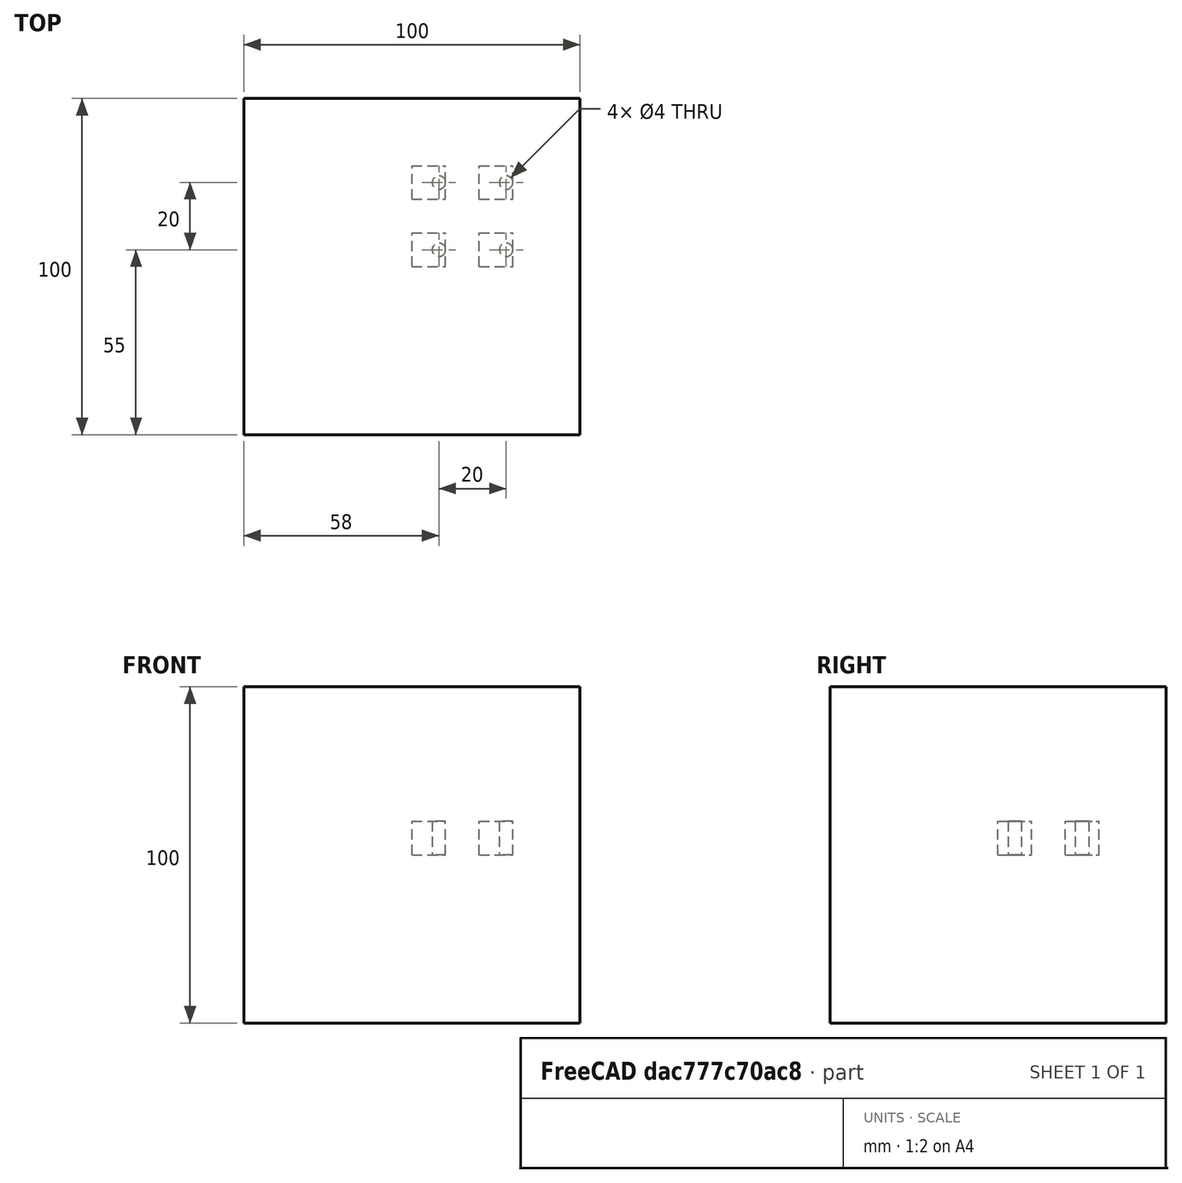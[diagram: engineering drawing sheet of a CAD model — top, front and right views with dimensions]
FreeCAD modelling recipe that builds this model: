
FCSTD DOCUMENT  (FreeCAD 0.21R33694 (Git))
Label: orthoArray_of_Cut
License: All rights reserved
objects: App::DocumentObjectGroupPython×1251, Part::FeaturePython×2, App::Part×2, Part::Box×1, Part::Cylinder×1, Part::Cut×1
note: 5 computed .brp shape members not serialized (recipe doc carries the construction recipe); baked Part::Feature solids carry a one-line shape summary decoded from their .brp

FEATURE [App::DocumentObjectGroupPython] HALFPI  # scripted group (container) (typed FeaturePython)
  name = HALFPI
  value = pi/2.
FEATURE [App::DocumentObjectGroupPython] PI  # scripted group (container) (typed FeaturePython)
  name = PI
  value = 1.*pi
FEATURE [App::DocumentObjectGroupPython] TWOPI  # scripted group (container) (typed FeaturePython)
  name = TWOPI
  value = 2.*pi
FEATURE [App::DocumentObjectGroupPython] Constants  # scripted group (container) (typed FeaturePython)
  Group = -> [HALFPI,PI,TWOPI]
FEATURE [App::DocumentObjectGroupPython] Variables  # scripted group (container) (typed FeaturePython)
FEATURE [App::DocumentObjectGroupPython] Quantities  # scripted group (container) (typed FeaturePython)
FEATURE [App::DocumentObjectGroupPython] Isotopes  # scripted group (container) (typed FeaturePython)
FEATURE [App::DocumentObjectGroupPython] Elements  # scripted group (container) (typed FeaturePython)
FEATURE [App::DocumentObjectGroupPython] Matrix  # scripted group (container) (typed FeaturePython)
FEATURE [App::DocumentObjectGroupPython] Surfaces  # scripted group (container) (typed FeaturePython)
FEATURE [App::DocumentObjectGroupPython] Opticals  # scripted group (container) (typed FeaturePython)
  Group = -> [Matrix,Surfaces]
FEATURE [App::DocumentObjectGroupPython] G4Isotopes  # scripted group (container) (typed FeaturePython)
FEATURE [App::DocumentObjectGroupPython] H_element  # scripted group (container) (typed FeaturePython)
  Z = 1
  atom_value = 1.008
  formula = H
  name = H_element
FEATURE [App::DocumentObjectGroupPython] He_element  # scripted group (container) (typed FeaturePython)
  Z = 2
  atom_value = 4.0026
  formula = He
  name = He_element
FEATURE [App::DocumentObjectGroupPython] Li_element  # scripted group (container) (typed FeaturePython)
  Z = 3
  atom_value = 6.94
  formula = Li
  name = Li_element
FEATURE [App::DocumentObjectGroupPython] Be_element  # scripted group (container) (typed FeaturePython)
  Z = 4
  atom_value = 9.01218
  formula = Be
  name = Be_element
FEATURE [App::DocumentObjectGroupPython] B_element  # scripted group (container) (typed FeaturePython)
  Z = 5
  atom_value = 10.81
  formula = B
  name = B_element
FEATURE [App::DocumentObjectGroupPython] C_element  # scripted group (container) (typed FeaturePython)
  Z = 6
  atom_value = 12.011
  formula = C
  name = C_element
FEATURE [App::DocumentObjectGroupPython] N_element  # scripted group (container) (typed FeaturePython)
  Z = 7
  atom_value = 14.007
  formula = N
  name = N_element
FEATURE [App::DocumentObjectGroupPython] O_element  # scripted group (container) (typed FeaturePython)
  Z = 8
  atom_value = 15.999
  formula = O
  name = O_element
FEATURE [App::DocumentObjectGroupPython] F_element  # scripted group (container) (typed FeaturePython)
  Z = 9
  atom_value = 18.9984
  formula = F
  name = F_element
FEATURE [App::DocumentObjectGroupPython] Ne_element  # scripted group (container) (typed FeaturePython)
  Z = 10
  atom_value = 20.1797
  formula = Ne
  name = Ne_element
FEATURE [App::DocumentObjectGroupPython] Na_element  # scripted group (container) (typed FeaturePython)
  Z = 11
  atom_value = 22.9898
  formula = Na
  name = Na_element
FEATURE [App::DocumentObjectGroupPython] Mg_element  # scripted group (container) (typed FeaturePython)
  Z = 12
  atom_value = 24.305
  formula = Mg
  name = Mg_element
FEATURE [App::DocumentObjectGroupPython] Al_element  # scripted group (container) (typed FeaturePython)
  Z = 13
  atom_value = 26.9815
  formula = Al
  name = Al_element
FEATURE [App::DocumentObjectGroupPython] Si_element  # scripted group (container) (typed FeaturePython)
  Z = 14
  atom_value = 28.085
  formula = Si
  name = Si_element
FEATURE [App::DocumentObjectGroupPython] P_element  # scripted group (container) (typed FeaturePython)
  Z = 15
  atom_value = 30.9738
  formula = P
  name = P_element
FEATURE [App::DocumentObjectGroupPython] S_element  # scripted group (container) (typed FeaturePython)
  Z = 16
  atom_value = 32.06
  formula = S
  name = S_element
FEATURE [App::DocumentObjectGroupPython] Cl_element  # scripted group (container) (typed FeaturePython)
  Z = 17
  atom_value = 35.45
  formula = Cl
  name = Cl_element
FEATURE [App::DocumentObjectGroupPython] Ar_element  # scripted group (container) (typed FeaturePython)
  Z = 18
  atom_value = 39.95
  formula = Ar
  name = Ar_element
FEATURE [App::DocumentObjectGroupPython] K_element  # scripted group (container) (typed FeaturePython)
  Z = 19
  atom_value = 39.0983
  formula = K
  name = K_element
FEATURE [App::DocumentObjectGroupPython] Ca_element  # scripted group (container) (typed FeaturePython)
  Z = 20
  atom_value = 40.078
  formula = Ca
  name = Ca_element
FEATURE [App::DocumentObjectGroupPython] Sc_element  # scripted group (container) (typed FeaturePython)
  Z = 21
  atom_value = 44.9559
  formula = Sc
  name = Sc_element
FEATURE [App::DocumentObjectGroupPython] Ti_element  # scripted group (container) (typed FeaturePython)
  Z = 22
  atom_value = 47.867
  formula = Ti
  name = Ti_element
FEATURE [App::DocumentObjectGroupPython] V_element  # scripted group (container) (typed FeaturePython)
  Z = 23
  atom_value = 50.9415
  formula = V
  name = V_element
FEATURE [App::DocumentObjectGroupPython] Cr_element  # scripted group (container) (typed FeaturePython)
  Z = 24
  atom_value = 51.9961
  formula = Cr
  name = Cr_element
FEATURE [App::DocumentObjectGroupPython] Mn_element  # scripted group (container) (typed FeaturePython)
  Z = 25
  atom_value = 54.938
  formula = Mn
  name = Mn_element
FEATURE [App::DocumentObjectGroupPython] Fe_element  # scripted group (container) (typed FeaturePython)
  Z = 26
  atom_value = 55.845
  formula = Fe
  name = Fe_element
FEATURE [App::DocumentObjectGroupPython] Co_element  # scripted group (container) (typed FeaturePython)
  Z = 27
  atom_value = 58.9332
  formula = Co
  name = Co_element
FEATURE [App::DocumentObjectGroupPython] Ni_element  # scripted group (container) (typed FeaturePython)
  Z = 28
  atom_value = 58.6934
  formula = Ni
  name = Ni_element
FEATURE [App::DocumentObjectGroupPython] Cu_element  # scripted group (container) (typed FeaturePython)
  Z = 29
  atom_value = 63.546
  formula = Cu
  name = Cu_element
FEATURE [App::DocumentObjectGroupPython] Zn_element  # scripted group (container) (typed FeaturePython)
  Z = 30
  atom_value = 65.38
  formula = Zn
  name = Zn_element
FEATURE [App::DocumentObjectGroupPython] Ga_element  # scripted group (container) (typed FeaturePython)
  Z = 31
  atom_value = 69.723
  formula = Ga
  name = Ga_element
FEATURE [App::DocumentObjectGroupPython] Ge_element  # scripted group (container) (typed FeaturePython)
  Z = 32
  atom_value = 72.63
  formula = Ge
  name = Ge_element
FEATURE [App::DocumentObjectGroupPython] As_element  # scripted group (container) (typed FeaturePython)
  Z = 33
  atom_value = 74.9216
  formula = As
  name = As_element
FEATURE [App::DocumentObjectGroupPython] Se_element  # scripted group (container) (typed FeaturePython)
  Z = 34
  atom_value = 78.971
  formula = Se
  name = Se_element
FEATURE [App::DocumentObjectGroupPython] Br_element  # scripted group (container) (typed FeaturePython)
  Z = 35
  atom_value = 79.904
  formula = Br
  name = Br_element
FEATURE [App::DocumentObjectGroupPython] Kr_element  # scripted group (container) (typed FeaturePython)
  Z = 36
  atom_value = 83.798
  formula = Kr
  name = Kr_element
FEATURE [App::DocumentObjectGroupPython] Rb_element  # scripted group (container) (typed FeaturePython)
  Z = 37
  atom_value = 85.4678
  formula = Rb
  name = Rb_element
FEATURE [App::DocumentObjectGroupPython] Sr_element  # scripted group (container) (typed FeaturePython)
  Z = 38
  atom_value = 87.62
  formula = Sr
  name = Sr_element
FEATURE [App::DocumentObjectGroupPython] Y_element  # scripted group (container) (typed FeaturePython)
  Z = 39
  atom_value = 88.9058
  formula = Y
  name = Y_element
FEATURE [App::DocumentObjectGroupPython] Zr_element  # scripted group (container) (typed FeaturePython)
  Z = 40
  atom_value = 91.224
  formula = Zr
  name = Zr_element
FEATURE [App::DocumentObjectGroupPython] Nb_element  # scripted group (container) (typed FeaturePython)
  Z = 41
  atom_value = 92.9064
  formula = Nb
  name = Nb_element
FEATURE [App::DocumentObjectGroupPython] Mo_element  # scripted group (container) (typed FeaturePython)
  Z = 42
  atom_value = 95.95
  formula = Mo
  name = Mo_element
FEATURE [App::DocumentObjectGroupPython] Tc_element  # scripted group (container) (typed FeaturePython)
  Z = 43
  atom_value = 97
  formula = Tc
  name = Tc_element
FEATURE [App::DocumentObjectGroupPython] Ru_element  # scripted group (container) (typed FeaturePython)
  Z = 44
  atom_value = 101.07
  formula = Ru
  name = Ru_element
FEATURE [App::DocumentObjectGroupPython] Rh_element  # scripted group (container) (typed FeaturePython)
  Z = 45
  atom_value = 102.905
  formula = Rh
  name = Rh_element
FEATURE [App::DocumentObjectGroupPython] Pd_element  # scripted group (container) (typed FeaturePython)
  Z = 46
  atom_value = 106.42
  formula = Pd
  name = Pd_element
FEATURE [App::DocumentObjectGroupPython] Ag_element  # scripted group (container) (typed FeaturePython)
  Z = 47
  atom_value = 107.868
  formula = Ag
  name = Ag_element
FEATURE [App::DocumentObjectGroupPython] Cd_element  # scripted group (container) (typed FeaturePython)
  Z = 48
  atom_value = 112.414
  formula = Cd
  name = Cd_element
FEATURE [App::DocumentObjectGroupPython] In_element  # scripted group (container) (typed FeaturePython)
  Z = 49
  atom_value = 114.818
  formula = In
  name = In_element
FEATURE [App::DocumentObjectGroupPython] Sn_element  # scripted group (container) (typed FeaturePython)
  Z = 50
  atom_value = 118.71
  formula = Sn
  name = Sn_element
FEATURE [App::DocumentObjectGroupPython] Sb_element  # scripted group (container) (typed FeaturePython)
  Z = 51
  atom_value = 121.76
  formula = Sb
  name = Sb_element
FEATURE [App::DocumentObjectGroupPython] Te_element  # scripted group (container) (typed FeaturePython)
  Z = 52
  atom_value = 127.6
  formula = Te
  name = Te_element
FEATURE [App::DocumentObjectGroupPython] I_element  # scripted group (container) (typed FeaturePython)
  Z = 53
  atom_value = 126.904
  formula = I
  name = I_element
FEATURE [App::DocumentObjectGroupPython] Xe_element  # scripted group (container) (typed FeaturePython)
  Z = 54
  atom_value = 131.293
  formula = Xe
  name = Xe_element
FEATURE [App::DocumentObjectGroupPython] Cs_element  # scripted group (container) (typed FeaturePython)
  Z = 55
  atom_value = 132.905
  formula = Cs
  name = Cs_element
FEATURE [App::DocumentObjectGroupPython] Ba_element  # scripted group (container) (typed FeaturePython)
  Z = 56
  atom_value = 137.327
  formula = Ba
  name = Ba_element
FEATURE [App::DocumentObjectGroupPython] La_element  # scripted group (container) (typed FeaturePython)
  Z = 57
  atom_value = 138.905
  formula = La
  name = La_element
FEATURE [App::DocumentObjectGroupPython] Ce_element  # scripted group (container) (typed FeaturePython)
  Z = 58
  atom_value = 140.116
  formula = Ce
  name = Ce_element
FEATURE [App::DocumentObjectGroupPython] Pr_element  # scripted group (container) (typed FeaturePython)
  Z = 59
  atom_value = 140.908
  formula = Pr
  name = Pr_element
FEATURE [App::DocumentObjectGroupPython] Nd_element  # scripted group (container) (typed FeaturePython)
  Z = 60
  atom_value = 144.242
  formula = Nd
  name = Nd_element
FEATURE [App::DocumentObjectGroupPython] Pm_element  # scripted group (container) (typed FeaturePython)
  Z = 61
  atom_value = 145
  formula = Pm
  name = Pm_element
FEATURE [App::DocumentObjectGroupPython] Sm_element  # scripted group (container) (typed FeaturePython)
  Z = 62
  atom_value = 150.36
  formula = Sm
  name = Sm_element
FEATURE [App::DocumentObjectGroupPython] Eu_element  # scripted group (container) (typed FeaturePython)
  Z = 63
  atom_value = 151.964
  formula = Eu
  name = Eu_element
FEATURE [App::DocumentObjectGroupPython] Gd_element  # scripted group (container) (typed FeaturePython)
  Z = 64
  atom_value = 157.25
  formula = Gd
  name = Gd_element
FEATURE [App::DocumentObjectGroupPython] Tb_element  # scripted group (container) (typed FeaturePython)
  Z = 65
  atom_value = 158.925
  formula = Tb
  name = Tb_element
FEATURE [App::DocumentObjectGroupPython] Dy_element  # scripted group (container) (typed FeaturePython)
  Z = 66
  atom_value = 162.5
  formula = Dy
  name = Dy_element
FEATURE [App::DocumentObjectGroupPython] Ho_element  # scripted group (container) (typed FeaturePython)
  Z = 67
  atom_value = 164.93
  formula = Ho
  name = Ho_element
FEATURE [App::DocumentObjectGroupPython] Er_element  # scripted group (container) (typed FeaturePython)
  Z = 68
  atom_value = 167.259
  formula = Er
  name = Er_element
FEATURE [App::DocumentObjectGroupPython] Tm_element  # scripted group (container) (typed FeaturePython)
  Z = 69
  atom_value = 168.934
  formula = Tm
  name = Tm_element
FEATURE [App::DocumentObjectGroupPython] Yb_element  # scripted group (container) (typed FeaturePython)
  Z = 70
  atom_value = 173.045
  formula = Yb
  name = Yb_element
FEATURE [App::DocumentObjectGroupPython] Lu_element  # scripted group (container) (typed FeaturePython)
  Z = 71
  atom_value = 174.967
  formula = Lu
  name = Lu_element
FEATURE [App::DocumentObjectGroupPython] Hf_element  # scripted group (container) (typed FeaturePython)
  Z = 72
  atom_value = 178.49
  formula = Hf
  name = Hf_element
FEATURE [App::DocumentObjectGroupPython] Ta_element  # scripted group (container) (typed FeaturePython)
  Z = 73
  atom_value = 180.948
  formula = Ta
  name = Ta_element
FEATURE [App::DocumentObjectGroupPython] W_element  # scripted group (container) (typed FeaturePython)
  Z = 74
  atom_value = 183.84
  formula = W
  name = W_element
FEATURE [App::DocumentObjectGroupPython] Re_element  # scripted group (container) (typed FeaturePython)
  Z = 75
  atom_value = 186.207
  formula = Re
  name = Re_element
FEATURE [App::DocumentObjectGroupPython] Os_element  # scripted group (container) (typed FeaturePython)
  Z = 76
  atom_value = 190.23
  formula = Os
  name = Os_element
FEATURE [App::DocumentObjectGroupPython] Ir_element  # scripted group (container) (typed FeaturePython)
  Z = 77
  atom_value = 192.217
  formula = Ir
  name = Ir_element
FEATURE [App::DocumentObjectGroupPython] Pt_element  # scripted group (container) (typed FeaturePython)
  Z = 78
  atom_value = 195.084
  formula = Pt
  name = Pt_element
FEATURE [App::DocumentObjectGroupPython] Au_element  # scripted group (container) (typed FeaturePython)
  Z = 79
  atom_value = 196.967
  formula = Au
  name = Au_element
FEATURE [App::DocumentObjectGroupPython] Hg_element  # scripted group (container) (typed FeaturePython)
  Z = 80
  atom_value = 200.592
  formula = Hg
  name = Hg_element
FEATURE [App::DocumentObjectGroupPython] Tl_element  # scripted group (container) (typed FeaturePython)
  Z = 81
  atom_value = 204.38
  formula = Tl
  name = Tl_element
FEATURE [App::DocumentObjectGroupPython] Pb_element  # scripted group (container) (typed FeaturePython)
  Z = 82
  atom_value = 207.2
  formula = Pb
  name = Pb_element
FEATURE [App::DocumentObjectGroupPython] Bi_element  # scripted group (container) (typed FeaturePython)
  Z = 83
  atom_value = 208.98
  formula = Bi
  name = Bi_element
FEATURE [App::DocumentObjectGroupPython] Po_element  # scripted group (container) (typed FeaturePython)
  Z = 84
  atom_value = 209
  formula = Po
  name = Po_element
FEATURE [App::DocumentObjectGroupPython] At_element  # scripted group (container) (typed FeaturePython)
  Z = 85
  atom_value = 210
  formula = At
  name = At_element
FEATURE [App::DocumentObjectGroupPython] Rn_element  # scripted group (container) (typed FeaturePython)
  Z = 86
  atom_value = 222
  formula = Rn
  name = Rn_element
FEATURE [App::DocumentObjectGroupPython] Fr_element  # scripted group (container) (typed FeaturePython)
  Z = 87
  atom_value = 223
  formula = Fr
  name = Fr_element
FEATURE [App::DocumentObjectGroupPython] Ra_element  # scripted group (container) (typed FeaturePython)
  Z = 88
  atom_value = 226
  formula = Ra
  name = Ra_element
FEATURE [App::DocumentObjectGroupPython] Ac_element  # scripted group (container) (typed FeaturePython)
  Z = 89
  atom_value = 227
  formula = Ac
  name = Ac_element
FEATURE [App::DocumentObjectGroupPython] Th_element  # scripted group (container) (typed FeaturePython)
  Z = 90
  atom_value = 232.038
  formula = Th
  name = Th_element
FEATURE [App::DocumentObjectGroupPython] Pa_element  # scripted group (container) (typed FeaturePython)
  Z = 91
  atom_value = 231.036
  formula = Pa
  name = Pa_element
FEATURE [App::DocumentObjectGroupPython] U_element  # scripted group (container) (typed FeaturePython)
  Z = 92
  atom_value = 238.029
  formula = U
  name = U_element
FEATURE [App::DocumentObjectGroupPython] Np_element  # scripted group (container) (typed FeaturePython)
  Z = 93
  atom_value = 237
  formula = Np
  name = Np_element
FEATURE [App::DocumentObjectGroupPython] Pu_element  # scripted group (container) (typed FeaturePython)
  Z = 94
  atom_value = 244
  formula = Pu
  name = Pu_element
FEATURE [App::DocumentObjectGroupPython] Am_element  # scripted group (container) (typed FeaturePython)
  Z = 95
  atom_value = 243
  formula = Am
  name = Am_element
FEATURE [App::DocumentObjectGroupPython] Cm_element  # scripted group (container) (typed FeaturePython)
  Z = 96
  atom_value = 247
  formula = Cm
  name = Cm_element
FEATURE [App::DocumentObjectGroupPython] Bk_element  # scripted group (container) (typed FeaturePython)
  Z = 97
  atom_value = 247
  formula = Bk
  name = Bk_element
FEATURE [App::DocumentObjectGroupPython] Cf_element  # scripted group (container) (typed FeaturePython)
  Z = 98
  atom_value = 251
  formula = Cf
  name = Cf_element
FEATURE [App::DocumentObjectGroupPython] G4Elements  # scripted group (container) (typed FeaturePython)
  Group = -> [H_element,He_element,Li_element,Be_element,B_element,C_element,N_element,O_element,F_element,Ne_element,Na_element,Mg_element,Al_element,Si_element,P_element,S_element,Cl_element,Ar_element,K_element,Ca_element,Sc_element,Ti_element,V_element,Cr_element,Mn_element,Fe_element,Co_element,Ni_element,Cu_element,Zn_element,Ga_element,Ge_element,As_element,Se_element,Br_element,Kr_element,Rb_element,+61 more]
FEATURE [App::DocumentObjectGroupPython] H_element001  label="H_element : 0.101"  # scripted group (container) (typed FeaturePython)
  n = 0.101327
FEATURE [App::DocumentObjectGroupPython] C_element001  label="C_element : 0.775"  # scripted group (container) (typed FeaturePython)
  n = 0.7755
FEATURE [App::DocumentObjectGroupPython] N_element001  label="N_element : 0.035"  # scripted group (container) (typed FeaturePython)
  n = 0.035057
FEATURE [App::DocumentObjectGroupPython] O_element001  label="O_element : 0.052"  # scripted group (container) (typed FeaturePython)
  n = 0.0523159
FEATURE [App::DocumentObjectGroupPython] F_element001  label="F_element : 0.017"  # scripted group (container) (typed FeaturePython)
  n = 0.017422
FEATURE [App::DocumentObjectGroupPython] Ca_element001  label="Ca_element : 0.018"  # scripted group (container) (typed FeaturePython)
  n = 0.018378
FEATURE [App::DocumentObjectGroupPython] G4_A_150_TISSUE  label="G4_A-150_TISSUE"  # scripted group (container) (typed FeaturePython)
  Dunit = g/cm3
  Dvalue = 1.127
  Group = -> [H_element001,C_element001,N_element001,O_element001,F_element001,Ca_element001]
  conduct = 2
  density = 1
  expand = 3
  formula = G4_A-150_TISSUE
  name = G4_A-150_TISSUE
  specific = 4
FEATURE [App::DocumentObjectGroupPython] C_element002  label="C_element : 3"  # scripted group (container) (typed FeaturePython)
  n = 3
  ref = C_element
FEATURE [App::DocumentObjectGroupPython] H_element002  label="H_element : 6"  # scripted group (container) (typed FeaturePython)
  n = 6
  ref = H_element
FEATURE [App::DocumentObjectGroupPython] O_element002  label="O_element : 1"  # scripted group (container) (typed FeaturePython)
  n = 1
  ref = O_element
FEATURE [App::DocumentObjectGroupPython] G4_ACETONE  # scripted group (container) (typed FeaturePython)
  Dunit = g/cm3
  Dvalue = 0.7899
  Group = -> [C_element002,H_element002,O_element002]
  conduct = 2
  density = 1
  expand = 3
  formula = G4_ACETONE
  name = G4_ACETONE
  specific = 4
FEATURE [App::DocumentObjectGroupPython] C_element003  label="C_element : 2"  # scripted group (container) (typed FeaturePython)
  n = 2
  ref = C_element
FEATURE [App::DocumentObjectGroupPython] H_element003  label="H_element : 2"  # scripted group (container) (typed FeaturePython)
  n = 2
  ref = H_element
FEATURE [App::DocumentObjectGroupPython] G4_ACETYLENE  # scripted group (container) (typed FeaturePython)
  Dunit = g/cm3
  Dvalue = 0.0010967
  Group = -> [C_element003,H_element003]
  conduct = 2
  density = 1
  expand = 3
  formula = G4_ACETYLENE
  name = G4_ACETYLENE
  specific = 4
FEATURE [App::DocumentObjectGroupPython] C_element004  label="C_element : 5"  # scripted group (container) (typed FeaturePython)
  n = 5
  ref = C_element
FEATURE [App::DocumentObjectGroupPython] H_element004  label="H_element : 5"  # scripted group (container) (typed FeaturePython)
  n = 5
  ref = H_element
FEATURE [App::DocumentObjectGroupPython] N_element002  label="N_element : 5"  # scripted group (container) (typed FeaturePython)
  n = 5
  ref = N_element
FEATURE [App::DocumentObjectGroupPython] G4_ADENINE  # scripted group (container) (typed FeaturePython)
  Dunit = g/cm3
  Dvalue = 1.6
  Group = -> [C_element004,H_element004,N_element002]
  conduct = 2
  density = 1
  expand = 3
  formula = G4_ADENINE
  name = G4_ADENINE
  specific = 4
FEATURE [App::DocumentObjectGroupPython] H_element005  label="H_element : 0.114"  # scripted group (container) (typed FeaturePython)
  n = 0.114
FEATURE [App::DocumentObjectGroupPython] C_element005  label="C_element : 0.598"  # scripted group (container) (typed FeaturePython)
  n = 0.598
FEATURE [App::DocumentObjectGroupPython] N_element003  label="N_element : 0.007"  # scripted group (container) (typed FeaturePython)
  n = 0.007
FEATURE [App::DocumentObjectGroupPython] O_element003  label="O_element : 0.278"  # scripted group (container) (typed FeaturePython)
  n = 0.278
FEATURE [App::DocumentObjectGroupPython] Na_element001  label="Na_element : 0.001"  # scripted group (container) (typed FeaturePython)
  n = 0.001
FEATURE [App::DocumentObjectGroupPython] S_element001  label="S_element : 0.001"  # scripted group (container) (typed FeaturePython)
  n = 0.001
FEATURE [App::DocumentObjectGroupPython] Cl_element001  label="Cl_element : 0.001"  # scripted group (container) (typed FeaturePython)
  n = 0.001
FEATURE [App::DocumentObjectGroupPython] G4_ADIPOSE_TISSUE_ICRP  # scripted group (container) (typed FeaturePython)
  Dunit = g/cm3
  Dvalue = 0.95
  Group = -> [H_element005,C_element005,N_element003,O_element003,Na_element001,S_element001,Cl_element001]
  conduct = 2
  density = 1
  expand = 3
  formula = G4_ADIPOSE_TISSUE_ICRP
  name = G4_ADIPOSE_TISSUE_ICRP
  specific = 4
FEATURE [App::DocumentObjectGroupPython] C_element006  label="C_element : 0.000"  # scripted group (container) (typed FeaturePython)
  n = 0.000124
FEATURE [App::DocumentObjectGroupPython] N_element004  label="N_element : 0.755"  # scripted group (container) (typed FeaturePython)
  n = 0.755268
FEATURE [App::DocumentObjectGroupPython] O_element004  label="O_element : 0.232"  # scripted group (container) (typed FeaturePython)
  n = 0.231781
FEATURE [App::DocumentObjectGroupPython] Ar_element001  label="Ar_element : 0.013"  # scripted group (container) (typed FeaturePython)
  n = 0.012827
FEATURE [App::DocumentObjectGroupPython] G4_AIR  # scripted group (container) (typed FeaturePython)
  Dunit = g/cm3
  Dvalue = 0.00120479
  Group = -> [C_element006,N_element004,O_element004,Ar_element001]
  conduct = 2
  density = 1
  expand = 3
  formula = G4_AIR
  name = G4_AIR
  specific = 4
FEATURE [App::DocumentObjectGroupPython] C_element007  label="C_element : 006"  # scripted group (container) (typed FeaturePython)
  n = 3
  ref = C_element
FEATURE [App::DocumentObjectGroupPython] H_element006  label="H_element : 7"  # scripted group (container) (typed FeaturePython)
  n = 7
  ref = H_element
FEATURE [App::DocumentObjectGroupPython] N_element005  label="N_element : 1"  # scripted group (container) (typed FeaturePython)
  n = 1
  ref = N_element
FEATURE [App::DocumentObjectGroupPython] O_element005  label="O_element : 2"  # scripted group (container) (typed FeaturePython)
  n = 2
  ref = O_element
FEATURE [App::DocumentObjectGroupPython] G4_ALANINE  # scripted group (container) (typed FeaturePython)
  Dunit = g/cm3
  Dvalue = 1.42
  Group = -> [C_element007,H_element006,N_element005,O_element005]
  conduct = 2
  density = 1
  expand = 3
  formula = G4_ALANINE
  name = G4_ALANINE
  specific = 4
FEATURE [App::DocumentObjectGroupPython] Al_element001  label="Al_element : 2"  # scripted group (container) (typed FeaturePython)
  n = 2
  ref = Al_element
FEATURE [App::DocumentObjectGroupPython] O_element006  label="O_element : 3"  # scripted group (container) (typed FeaturePython)
  n = 3
  ref = O_element
FEATURE [App::DocumentObjectGroupPython] G4_ALUMINUM_OXIDE  # scripted group (container) (typed FeaturePython)
  Dunit = g/cm3
  Dvalue = 3.97
  Group = -> [Al_element001,O_element006]
  conduct = 2
  density = 1
  expand = 3
  formula = G4_ALUMINUM_OXIDE
  name = G4_ALUMINUM_OXIDE
  specific = 4
FEATURE [App::DocumentObjectGroupPython] H_element007  label="H_element : 0.106"  # scripted group (container) (typed FeaturePython)
  n = 0.10593
FEATURE [App::DocumentObjectGroupPython] C_element008  label="C_element : 0.789"  # scripted group (container) (typed FeaturePython)
  n = 0.788974
FEATURE [App::DocumentObjectGroupPython] O_element007  label="O_element : 0.105"  # scripted group (container) (typed FeaturePython)
  n = 0.105096
FEATURE [App::DocumentObjectGroupPython] G4_AMBER  # scripted group (container) (typed FeaturePython)
  Dunit = g/cm3
  Dvalue = 1.1
  Group = -> [H_element007,C_element008,O_element007]
  conduct = 2
  density = 1
  expand = 3
  formula = G4_AMBER
  name = G4_AMBER
  specific = 4
FEATURE [App::DocumentObjectGroupPython] N_element006  label="N_element : 006"  # scripted group (container) (typed FeaturePython)
  n = 1
  ref = N_element
FEATURE [App::DocumentObjectGroupPython] H_element008  label="H_element : 3"  # scripted group (container) (typed FeaturePython)
  n = 3
  ref = H_element
FEATURE [App::DocumentObjectGroupPython] G4_AMMONIA  # scripted group (container) (typed FeaturePython)
  Dunit = g/cm3
  Dvalue = 0.000826019
  Group = -> [N_element006,H_element008]
  conduct = 2
  density = 1
  expand = 3
  formula = G4_AMMONIA
  name = G4_AMMONIA
  specific = 4
FEATURE [App::DocumentObjectGroupPython] C_element009  label="C_element : 6"  # scripted group (container) (typed FeaturePython)
  n = 6
  ref = C_element
FEATURE [App::DocumentObjectGroupPython] H_element009  label="H_element : 008"  # scripted group (container) (typed FeaturePython)
  n = 7
  ref = H_element
FEATURE [App::DocumentObjectGroupPython] N_element007  label="N_element : 007"  # scripted group (container) (typed FeaturePython)
  n = 1
  ref = N_element
FEATURE [App::DocumentObjectGroupPython] G4_ANILINE  # scripted group (container) (typed FeaturePython)
  Dunit = g/cm3
  Dvalue = 1.0235
  Group = -> [C_element009,H_element009,N_element007]
  conduct = 2
  density = 1
  expand = 3
  formula = G4_ANILINE
  name = G4_ANILINE
  specific = 4
FEATURE [App::DocumentObjectGroupPython] C_element010  label="C_element : 14"  # scripted group (container) (typed FeaturePython)
  n = 14
  ref = C_element
FEATURE [App::DocumentObjectGroupPython] H_element010  label="H_element : 10"  # scripted group (container) (typed FeaturePython)
  n = 10
  ref = H_element
FEATURE [App::DocumentObjectGroupPython] G4_ANTHRACENE  # scripted group (container) (typed FeaturePython)
  Dunit = g/cm3
  Dvalue = 1.283
  Group = -> [C_element010,H_element010]
  conduct = 2
  density = 1
  expand = 3
  formula = G4_ANTHRACENE
  name = G4_ANTHRACENE
  specific = 4
FEATURE [App::DocumentObjectGroupPython] H_element011  label="H_element : 0.065"  # scripted group (container) (typed FeaturePython)
  n = 0.0654709
FEATURE [App::DocumentObjectGroupPython] C_element011  label="C_element : 0.537"  # scripted group (container) (typed FeaturePython)
  n = 0.536944
FEATURE [App::DocumentObjectGroupPython] N_element008  label="N_element : 0.021"  # scripted group (container) (typed FeaturePython)
  n = 0.0215
FEATURE [App::DocumentObjectGroupPython] O_element008  label="O_element : 0.032"  # scripted group (container) (typed FeaturePython)
  n = 0.032085
FEATURE [App::DocumentObjectGroupPython] F_element002  label="F_element : 0.167"  # scripted group (container) (typed FeaturePython)
  n = 0.167411
FEATURE [App::DocumentObjectGroupPython] Ca_element002  label="Ca_element : 0.177"  # scripted group (container) (typed FeaturePython)
  n = 0.176589
FEATURE [App::DocumentObjectGroupPython] G4_B_100_BONE  label="G4_B-100_BONE"  # scripted group (container) (typed FeaturePython)
  Dunit = g/cm3
  Dvalue = 1.45
  Group = -> [H_element011,C_element011,N_element008,O_element008,F_element002,Ca_element002]
  conduct = 2
  density = 1
  expand = 3
  formula = G4_B-100_BONE
  name = G4_B-100_BONE
  specific = 4
FEATURE [App::DocumentObjectGroupPython] H_element012  label="H_element : 0.057"  # scripted group (container) (typed FeaturePython)
  n = 0.057441
FEATURE [App::DocumentObjectGroupPython] C_element012  label="C_element : 0.790"  # scripted group (container) (typed FeaturePython)
  n = 0.774591
FEATURE [App::DocumentObjectGroupPython] O_element009  label="O_element : 0.168"  # scripted group (container) (typed FeaturePython)
  n = 0.167968
FEATURE [App::DocumentObjectGroupPython] G4_BAKELITE  # scripted group (container) (typed FeaturePython)
  Dunit = g/cm3
  Dvalue = 1.25
  Group = -> [H_element012,C_element012,O_element009]
  conduct = 2
  density = 1
  expand = 3
  formula = G4_BAKELITE
  name = G4_BAKELITE
  specific = 4
FEATURE [App::DocumentObjectGroupPython] Ba_element001  label="Ba_element : 1"  # scripted group (container) (typed FeaturePython)
  n = 1
  ref = Ba_element
FEATURE [App::DocumentObjectGroupPython] F_element003  label="F_element : 2"  # scripted group (container) (typed FeaturePython)
  n = 2
  ref = F_element
FEATURE [App::DocumentObjectGroupPython] G4_BARIUM_FLUORIDE  # scripted group (container) (typed FeaturePython)
  Dunit = g/cm3
  Dvalue = 4.89
  Group = -> [Ba_element001,F_element003]
  conduct = 2
  density = 1
  expand = 3
  formula = G4_BARIUM_FLUORIDE
  name = G4_BARIUM_FLUORIDE
  specific = 4
FEATURE [App::DocumentObjectGroupPython] Ba_element002  label="Ba_element : 002"  # scripted group (container) (typed FeaturePython)
  n = 1
  ref = Ba_element
FEATURE [App::DocumentObjectGroupPython] S_element002  label="S_element : 1"  # scripted group (container) (typed FeaturePython)
  n = 1
  ref = S_element
FEATURE [App::DocumentObjectGroupPython] O_element010  label="O_element : 4"  # scripted group (container) (typed FeaturePython)
  n = 4
  ref = O_element
FEATURE [App::DocumentObjectGroupPython] G4_BARIUM_SULFATE  # scripted group (container) (typed FeaturePython)
  Dunit = g/cm3
  Dvalue = 4.5
  Group = -> [Ba_element002,S_element002,O_element010]
  conduct = 2
  density = 1
  expand = 3
  formula = G4_BARIUM_SULFATE
  name = G4_BARIUM_SULFATE
  specific = 4
FEATURE [App::DocumentObjectGroupPython] C_element013  label="C_element : 007"  # scripted group (container) (typed FeaturePython)
  n = 6
  ref = C_element
FEATURE [App::DocumentObjectGroupPython] H_element013  label="H_element : 009"  # scripted group (container) (typed FeaturePython)
  n = 6
  ref = H_element
FEATURE [App::DocumentObjectGroupPython] G4_BENZENE  # scripted group (container) (typed FeaturePython)
  Dunit = g/cm3
  Dvalue = 0.87865
  Group = -> [C_element013,H_element013]
  conduct = 2
  density = 1
  expand = 3
  formula = G4_BENZENE
  name = G4_BENZENE
  specific = 4
FEATURE [App::DocumentObjectGroupPython] Be_element001  label="Be_element : 1"  # scripted group (container) (typed FeaturePython)
  n = 1
  ref = Be_element
FEATURE [App::DocumentObjectGroupPython] O_element011  label="O_element : 005"  # scripted group (container) (typed FeaturePython)
  n = 1
  ref = O_element
FEATURE [App::DocumentObjectGroupPython] G4_BERYLLIUM_OXIDE  # scripted group (container) (typed FeaturePython)
  Dunit = g/cm3
  Dvalue = 3.01
  Group = -> [Be_element001,O_element011]
  conduct = 2
  density = 1
  expand = 3
  formula = G4_BERYLLIUM_OXIDE
  name = G4_BERYLLIUM_OXIDE
  specific = 4
FEATURE [App::DocumentObjectGroupPython] Bi_element001  label="Bi_element : 4"  # scripted group (container) (typed FeaturePython)
  n = 4
  ref = Bi_element
FEATURE [App::DocumentObjectGroupPython] Ge_element001  label="Ge_element : 3"  # scripted group (container) (typed FeaturePython)
  n = 3
  ref = Ge_element
FEATURE [App::DocumentObjectGroupPython] O_element012  label="O_element : 12"  # scripted group (container) (typed FeaturePython)
  n = 12
  ref = O_element
FEATURE [App::DocumentObjectGroupPython] G4_BGO  # scripted group (container) (typed FeaturePython)
  Dunit = g/cm3
  Dvalue = 7.13
  Group = -> [Bi_element001,Ge_element001,O_element012]
  conduct = 2
  density = 1
  expand = 3
  formula = G4_BGO
  name = G4_BGO
  specific = 4
FEATURE [App::DocumentObjectGroupPython] H_element014  label="H_element : 0.102"  # scripted group (container) (typed FeaturePython)
  n = 0.102
FEATURE [App::DocumentObjectGroupPython] C_element014  label="C_element : 0.110"  # scripted group (container) (typed FeaturePython)
  n = 0.11
FEATURE [App::DocumentObjectGroupPython] N_element009  label="N_element : 0.033"  # scripted group (container) (typed FeaturePython)
  n = 0.033
FEATURE [App::DocumentObjectGroupPython] O_element013  label="O_element : 0.745"  # scripted group (container) (typed FeaturePython)
  n = 0.745
FEATURE [App::DocumentObjectGroupPython] Na_element002  label="Na_element : 0.002"  # scripted group (container) (typed FeaturePython)
  n = 0.001
FEATURE [App::DocumentObjectGroupPython] P_element001  label="P_element : 0.001"  # scripted group (container) (typed FeaturePython)
  n = 0.001
FEATURE [App::DocumentObjectGroupPython] S_element003  label="S_element : 0.002"  # scripted group (container) (typed FeaturePython)
  n = 0.002
FEATURE [App::DocumentObjectGroupPython] Cl_element002  label="Cl_element : 0.003"  # scripted group (container) (typed FeaturePython)
  n = 0.003
FEATURE [App::DocumentObjectGroupPython] K_element001  label="K_element : 0.002"  # scripted group (container) (typed FeaturePython)
  n = 0.002
FEATURE [App::DocumentObjectGroupPython] Fe_element001  label="Fe_element : 0.001"  # scripted group (container) (typed FeaturePython)
  n = 0.001
FEATURE [App::DocumentObjectGroupPython] G4_BLOOD_ICRP  # scripted group (container) (typed FeaturePython)
  Dunit = g/cm3
  Dvalue = 1.06
  Group = -> [H_element014,C_element014,N_element009,O_element013,Na_element002,P_element001,S_element003,Cl_element002,K_element001,Fe_element001]
  conduct = 2
  density = 1
  expand = 3
  formula = G4_BLOOD_ICRP
  name = G4_BLOOD_ICRP
  specific = 4
FEATURE [App::DocumentObjectGroupPython] H_element015  label="H_element : 0.064"  # scripted group (container) (typed FeaturePython)
  n = 0.064
FEATURE [App::DocumentObjectGroupPython] C_element015  label="C_element : 0.278"  # scripted group (container) (typed FeaturePython)
  n = 0.278
FEATURE [App::DocumentObjectGroupPython] N_element010  label="N_element : 0.027"  # scripted group (container) (typed FeaturePython)
  n = 0.027
FEATURE [App::DocumentObjectGroupPython] O_element014  label="O_element : 0.410"  # scripted group (container) (typed FeaturePython)
  n = 0.41
FEATURE [App::DocumentObjectGroupPython] Mg_element001  label="Mg_element : 0.002"  # scripted group (container) (typed FeaturePython)
  n = 0.002
FEATURE [App::DocumentObjectGroupPython] P_element002  label="P_element : 0.070"  # scripted group (container) (typed FeaturePython)
  n = 0.07
FEATURE [App::DocumentObjectGroupPython] S_element004  label="S_element : 0.003"  # scripted group (container) (typed FeaturePython)
  n = 0.002
FEATURE [App::DocumentObjectGroupPython] Ca_element003  label="Ca_element : 0.147"  # scripted group (container) (typed FeaturePython)
  n = 0.147
FEATURE [App::DocumentObjectGroupPython] G4_BONE_COMPACT_ICRU  # scripted group (container) (typed FeaturePython)
  Dunit = g/cm3
  Dvalue = 1.85
  Group = -> [H_element015,C_element015,N_element010,O_element014,Mg_element001,P_element002,S_element004,Ca_element003]
  conduct = 2
  density = 1
  expand = 3
  formula = G4_BONE_COMPACT_ICRU
  name = G4_BONE_COMPACT_ICRU
  specific = 4
FEATURE [App::DocumentObjectGroupPython] H_element016  label="H_element : 0.034"  # scripted group (container) (typed FeaturePython)
  n = 0.034
FEATURE [App::DocumentObjectGroupPython] C_element016  label="C_element : 0.155"  # scripted group (container) (typed FeaturePython)
  n = 0.155
FEATURE [App::DocumentObjectGroupPython] N_element011  label="N_element : 0.042"  # scripted group (container) (typed FeaturePython)
  n = 0.042
FEATURE [App::DocumentObjectGroupPython] O_element015  label="O_element : 0.435"  # scripted group (container) (typed FeaturePython)
  n = 0.435
FEATURE [App::DocumentObjectGroupPython] Na_element003  label="Na_element : 0.003"  # scripted group (container) (typed FeaturePython)
  n = 0.001
FEATURE [App::DocumentObjectGroupPython] Mg_element002  label="Mg_element : 0.003"  # scripted group (container) (typed FeaturePython)
  n = 0.002
FEATURE [App::DocumentObjectGroupPython] P_element003  label="P_element : 0.103"  # scripted group (container) (typed FeaturePython)
  n = 0.103
FEATURE [App::DocumentObjectGroupPython] S_element005  label="S_element : 0.004"  # scripted group (container) (typed FeaturePython)
  n = 0.003
FEATURE [App::DocumentObjectGroupPython] Ca_element004  label="Ca_element : 0.225"  # scripted group (container) (typed FeaturePython)
  n = 0.225
FEATURE [App::DocumentObjectGroupPython] G4_BONE_CORTICAL_ICRP  # scripted group (container) (typed FeaturePython)
  Dunit = g/cm3
  Dvalue = 1.92
  Group = -> [H_element016,C_element016,N_element011,O_element015,Na_element003,Mg_element002,P_element003,S_element005,Ca_element004]
  conduct = 2
  density = 1
  expand = 3
  formula = G4_BONE_CORTICAL_ICRP
  name = G4_BONE_CORTICAL_ICRP
  specific = 4
FEATURE [App::DocumentObjectGroupPython] B_element001  label="B_element : 4"  # scripted group (container) (typed FeaturePython)
  n = 4
  ref = B_element
FEATURE [App::DocumentObjectGroupPython] C_element017  label="C_element : 1"  # scripted group (container) (typed FeaturePython)
  n = 1
  ref = C_element
FEATURE [App::DocumentObjectGroupPython] G4_BORON_CARBIDE  # scripted group (container) (typed FeaturePython)
  Dunit = g/cm3
  Dvalue = 2.52
  Group = -> [B_element001,C_element017]
  conduct = 2
  density = 1
  expand = 3
  formula = G4_BORON_CARBIDE
  name = G4_BORON_CARBIDE
  specific = 4
FEATURE [App::DocumentObjectGroupPython] B_element002  label="B_element : 2"  # scripted group (container) (typed FeaturePython)
  n = 2
  ref = B_element
FEATURE [App::DocumentObjectGroupPython] O_element016  label="O_element : 006"  # scripted group (container) (typed FeaturePython)
  n = 3
  ref = O_element
FEATURE [App::DocumentObjectGroupPython] G4_BORON_OXIDE  # scripted group (container) (typed FeaturePython)
  Dunit = g/cm3
  Dvalue = 1.812
  Group = -> [B_element002,O_element016]
  conduct = 2
  density = 1
  expand = 3
  formula = G4_BORON_OXIDE
  name = G4_BORON_OXIDE
  specific = 4
FEATURE [App::DocumentObjectGroupPython] H_element017  label="H_element : 0.107"  # scripted group (container) (typed FeaturePython)
  n = 0.107
FEATURE [App::DocumentObjectGroupPython] C_element018  label="C_element : 0.145"  # scripted group (container) (typed FeaturePython)
  n = 0.145
FEATURE [App::DocumentObjectGroupPython] N_element012  label="N_element : 0.022"  # scripted group (container) (typed FeaturePython)
  n = 0.022
FEATURE [App::DocumentObjectGroupPython] O_element017  label="O_element : 0.712"  # scripted group (container) (typed FeaturePython)
  n = 0.712
FEATURE [App::DocumentObjectGroupPython] Na_element004  label="Na_element : 0.004"  # scripted group (container) (typed FeaturePython)
  n = 0.002
FEATURE [App::DocumentObjectGroupPython] P_element004  label="P_element : 0.004"  # scripted group (container) (typed FeaturePython)
  n = 0.004
FEATURE [App::DocumentObjectGroupPython] S_element006  label="S_element : 0.005"  # scripted group (container) (typed FeaturePython)
  n = 0.002
FEATURE [App::DocumentObjectGroupPython] Cl_element003  label="Cl_element : 0.004"  # scripted group (container) (typed FeaturePython)
  n = 0.003
FEATURE [App::DocumentObjectGroupPython] K_element002  label="K_element : 0.003"  # scripted group (container) (typed FeaturePython)
  n = 0.003
FEATURE [App::DocumentObjectGroupPython] G4_BRAIN_ICRP  # scripted group (container) (typed FeaturePython)
  Dunit = g/cm3
  Dvalue = 1.04
  Group = -> [H_element017,C_element018,N_element012,O_element017,Na_element004,P_element004,S_element006,Cl_element003,K_element002]
  conduct = 2
  density = 1
  expand = 3
  formula = G4_BRAIN_ICRP
  name = G4_BRAIN_ICRP
  specific = 4
FEATURE [App::DocumentObjectGroupPython] C_element019  label="C_element : 4"  # scripted group (container) (typed FeaturePython)
  n = 4
  ref = C_element
FEATURE [App::DocumentObjectGroupPython] H_element018  label="H_element : 010"  # scripted group (container) (typed FeaturePython)
  n = 10
  ref = H_element
FEATURE [App::DocumentObjectGroupPython] G4_BUTANE  # scripted group (container) (typed FeaturePython)
  Dunit = g/cm3
  Dvalue = 0.00249343
  Group = -> [C_element019,H_element018]
  conduct = 2
  density = 1
  expand = 3
  formula = G4_BUTANE
  name = G4_BUTANE
  specific = 4
FEATURE [App::DocumentObjectGroupPython] C_element020  label="C_element : 008"  # scripted group (container) (typed FeaturePython)
  n = 4
  ref = C_element
FEATURE [App::DocumentObjectGroupPython] H_element019  label="H_element : 011"  # scripted group (container) (typed FeaturePython)
  n = 10
  ref = H_element
FEATURE [App::DocumentObjectGroupPython] O_element018  label="O_element : 007"  # scripted group (container) (typed FeaturePython)
  n = 1
  ref = O_element
FEATURE [App::DocumentObjectGroupPython] G4_N_BUTYL_ALCOHOL  label="G4_N-BUTYL_ALCOHOL"  # scripted group (container) (typed FeaturePython)
  Dunit = g/cm3
  Dvalue = 0.8098
  Group = -> [C_element020,H_element019,O_element018]
  conduct = 2
  density = 1
  expand = 3
  formula = G4_N-BUTYL_ALCOHOL
  name = G4_N-BUTYL_ALCOHOL
  specific = 4
FEATURE [App::DocumentObjectGroupPython] H_element020  label="H_element : 0.025"  # scripted group (container) (typed FeaturePython)
  n = 0.02468
FEATURE [App::DocumentObjectGroupPython] C_element021  label="C_element : 0.502"  # scripted group (container) (typed FeaturePython)
  n = 0.501611
FEATURE [App::DocumentObjectGroupPython] O_element019  label="O_element : 0.005"  # scripted group (container) (typed FeaturePython)
  n = 0.004527
FEATURE [App::DocumentObjectGroupPython] F_element004  label="F_element : 0.465"  # scripted group (container) (typed FeaturePython)
  n = 0.465209
FEATURE [App::DocumentObjectGroupPython] Si_element001  label="Si_element : 0.004"  # scripted group (container) (typed FeaturePython)
  n = 0.003973
FEATURE [App::DocumentObjectGroupPython] G4_C_552  label="G4_C-552"  # scripted group (container) (typed FeaturePython)
  Dunit = g/cm3
  Dvalue = 1.76
  Group = -> [H_element020,C_element021,O_element019,F_element004,Si_element001]
  conduct = 2
  density = 1
  expand = 3
  formula = G4_C-552
  name = G4_C-552
  specific = 4
FEATURE [App::DocumentObjectGroupPython] Cd_element001  label="Cd_element : 1"  # scripted group (container) (typed FeaturePython)
  n = 1
  ref = Cd_element
FEATURE [App::DocumentObjectGroupPython] Te_element001  label="Te_element : 1"  # scripted group (container) (typed FeaturePython)
  n = 1
  ref = Te_element
FEATURE [App::DocumentObjectGroupPython] G4_CADMIUM_TELLURIDE  # scripted group (container) (typed FeaturePython)
  Dunit = g/cm3
  Dvalue = 6.2
  Group = -> [Cd_element001,Te_element001]
  conduct = 2
  density = 1
  expand = 3
  formula = G4_CADMIUM_TELLURIDE
  name = G4_CADMIUM_TELLURIDE
  specific = 4
FEATURE [App::DocumentObjectGroupPython] Cd_element002  label="Cd_element : 002"  # scripted group (container) (typed FeaturePython)
  n = 1
  ref = Cd_element
FEATURE [App::DocumentObjectGroupPython] W_element001  label="W_element : 1"  # scripted group (container) (typed FeaturePython)
  n = 1
  ref = W_element
FEATURE [App::DocumentObjectGroupPython] O_element020  label="O_element : 008"  # scripted group (container) (typed FeaturePython)
  n = 4
  ref = O_element
FEATURE [App::DocumentObjectGroupPython] G4_CADMIUM_TUNGSTATE  # scripted group (container) (typed FeaturePython)
  Dunit = g/cm3
  Dvalue = 7.9
  Group = -> [Cd_element002,W_element001,O_element020]
  conduct = 2
  density = 1
  expand = 3
  formula = G4_CADMIUM_TUNGSTATE
  name = G4_CADMIUM_TUNGSTATE
  specific = 4
FEATURE [App::DocumentObjectGroupPython] Ca_element005  label="Ca_element : 1"  # scripted group (container) (typed FeaturePython)
  n = 1
  ref = Ca_element
FEATURE [App::DocumentObjectGroupPython] C_element022  label="C_element : 009"  # scripted group (container) (typed FeaturePython)
  n = 1
  ref = C_element
FEATURE [App::DocumentObjectGroupPython] O_element021  label="O_element : 009"  # scripted group (container) (typed FeaturePython)
  n = 3
  ref = O_element
FEATURE [App::DocumentObjectGroupPython] G4_CALCIUM_CARBONATE  # scripted group (container) (typed FeaturePython)
  Dunit = g/cm3
  Dvalue = 2.8
  Group = -> [Ca_element005,C_element022,O_element021]
  conduct = 2
  density = 1
  expand = 3
  formula = G4_CALCIUM_CARBONATE
  name = G4_CALCIUM_CARBONATE
  specific = 4
FEATURE [App::DocumentObjectGroupPython] Ca_element006  label="Ca_element : 002"  # scripted group (container) (typed FeaturePython)
  n = 1
  ref = Ca_element
FEATURE [App::DocumentObjectGroupPython] F_element005  label="F_element : 003"  # scripted group (container) (typed FeaturePython)
  n = 2
  ref = F_element
FEATURE [App::DocumentObjectGroupPython] G4_CALCIUM_FLUORIDE  # scripted group (container) (typed FeaturePython)
  Dunit = g/cm3
  Dvalue = 3.18
  Group = -> [Ca_element006,F_element005]
  conduct = 2
  density = 1
  expand = 3
  formula = G4_CALCIUM_FLUORIDE
  name = G4_CALCIUM_FLUORIDE
  specific = 4
FEATURE [App::DocumentObjectGroupPython] Ca_element007  label="Ca_element : 003"  # scripted group (container) (typed FeaturePython)
  n = 1
  ref = Ca_element
FEATURE [App::DocumentObjectGroupPython] O_element022  label="O_element : 010"  # scripted group (container) (typed FeaturePython)
  n = 1
  ref = O_element
FEATURE [App::DocumentObjectGroupPython] G4_CALCIUM_OXIDE  # scripted group (container) (typed FeaturePython)
  Dunit = g/cm3
  Dvalue = 3.3
  Group = -> [Ca_element007,O_element022]
  conduct = 2
  density = 1
  expand = 3
  formula = G4_CALCIUM_OXIDE
  name = G4_CALCIUM_OXIDE
  specific = 4
FEATURE [App::DocumentObjectGroupPython] Ca_element008  label="Ca_element : 004"  # scripted group (container) (typed FeaturePython)
  n = 1
  ref = Ca_element
FEATURE [App::DocumentObjectGroupPython] S_element007  label="S_element : 002"  # scripted group (container) (typed FeaturePython)
  n = 1
  ref = S_element
FEATURE [App::DocumentObjectGroupPython] O_element023  label="O_element : 011"  # scripted group (container) (typed FeaturePython)
  n = 4
  ref = O_element
FEATURE [App::DocumentObjectGroupPython] G4_CALCIUM_SULFATE  # scripted group (container) (typed FeaturePython)
  Dunit = g/cm3
  Dvalue = 2.96
  Group = -> [Ca_element008,S_element007,O_element023]
  conduct = 2
  density = 1
  expand = 3
  formula = G4_CALCIUM_SULFATE
  name = G4_CALCIUM_SULFATE
  specific = 4
FEATURE [App::DocumentObjectGroupPython] Ca_element009  label="Ca_element : 005"  # scripted group (container) (typed FeaturePython)
  n = 1
  ref = Ca_element
FEATURE [App::DocumentObjectGroupPython] W_element002  label="W_element : 002"  # scripted group (container) (typed FeaturePython)
  n = 1
  ref = W_element
FEATURE [App::DocumentObjectGroupPython] O_element024  label="O_element : 012"  # scripted group (container) (typed FeaturePython)
  n = 4
  ref = O_element
FEATURE [App::DocumentObjectGroupPython] G4_CALCIUM_TUNGSTATE  # scripted group (container) (typed FeaturePython)
  Dunit = g/cm3
  Dvalue = 6.062
  Group = -> [Ca_element009,W_element002,O_element024]
  conduct = 2
  density = 1
  expand = 3
  formula = G4_CALCIUM_TUNGSTATE
  name = G4_CALCIUM_TUNGSTATE
  specific = 4
FEATURE [App::DocumentObjectGroupPython] C_element023  label="C_element : 010"  # scripted group (container) (typed FeaturePython)
  n = 1
  ref = C_element
FEATURE [App::DocumentObjectGroupPython] O_element025  label="O_element : 013"  # scripted group (container) (typed FeaturePython)
  n = 2
  ref = O_element
FEATURE [App::DocumentObjectGroupPython] G4_CARBON_DIOXIDE  # scripted group (container) (typed FeaturePython)
  Dunit = g/cm3
  Dvalue = 0.00184212
  Group = -> [C_element023,O_element025]
  conduct = 2
  density = 1
  expand = 3
  formula = G4_CARBON_DIOXIDE
  name = G4_CARBON_DIOXIDE
  specific = 4
FEATURE [App::DocumentObjectGroupPython] C_element024  label="C_element : 011"  # scripted group (container) (typed FeaturePython)
  n = 1
  ref = C_element
FEATURE [App::DocumentObjectGroupPython] Cl_element004  label="Cl_element : 4"  # scripted group (container) (typed FeaturePython)
  n = 4
  ref = Cl_element
FEATURE [App::DocumentObjectGroupPython] G4_CARBON_TETRACHLORIDE  # scripted group (container) (typed FeaturePython)
  Dunit = g/cm3
  Dvalue = 1.594
  Group = -> [C_element024,Cl_element004]
  conduct = 2
  density = 1
  expand = 3
  formula = G4_CARBON_TETRACHLORIDE
  name = G4_CARBON_TETRACHLORIDE
  specific = 4
FEATURE [App::DocumentObjectGroupPython] C_element025  label="C_element : 012"  # scripted group (container) (typed FeaturePython)
  n = 6
  ref = C_element
FEATURE [App::DocumentObjectGroupPython] H_element021  label="H_element : 012"  # scripted group (container) (typed FeaturePython)
  n = 10
  ref = H_element
FEATURE [App::DocumentObjectGroupPython] O_element026  label="O_element : 5"  # scripted group (container) (typed FeaturePython)
  n = 5
  ref = O_element
FEATURE [App::DocumentObjectGroupPython] G4_CELLULOSE_CELLOPHANE  # scripted group (container) (typed FeaturePython)
  Dunit = g/cm3
  Dvalue = 1.42
  Group = -> [C_element025,H_element021,O_element026]
  conduct = 2
  density = 1
  expand = 3
  formula = G4_CELLULOSE_CELLOPHANE
  name = G4_CELLULOSE_CELLOPHANE
  specific = 4
FEATURE [App::DocumentObjectGroupPython] H_element022  label="H_element : 0.067"  # scripted group (container) (typed FeaturePython)
  n = 0.067125
FEATURE [App::DocumentObjectGroupPython] C_element026  label="C_element : 0.545"  # scripted group (container) (typed FeaturePython)
  n = 0.545403
FEATURE [App::DocumentObjectGroupPython] O_element027  label="O_element : 0.387"  # scripted group (container) (typed FeaturePython)
  n = 0.387472
FEATURE [App::DocumentObjectGroupPython] G4_CELLULOSE_BUTYRATE  # scripted group (container) (typed FeaturePython)
  Dunit = g/cm3
  Dvalue = 1.2
  Group = -> [H_element022,C_element026,O_element027]
  conduct = 2
  density = 1
  expand = 3
  formula = G4_CELLULOSE_BUTYRATE
  name = G4_CELLULOSE_BUTYRATE
  specific = 4
FEATURE [App::DocumentObjectGroupPython] H_element023  label="H_element : 0.029"  # scripted group (container) (typed FeaturePython)
  n = 0.029216
FEATURE [App::DocumentObjectGroupPython] C_element027  label="C_element : 0.271"  # scripted group (container) (typed FeaturePython)
  n = 0.271296
FEATURE [App::DocumentObjectGroupPython] N_element013  label="N_element : 0.121"  # scripted group (container) (typed FeaturePython)
  n = 0.121276
FEATURE [App::DocumentObjectGroupPython] O_element028  label="O_element : 0.578"  # scripted group (container) (typed FeaturePython)
  n = 0.578212
FEATURE [App::DocumentObjectGroupPython] G4_CELLULOSE_NITRATE  # scripted group (container) (typed FeaturePython)
  Dunit = g/cm3
  Dvalue = 1.49
  Group = -> [H_element023,C_element027,N_element013,O_element028]
  conduct = 2
  density = 1
  expand = 3
  formula = G4_CELLULOSE_NITRATE
  name = G4_CELLULOSE_NITRATE
  specific = 4
FEATURE [App::DocumentObjectGroupPython] H_element024  label="H_element : 0.108"  # scripted group (container) (typed FeaturePython)
  n = 0.107596
FEATURE [App::DocumentObjectGroupPython] N_element014  label="N_element : 0.001"  # scripted group (container) (typed FeaturePython)
  n = 0.0008
FEATURE [App::DocumentObjectGroupPython] O_element029  label="O_element : 0.875"  # scripted group (container) (typed FeaturePython)
  n = 0.874976
FEATURE [App::DocumentObjectGroupPython] S_element008  label="S_element : 0.015"  # scripted group (container) (typed FeaturePython)
  n = 0.014627
FEATURE [App::DocumentObjectGroupPython] Ce_element001  label="Ce_element : 0.002"  # scripted group (container) (typed FeaturePython)
  n = 0.002001
FEATURE [App::DocumentObjectGroupPython] G4_CERIC_SULFATE  # scripted group (container) (typed FeaturePython)
  Dunit = g/cm3
  Dvalue = 1.03
  Group = -> [H_element024,N_element014,O_element029,S_element008,Ce_element001]
  conduct = 2
  density = 1
  expand = 3
  formula = G4_CERIC_SULFATE
  name = G4_CERIC_SULFATE
  specific = 4
FEATURE [App::DocumentObjectGroupPython] Cs_element001  label="Cs_element : 1"  # scripted group (container) (typed FeaturePython)
  n = 1
  ref = Cs_element
FEATURE [App::DocumentObjectGroupPython] F_element006  label="F_element : 1"  # scripted group (container) (typed FeaturePython)
  n = 1
  ref = F_element
FEATURE [App::DocumentObjectGroupPython] G4_CESIUM_FLUORIDE  # scripted group (container) (typed FeaturePython)
  Dunit = g/cm3
  Dvalue = 4.115
  Group = -> [Cs_element001,F_element006]
  conduct = 2
  density = 1
  expand = 3
  formula = G4_CESIUM_FLUORIDE
  name = G4_CESIUM_FLUORIDE
  specific = 4
FEATURE [App::DocumentObjectGroupPython] Cs_element002  label="Cs_element : 002"  # scripted group (container) (typed FeaturePython)
  n = 1
  ref = Cs_element
FEATURE [App::DocumentObjectGroupPython] I_element001  label="I_element : 1"  # scripted group (container) (typed FeaturePython)
  n = 1
  ref = I_element
FEATURE [App::DocumentObjectGroupPython] G4_CESIUM_IODIDE  # scripted group (container) (typed FeaturePython)
  Dunit = g/cm3
  Dvalue = 4.51
  Group = -> [Cs_element002,I_element001]
  conduct = 2
  density = 1
  expand = 3
  formula = G4_CESIUM_IODIDE
  name = G4_CESIUM_IODIDE
  specific = 4
FEATURE [App::DocumentObjectGroupPython] C_element028  label="C_element : 013"  # scripted group (container) (typed FeaturePython)
  n = 6
  ref = C_element
FEATURE [App::DocumentObjectGroupPython] H_element025  label="H_element : 013"  # scripted group (container) (typed FeaturePython)
  n = 5
  ref = H_element
FEATURE [App::DocumentObjectGroupPython] Cl_element005  label="Cl_element : 1"  # scripted group (container) (typed FeaturePython)
  n = 1
  ref = Cl_element
FEATURE [App::DocumentObjectGroupPython] G4_CHLOROBENZENE  # scripted group (container) (typed FeaturePython)
  Dunit = g/cm3
  Dvalue = 1.1058
  Group = -> [C_element028,H_element025,Cl_element005]
  conduct = 2
  density = 1
  expand = 3
  formula = G4_CHLOROBENZENE
  name = G4_CHLOROBENZENE
  specific = 4
FEATURE [App::DocumentObjectGroupPython] C_element029  label="C_element : 014"  # scripted group (container) (typed FeaturePython)
  n = 1
  ref = C_element
FEATURE [App::DocumentObjectGroupPython] H_element026  label="H_element : 1"  # scripted group (container) (typed FeaturePython)
  n = 1
  ref = H_element
FEATURE [App::DocumentObjectGroupPython] Cl_element006  label="Cl_element : 3"  # scripted group (container) (typed FeaturePython)
  n = 3
  ref = Cl_element
FEATURE [App::DocumentObjectGroupPython] G4_CHLOROFORM  # scripted group (container) (typed FeaturePython)
  Dunit = g/cm3
  Dvalue = 1.4832
  Group = -> [C_element029,H_element026,Cl_element006]
  conduct = 2
  density = 1
  expand = 3
  formula = G4_CHLOROFORM
  name = G4_CHLOROFORM
  specific = 4
FEATURE [App::DocumentObjectGroupPython] H_element027  label="H_element : 0.010"  # scripted group (container) (typed FeaturePython)
  n = 0.01
FEATURE [App::DocumentObjectGroupPython] C_element030  label="C_element : 0.001"  # scripted group (container) (typed FeaturePython)
  n = 0.001
FEATURE [App::DocumentObjectGroupPython] O_element030  label="O_element : 0.529"  # scripted group (container) (typed FeaturePython)
  n = 0.529107
FEATURE [App::DocumentObjectGroupPython] Na_element005  label="Na_element : 0.016"  # scripted group (container) (typed FeaturePython)
  n = 0.016
FEATURE [App::DocumentObjectGroupPython] Mg_element003  label="Mg_element : 0.004"  # scripted group (container) (typed FeaturePython)
  n = 0.002
FEATURE [App::DocumentObjectGroupPython] Al_element002  label="Al_element : 0.034"  # scripted group (container) (typed FeaturePython)
  n = 0.033872
FEATURE [App::DocumentObjectGroupPython] Si_element002  label="Si_element : 0.337"  # scripted group (container) (typed FeaturePython)
  n = 0.337021
FEATURE [App::DocumentObjectGroupPython] K_element003  label="K_element : 0.013"  # scripted group (container) (typed FeaturePython)
  n = 0.013
FEATURE [App::DocumentObjectGroupPython] Ca_element010  label="Ca_element : 0.044"  # scripted group (container) (typed FeaturePython)
  n = 0.044
FEATURE [App::DocumentObjectGroupPython] Fe_element002  label="Fe_element : 0.014"  # scripted group (container) (typed FeaturePython)
  n = 0.014
FEATURE [App::DocumentObjectGroupPython] G4_CONCRETE  # scripted group (container) (typed FeaturePython)
  Dunit = g/cm3
  Dvalue = 2.3
  Group = -> [H_element027,C_element030,O_element030,Na_element005,Mg_element003,Al_element002,Si_element002,K_element003,Ca_element010,Fe_element002]
  conduct = 2
  density = 1
  expand = 3
  formula = G4_CONCRETE
  name = G4_CONCRETE
  specific = 4
FEATURE [App::DocumentObjectGroupPython] C_element031  label="C_element : 015"  # scripted group (container) (typed FeaturePython)
  n = 6
  ref = C_element
FEATURE [App::DocumentObjectGroupPython] H_element028  label="H_element : 12"  # scripted group (container) (typed FeaturePython)
  n = 12
  ref = H_element
FEATURE [App::DocumentObjectGroupPython] G4_CYCLOHEXANE  # scripted group (container) (typed FeaturePython)
  Dunit = g/cm3
  Dvalue = 0.779
  Group = -> [C_element031,H_element028]
  conduct = 2
  density = 1
  expand = 3
  formula = G4_CYCLOHEXANE
  name = G4_CYCLOHEXANE
  specific = 4
FEATURE [App::DocumentObjectGroupPython] C_element032  label="C_element : 016"  # scripted group (container) (typed FeaturePython)
  n = 6
  ref = C_element
FEATURE [App::DocumentObjectGroupPython] H_element029  label="H_element : 4"  # scripted group (container) (typed FeaturePython)
  n = 4
  ref = H_element
FEATURE [App::DocumentObjectGroupPython] Cl_element007  label="Cl_element : 2"  # scripted group (container) (typed FeaturePython)
  n = 2
  ref = Cl_element
FEATURE [App::DocumentObjectGroupPython] G4_1_2_DICHLOROBENZENE  label="G4_1.2-DICHLOROBENZENE"  # scripted group (container) (typed FeaturePython)
  Dunit = g/cm3
  Dvalue = 1.3048
  Group = -> [C_element032,H_element029,Cl_element007]
  conduct = 2
  density = 1
  expand = 3
  formula = G4_1.2-DICHLOROBENZENE
  name = G4_1.2-DICHLOROBENZENE
  specific = 4
FEATURE [App::DocumentObjectGroupPython] C_element033  label="C_element : 017"  # scripted group (container) (typed FeaturePython)
  n = 4
  ref = C_element
FEATURE [App::DocumentObjectGroupPython] H_element030  label="H_element : 8"  # scripted group (container) (typed FeaturePython)
  n = 8
  ref = H_element
FEATURE [App::DocumentObjectGroupPython] O_element031  label="O_element : 014"  # scripted group (container) (typed FeaturePython)
  n = 1
  ref = O_element
FEATURE [App::DocumentObjectGroupPython] Cl_element008  label="Cl_element : 005"  # scripted group (container) (typed FeaturePython)
  n = 2
  ref = Cl_element
FEATURE [App::DocumentObjectGroupPython] G4_DICHLORODIETHYL_ETHER  # scripted group (container) (typed FeaturePython)
  Dunit = g/cm3
  Dvalue = 1.2199
  Group = -> [C_element033,H_element030,O_element031,Cl_element008]
  conduct = 2
  density = 1
  expand = 3
  formula = G4_DICHLORODIETHYL_ETHER
  name = G4_DICHLORODIETHYL_ETHER
  specific = 4
FEATURE [App::DocumentObjectGroupPython] C_element034  label="C_element : 018"  # scripted group (container) (typed FeaturePython)
  n = 2
  ref = C_element
FEATURE [App::DocumentObjectGroupPython] H_element031  label="H_element : 014"  # scripted group (container) (typed FeaturePython)
  n = 4
  ref = H_element
FEATURE [App::DocumentObjectGroupPython] Cl_element009  label="Cl_element : 006"  # scripted group (container) (typed FeaturePython)
  n = 2
  ref = Cl_element
FEATURE [App::DocumentObjectGroupPython] G4_1_2_DICHLOROETHANE  label="G4_1.2-DICHLOROETHANE"  # scripted group (container) (typed FeaturePython)
  Dunit = g/cm3
  Dvalue = 1.2351
  Group = -> [C_element034,H_element031,Cl_element009]
  conduct = 2
  density = 1
  expand = 3
  formula = G4_1.2-DICHLOROETHANE
  name = G4_1.2-DICHLOROETHANE
  specific = 4
FEATURE [App::DocumentObjectGroupPython] C_element035  label="C_element : 019"  # scripted group (container) (typed FeaturePython)
  n = 4
  ref = C_element
FEATURE [App::DocumentObjectGroupPython] H_element032  label="H_element : 015"  # scripted group (container) (typed FeaturePython)
  n = 10
  ref = H_element
FEATURE [App::DocumentObjectGroupPython] O_element032  label="O_element : 015"  # scripted group (container) (typed FeaturePython)
  n = 1
  ref = O_element
FEATURE [App::DocumentObjectGroupPython] G4_DIETHYL_ETHER  # scripted group (container) (typed FeaturePython)
  Dunit = g/cm3
  Dvalue = 0.71378
  Group = -> [C_element035,H_element032,O_element032]
  conduct = 2
  density = 1
  expand = 3
  formula = G4_DIETHYL_ETHER
  name = G4_DIETHYL_ETHER
  specific = 4
FEATURE [App::DocumentObjectGroupPython] C_element036  label="C_element : 020"  # scripted group (container) (typed FeaturePython)
  n = 3
  ref = C_element
FEATURE [App::DocumentObjectGroupPython] H_element033  label="H_element : 016"  # scripted group (container) (typed FeaturePython)
  n = 7
  ref = H_element
FEATURE [App::DocumentObjectGroupPython] N_element015  label="N_element : 008"  # scripted group (container) (typed FeaturePython)
  n = 1
  ref = N_element
FEATURE [App::DocumentObjectGroupPython] O_element033  label="O_element : 016"  # scripted group (container) (typed FeaturePython)
  n = 1
  ref = O_element
FEATURE [App::DocumentObjectGroupPython] G4_N_N_DIMETHYL_FORMAMIDE  label="G4_N.N-DIMETHYL_FORMAMIDE"  # scripted group (container) (typed FeaturePython)
  Dunit = g/cm3
  Dvalue = 0.9487
  Group = -> [C_element036,H_element033,N_element015,O_element033]
  conduct = 2
  density = 1
  expand = 3
  formula = G4_N.N-DIMETHYL_FORMAMIDE
  name = G4_N.N-DIMETHYL_FORMAMIDE
  specific = 4
FEATURE [App::DocumentObjectGroupPython] C_element037  label="C_element : 021"  # scripted group (container) (typed FeaturePython)
  n = 2
  ref = C_element
FEATURE [App::DocumentObjectGroupPython] H_element034  label="H_element : 017"  # scripted group (container) (typed FeaturePython)
  n = 6
  ref = H_element
FEATURE [App::DocumentObjectGroupPython] O_element034  label="O_element : 017"  # scripted group (container) (typed FeaturePython)
  n = 1
  ref = O_element
FEATURE [App::DocumentObjectGroupPython] S_element009  label="S_element : 003"  # scripted group (container) (typed FeaturePython)
  n = 1
  ref = S_element
FEATURE [App::DocumentObjectGroupPython] G4_DIMETHYL_SULFOXIDE  # scripted group (container) (typed FeaturePython)
  Dunit = g/cm3
  Dvalue = 1.1014
  Group = -> [C_element037,H_element034,O_element034,S_element009]
  conduct = 2
  density = 1
  expand = 3
  formula = G4_DIMETHYL_SULFOXIDE
  name = G4_DIMETHYL_SULFOXIDE
  specific = 4
FEATURE [App::DocumentObjectGroupPython] C_element038  label="C_element : 022"  # scripted group (container) (typed FeaturePython)
  n = 2
  ref = C_element
FEATURE [App::DocumentObjectGroupPython] H_element035  label="H_element : 018"  # scripted group (container) (typed FeaturePython)
  n = 6
  ref = H_element
FEATURE [App::DocumentObjectGroupPython] G4_ETHANE  # scripted group (container) (typed FeaturePython)
  Dunit = g/cm3
  Dvalue = 0.00125324
  Group = -> [C_element038,H_element035]
  conduct = 2
  density = 1
  expand = 3
  formula = G4_ETHANE
  name = G4_ETHANE
  specific = 4
FEATURE [App::DocumentObjectGroupPython] C_element039  label="C_element : 023"  # scripted group (container) (typed FeaturePython)
  n = 2
  ref = C_element
FEATURE [App::DocumentObjectGroupPython] H_element036  label="H_element : 019"  # scripted group (container) (typed FeaturePython)
  n = 6
  ref = H_element
FEATURE [App::DocumentObjectGroupPython] O_element035  label="O_element : 018"  # scripted group (container) (typed FeaturePython)
  n = 1
  ref = O_element
FEATURE [App::DocumentObjectGroupPython] G4_ETHYL_ALCOHOL  # scripted group (container) (typed FeaturePython)
  Dunit = g/cm3
  Dvalue = 0.7893
  Group = -> [C_element039,H_element036,O_element035]
  conduct = 2
  density = 1
  expand = 3
  formula = G4_ETHYL_ALCOHOL
  name = G4_ETHYL_ALCOHOL
  specific = 4
FEATURE [App::DocumentObjectGroupPython] H_element037  label="H_element : 0.090"  # scripted group (container) (typed FeaturePython)
  n = 0.090027
FEATURE [App::DocumentObjectGroupPython] C_element040  label="C_element : 0.585"  # scripted group (container) (typed FeaturePython)
  n = 0.585182
FEATURE [App::DocumentObjectGroupPython] O_element036  label="O_element : 0.325"  # scripted group (container) (typed FeaturePython)
  n = 0.324791
FEATURE [App::DocumentObjectGroupPython] G4_ETHYL_CELLULOSE  # scripted group (container) (typed FeaturePython)
  Dunit = g/cm3
  Dvalue = 1.13
  Group = -> [H_element037,C_element040,O_element036]
  conduct = 2
  density = 1
  expand = 3
  formula = G4_ETHYL_CELLULOSE
  name = G4_ETHYL_CELLULOSE
  specific = 4
FEATURE [App::DocumentObjectGroupPython] C_element041  label="C_element : 024"  # scripted group (container) (typed FeaturePython)
  n = 2
  ref = C_element
FEATURE [App::DocumentObjectGroupPython] H_element038  label="H_element : 020"  # scripted group (container) (typed FeaturePython)
  n = 4
  ref = H_element
FEATURE [App::DocumentObjectGroupPython] G4_ETHYLENE  # scripted group (container) (typed FeaturePython)
  Dunit = g/cm3
  Dvalue = 0.00117497
  Group = -> [C_element041,H_element038]
  conduct = 2
  density = 1
  expand = 3
  formula = G4_ETHYLENE
  name = G4_ETHYLENE
  specific = 4
FEATURE [App::DocumentObjectGroupPython] H_element039  label="H_element : 0.096"  # scripted group (container) (typed FeaturePython)
  n = 0.096
FEATURE [App::DocumentObjectGroupPython] C_element042  label="C_element : 0.195"  # scripted group (container) (typed FeaturePython)
  n = 0.195
FEATURE [App::DocumentObjectGroupPython] N_element016  label="N_element : 0.057"  # scripted group (container) (typed FeaturePython)
  n = 0.057
FEATURE [App::DocumentObjectGroupPython] O_element037  label="O_element : 0.646"  # scripted group (container) (typed FeaturePython)
  n = 0.646
FEATURE [App::DocumentObjectGroupPython] Na_element006  label="Na_element : 0.017"  # scripted group (container) (typed FeaturePython)
  n = 0.001
FEATURE [App::DocumentObjectGroupPython] P_element005  label="P_element : 0.104"  # scripted group (container) (typed FeaturePython)
  n = 0.001
FEATURE [App::DocumentObjectGroupPython] S_element010  label="S_element : 0.016"  # scripted group (container) (typed FeaturePython)
  n = 0.003
FEATURE [App::DocumentObjectGroupPython] Cl_element010  label="Cl_element : 0.005"  # scripted group (container) (typed FeaturePython)
  n = 0.001
FEATURE [App::DocumentObjectGroupPython] G4_EYE_LENS_ICRP  # scripted group (container) (typed FeaturePython)
  Dunit = g/cm3
  Dvalue = 1.07
  Group = -> [H_element039,C_element042,N_element016,O_element037,Na_element006,P_element005,S_element010,Cl_element010]
  conduct = 2
  density = 1
  expand = 3
  formula = G4_EYE_LENS_ICRP
  name = G4_EYE_LENS_ICRP
  specific = 4
FEATURE [App::DocumentObjectGroupPython] Fe_element003  label="Fe_element : 2"  # scripted group (container) (typed FeaturePython)
  n = 2
  ref = Fe_element
FEATURE [App::DocumentObjectGroupPython] O_element038  label="O_element : 019"  # scripted group (container) (typed FeaturePython)
  n = 3
  ref = O_element
FEATURE [App::DocumentObjectGroupPython] G4_FERRIC_OXIDE  # scripted group (container) (typed FeaturePython)
  Dunit = g/cm3
  Dvalue = 5.2
  Group = -> [Fe_element003,O_element038]
  conduct = 2
  density = 1
  expand = 3
  formula = G4_FERRIC_OXIDE
  name = G4_FERRIC_OXIDE
  specific = 4
FEATURE [App::DocumentObjectGroupPython] Fe_element004  label="Fe_element : 1"  # scripted group (container) (typed FeaturePython)
  n = 1
  ref = Fe_element
FEATURE [App::DocumentObjectGroupPython] B_element003  label="B_element : 1"  # scripted group (container) (typed FeaturePython)
  n = 1
  ref = B_element
FEATURE [App::DocumentObjectGroupPython] G4_FERROBORIDE  # scripted group (container) (typed FeaturePython)
  Dunit = g/cm3
  Dvalue = 7.15
  Group = -> [Fe_element004,B_element003]
  conduct = 2
  density = 1
  expand = 3
  formula = G4_FERROBORIDE
  name = G4_FERROBORIDE
  specific = 4
FEATURE [App::DocumentObjectGroupPython] Fe_element005  label="Fe_element : 003"  # scripted group (container) (typed FeaturePython)
  n = 1
  ref = Fe_element
FEATURE [App::DocumentObjectGroupPython] O_element039  label="O_element : 020"  # scripted group (container) (typed FeaturePython)
  n = 1
  ref = O_element
FEATURE [App::DocumentObjectGroupPython] G4_FERROUS_OXIDE  # scripted group (container) (typed FeaturePython)
  Dunit = g/cm3
  Dvalue = 5.7
  Group = -> [Fe_element005,O_element039]
  conduct = 2
  density = 1
  expand = 3
  formula = G4_FERROUS_OXIDE
  name = G4_FERROUS_OXIDE
  specific = 4
FEATURE [App::DocumentObjectGroupPython] H_element040  label="H_element : 0.115"  # scripted group (container) (typed FeaturePython)
  n = 0.108259
FEATURE [App::DocumentObjectGroupPython] N_element017  label="N_element : 0.000"  # scripted group (container) (typed FeaturePython)
  n = 2.7e-05
FEATURE [App::DocumentObjectGroupPython] O_element040  label="O_element : 0.879"  # scripted group (container) (typed FeaturePython)
  n = 0.878636
FEATURE [App::DocumentObjectGroupPython] Na_element007  label="Na_element : 0.000"  # scripted group (container) (typed FeaturePython)
  n = 2.2e-05
FEATURE [App::DocumentObjectGroupPython] S_element011  label="S_element : 0.013"  # scripted group (container) (typed FeaturePython)
  n = 0.012968
FEATURE [App::DocumentObjectGroupPython] Cl_element011  label="Cl_element : 0.000"  # scripted group (container) (typed FeaturePython)
  n = 3.4e-05
FEATURE [App::DocumentObjectGroupPython] Fe_element006  label="Fe_element : 0.000"  # scripted group (container) (typed FeaturePython)
  n = 5.4e-05
FEATURE [App::DocumentObjectGroupPython] G4_FERROUS_SULFATE  # scripted group (container) (typed FeaturePython)
  Dunit = g/cm3
  Dvalue = 1.024
  Group = -> [H_element040,N_element017,O_element040,Na_element007,S_element011,Cl_element011,Fe_element006]
  conduct = 2
  density = 1
  expand = 3
  formula = G4_FERROUS_SULFATE
  name = G4_FERROUS_SULFATE
  specific = 4
FEATURE [App::DocumentObjectGroupPython] C_element043  label="C_element : 0.099"  # scripted group (container) (typed FeaturePython)
  n = 0.099335
FEATURE [App::DocumentObjectGroupPython] F_element007  label="F_element : 0.314"  # scripted group (container) (typed FeaturePython)
  n = 0.314247
FEATURE [App::DocumentObjectGroupPython] Cl_element012  label="Cl_element : 0.586"  # scripted group (container) (typed FeaturePython)
  n = 0.586418
FEATURE [App::DocumentObjectGroupPython] G4_FREON_12  label="G4_FREON-12"  # scripted group (container) (typed FeaturePython)
  Dunit = g/cm3
  Dvalue = 1.12
  Group = -> [C_element043,F_element007,Cl_element012]
  conduct = 2
  density = 1
  expand = 3
  formula = G4_FREON-12
  name = G4_FREON-12
  specific = 4
FEATURE [App::DocumentObjectGroupPython] C_element044  label="C_element : 0.057"  # scripted group (container) (typed FeaturePython)
  n = 0.057245
FEATURE [App::DocumentObjectGroupPython] F_element008  label="F_element : 0.181"  # scripted group (container) (typed FeaturePython)
  n = 0.181096
FEATURE [App::DocumentObjectGroupPython] Br_element001  label="Br_element : 0.762"  # scripted group (container) (typed FeaturePython)
  n = 0.761659
FEATURE [App::DocumentObjectGroupPython] G4_FREON_12B2  label="G4_FREON-12B2"  # scripted group (container) (typed FeaturePython)
  Dunit = g/cm3
  Dvalue = 1.8
  Group = -> [C_element044,F_element008,Br_element001]
  conduct = 2
  density = 1
  expand = 3
  formula = G4_FREON-12B2
  name = G4_FREON-12B2
  specific = 4
FEATURE [App::DocumentObjectGroupPython] C_element045  label="C_element : 0.115"  # scripted group (container) (typed FeaturePython)
  n = 0.114983
FEATURE [App::DocumentObjectGroupPython] F_element009  label="F_element : 0.546"  # scripted group (container) (typed FeaturePython)
  n = 0.545621
FEATURE [App::DocumentObjectGroupPython] Cl_element013  label="Cl_element : 0.339"  # scripted group (container) (typed FeaturePython)
  n = 0.339396
FEATURE [App::DocumentObjectGroupPython] G4_FREON_13  label="G4_FREON-13"  # scripted group (container) (typed FeaturePython)
  Dunit = g/cm3
  Dvalue = 0.95
  Group = -> [C_element045,F_element009,Cl_element013]
  conduct = 2
  density = 1
  expand = 3
  formula = G4_FREON-13
  name = G4_FREON-13
  specific = 4
FEATURE [App::DocumentObjectGroupPython] C_element046  label="C_element : 025"  # scripted group (container) (typed FeaturePython)
  n = 1
  ref = C_element
FEATURE [App::DocumentObjectGroupPython] F_element010  label="F_element : 3"  # scripted group (container) (typed FeaturePython)
  n = 3
  ref = F_element
FEATURE [App::DocumentObjectGroupPython] Br_element002  label="Br_element : 1"  # scripted group (container) (typed FeaturePython)
  n = 1
  ref = Br_element
FEATURE [App::DocumentObjectGroupPython] G4_FREON_13B1  label="G4_FREON-13B1"  # scripted group (container) (typed FeaturePython)
  Dunit = g/cm3
  Dvalue = 1.5
  Group = -> [C_element046,F_element010,Br_element002]
  conduct = 2
  density = 1
  expand = 3
  formula = G4_FREON-13B1
  name = G4_FREON-13B1
  specific = 4
FEATURE [App::DocumentObjectGroupPython] C_element047  label="C_element : 0.061"  # scripted group (container) (typed FeaturePython)
  n = 0.061309
FEATURE [App::DocumentObjectGroupPython] F_element011  label="F_element : 0.291"  # scripted group (container) (typed FeaturePython)
  n = 0.290924
FEATURE [App::DocumentObjectGroupPython] I_element002  label="I_element : 0.648"  # scripted group (container) (typed FeaturePython)
  n = 0.647767
FEATURE [App::DocumentObjectGroupPython] G4_FREON_13I1  label="G4_FREON-13I1"  # scripted group (container) (typed FeaturePython)
  Dunit = g/cm3
  Dvalue = 1.8
  Group = -> [C_element047,F_element011,I_element002]
  conduct = 2
  density = 1
  expand = 3
  formula = G4_FREON-13I1
  name = G4_FREON-13I1
  specific = 4
FEATURE [App::DocumentObjectGroupPython] Gd_element001  label="Gd_element : 2"  # scripted group (container) (typed FeaturePython)
  n = 2
  ref = Gd_element
FEATURE [App::DocumentObjectGroupPython] O_element041  label="O_element : 021"  # scripted group (container) (typed FeaturePython)
  n = 2
  ref = O_element
FEATURE [App::DocumentObjectGroupPython] S_element012  label="S_element : 004"  # scripted group (container) (typed FeaturePython)
  n = 1
  ref = S_element
FEATURE [App::DocumentObjectGroupPython] G4_GADOLINIUM_OXYSULFIDE  # scripted group (container) (typed FeaturePython)
  Dunit = g/cm3
  Dvalue = 7.44
  Group = -> [Gd_element001,O_element041,S_element012]
  conduct = 2
  density = 1
  expand = 3
  formula = G4_GADOLINIUM_OXYSULFIDE
  name = G4_GADOLINIUM_OXYSULFIDE
  specific = 4
FEATURE [App::DocumentObjectGroupPython] Ga_element001  label="Ga_element : 1"  # scripted group (container) (typed FeaturePython)
  n = 1
  ref = Ga_element
FEATURE [App::DocumentObjectGroupPython] As_element001  label="As_element : 1"  # scripted group (container) (typed FeaturePython)
  n = 1
  ref = As_element
FEATURE [App::DocumentObjectGroupPython] G4_GALLIUM_ARSENIDE  # scripted group (container) (typed FeaturePython)
  Dunit = g/cm3
  Dvalue = 5.31
  Group = -> [Ga_element001,As_element001]
  conduct = 2
  density = 1
  expand = 3
  formula = G4_GALLIUM_ARSENIDE
  name = G4_GALLIUM_ARSENIDE
  specific = 4
FEATURE [App::DocumentObjectGroupPython] H_element041  label="H_element : 0.081"  # scripted group (container) (typed FeaturePython)
  n = 0.08118
FEATURE [App::DocumentObjectGroupPython] C_element048  label="C_element : 0.416"  # scripted group (container) (typed FeaturePython)
  n = 0.41606
FEATURE [App::DocumentObjectGroupPython] N_element018  label="N_element : 0.111"  # scripted group (container) (typed FeaturePython)
  n = 0.11124
FEATURE [App::DocumentObjectGroupPython] O_element042  label="O_element : 0.381"  # scripted group (container) (typed FeaturePython)
  n = 0.38064
FEATURE [App::DocumentObjectGroupPython] S_element013  label="S_element : 0.011"  # scripted group (container) (typed FeaturePython)
  n = 0.01088
FEATURE [App::DocumentObjectGroupPython] G4_GEL_PHOTO_EMULSION  # scripted group (container) (typed FeaturePython)
  Dunit = g/cm3
  Dvalue = 1.2914
  Group = -> [H_element041,C_element048,N_element018,O_element042,S_element013]
  conduct = 2
  density = 1
  expand = 3
  formula = G4_GEL_PHOTO_EMULSION
  name = G4_GEL_PHOTO_EMULSION
  specific = 4
FEATURE [App::DocumentObjectGroupPython] B_element004  label="B_element : 0.040"  # scripted group (container) (typed FeaturePython)
  n = 0.0400639
FEATURE [App::DocumentObjectGroupPython] O_element043  label="O_element : 0.540"  # scripted group (container) (typed FeaturePython)
  n = 0.539561
FEATURE [App::DocumentObjectGroupPython] Na_element008  label="Na_element : 0.028"  # scripted group (container) (typed FeaturePython)
  n = 0.0281909
FEATURE [App::DocumentObjectGroupPython] Al_element003  label="Al_element : 0.012"  # scripted group (container) (typed FeaturePython)
  n = 0.011644
FEATURE [App::DocumentObjectGroupPython] Si_element003  label="Si_element : 0.377"  # scripted group (container) (typed FeaturePython)
  n = 0.377219
FEATURE [App::DocumentObjectGroupPython] K_element004  label="K_element : 0.014"  # scripted group (container) (typed FeaturePython)
  n = 0.00332099
FEATURE [App::DocumentObjectGroupPython] G4_Pyrex_Glass  # scripted group (container) (typed FeaturePython)
  Dunit = g/cm3
  Dvalue = 2.23
  Group = -> [B_element004,O_element043,Na_element008,Al_element003,Si_element003,K_element004]
  conduct = 2
  density = 1
  expand = 3
  formula = G4_Pyrex_Glass
  name = G4_Pyrex_Glass
  specific = 4
FEATURE [App::DocumentObjectGroupPython] O_element044  label="O_element : 0.156"  # scripted group (container) (typed FeaturePython)
  n = 0.156453
FEATURE [App::DocumentObjectGroupPython] Si_element004  label="Si_element : 0.081"  # scripted group (container) (typed FeaturePython)
  n = 0.080866
FEATURE [App::DocumentObjectGroupPython] Ti_element001  label="Ti_element : 0.008"  # scripted group (container) (typed FeaturePython)
  n = 0.008092
FEATURE [App::DocumentObjectGroupPython] As_element002  label="As_element : 0.003"  # scripted group (container) (typed FeaturePython)
  n = 0.002651
FEATURE [App::DocumentObjectGroupPython] Pb_element001  label="Pb_element : 0.752"  # scripted group (container) (typed FeaturePython)
  n = 0.751938
FEATURE [App::DocumentObjectGroupPython] G4_GLASS_LEAD  # scripted group (container) (typed FeaturePython)
  Dunit = g/cm3
  Dvalue = 6.22
  Group = -> [O_element044,Si_element004,Ti_element001,As_element002,Pb_element001]
  conduct = 2
  density = 1
  expand = 3
  formula = G4_GLASS_LEAD
  name = G4_GLASS_LEAD
  specific = 4
FEATURE [App::DocumentObjectGroupPython] O_element045  label="O_element : 0.460"  # scripted group (container) (typed FeaturePython)
  n = 0.4598
FEATURE [App::DocumentObjectGroupPython] Na_element009  label="Na_element : 0.096"  # scripted group (container) (typed FeaturePython)
  n = 0.0964411
FEATURE [App::DocumentObjectGroupPython] Si_element005  label="Si_element : 0.378"  # scripted group (container) (typed FeaturePython)
  n = 0.336553
FEATURE [App::DocumentObjectGroupPython] Ca_element011  label="Ca_element : 0.107"  # scripted group (container) (typed FeaturePython)
  n = 0.107205
FEATURE [App::DocumentObjectGroupPython] G4_GLASS_PLATE  # scripted group (container) (typed FeaturePython)
  Dunit = g/cm3
  Dvalue = 2.4
  Group = -> [O_element045,Na_element009,Si_element005,Ca_element011]
  conduct = 2
  density = 1
  expand = 3
  formula = G4_GLASS_PLATE
  name = G4_GLASS_PLATE
  specific = 4
FEATURE [App::DocumentObjectGroupPython] C_element049  label="C_element : 026"  # scripted group (container) (typed FeaturePython)
  n = 5
  ref = C_element
FEATURE [App::DocumentObjectGroupPython] H_element042  label="H_element : 021"  # scripted group (container) (typed FeaturePython)
  n = 10
  ref = H_element
FEATURE [App::DocumentObjectGroupPython] N_element019  label="N_element : 2"  # scripted group (container) (typed FeaturePython)
  n = 2
  ref = N_element
FEATURE [App::DocumentObjectGroupPython] O_element046  label="O_element : 022"  # scripted group (container) (typed FeaturePython)
  n = 3
  ref = O_element
FEATURE [App::DocumentObjectGroupPython] G4_GLUTAMINE  # scripted group (container) (typed FeaturePython)
  Dunit = g/cm3
  Dvalue = 1.46
  Group = -> [C_element049,H_element042,N_element019,O_element046]
  conduct = 2
  density = 1
  expand = 3
  formula = G4_GLUTAMINE
  name = G4_GLUTAMINE
  specific = 4
FEATURE [App::DocumentObjectGroupPython] C_element050  label="C_element : 027"  # scripted group (container) (typed FeaturePython)
  n = 3
  ref = C_element
FEATURE [App::DocumentObjectGroupPython] H_element043  label="H_element : 022"  # scripted group (container) (typed FeaturePython)
  n = 8
  ref = H_element
FEATURE [App::DocumentObjectGroupPython] O_element047  label="O_element : 023"  # scripted group (container) (typed FeaturePython)
  n = 3
  ref = O_element
FEATURE [App::DocumentObjectGroupPython] G4_GLYCEROL  # scripted group (container) (typed FeaturePython)
  Dunit = g/cm3
  Dvalue = 1.2613
  Group = -> [C_element050,H_element043,O_element047]
  conduct = 2
  density = 1
  expand = 3
  formula = G4_GLYCEROL
  name = G4_GLYCEROL
  specific = 4
FEATURE [App::DocumentObjectGroupPython] C_element051  label="C_element : 028"  # scripted group (container) (typed FeaturePython)
  n = 5
  ref = C_element
FEATURE [App::DocumentObjectGroupPython] H_element044  label="H_element : 023"  # scripted group (container) (typed FeaturePython)
  n = 5
  ref = H_element
FEATURE [App::DocumentObjectGroupPython] N_element020  label="N_element : 009"  # scripted group (container) (typed FeaturePython)
  n = 5
  ref = N_element
FEATURE [App::DocumentObjectGroupPython] O_element048  label="O_element : 024"  # scripted group (container) (typed FeaturePython)
  n = 1
  ref = O_element
FEATURE [App::DocumentObjectGroupPython] G4_GUANINE  # scripted group (container) (typed FeaturePython)
  Dunit = g/cm3
  Dvalue = 2.2
  Group = -> [C_element051,H_element044,N_element020,O_element048]
  conduct = 2
  density = 1
  expand = 3
  formula = G4_GUANINE
  name = G4_GUANINE
  specific = 4
FEATURE [App::DocumentObjectGroupPython] Ca_element012  label="Ca_element : 006"  # scripted group (container) (typed FeaturePython)
  n = 1
  ref = Ca_element
FEATURE [App::DocumentObjectGroupPython] S_element014  label="S_element : 005"  # scripted group (container) (typed FeaturePython)
  n = 1
  ref = S_element
FEATURE [App::DocumentObjectGroupPython] O_element049  label="O_element : 6"  # scripted group (container) (typed FeaturePython)
  n = 6
  ref = O_element
FEATURE [App::DocumentObjectGroupPython] H_element045  label="H_element : 024"  # scripted group (container) (typed FeaturePython)
  n = 4
  ref = H_element
FEATURE [App::DocumentObjectGroupPython] G4_GYPSUM  # scripted group (container) (typed FeaturePython)
  Dunit = g/cm3
  Dvalue = 2.32
  Group = -> [Ca_element012,S_element014,O_element049,H_element045]
  conduct = 2
  density = 1
  expand = 3
  formula = G4_GYPSUM
  name = G4_GYPSUM
  specific = 4
FEATURE [App::DocumentObjectGroupPython] C_element052  label="C_element : 7"  # scripted group (container) (typed FeaturePython)
  n = 7
  ref = C_element
FEATURE [App::DocumentObjectGroupPython] H_element046  label="H_element : 16"  # scripted group (container) (typed FeaturePython)
  n = 16
  ref = H_element
FEATURE [App::DocumentObjectGroupPython] G4_N_HEPTANE  label="G4_N-HEPTANE"  # scripted group (container) (typed FeaturePython)
  Dunit = g/cm3
  Dvalue = 0.68376
  Group = -> [C_element052,H_element046]
  conduct = 2
  density = 1
  expand = 3
  formula = G4_N-HEPTANE
  name = G4_N-HEPTANE
  specific = 4
FEATURE [App::DocumentObjectGroupPython] C_element053  label="C_element : 029"  # scripted group (container) (typed FeaturePython)
  n = 6
  ref = C_element
FEATURE [App::DocumentObjectGroupPython] H_element047  label="H_element : 14"  # scripted group (container) (typed FeaturePython)
  n = 14
  ref = H_element
FEATURE [App::DocumentObjectGroupPython] G4_N_HEXANE  label="G4_N-HEXANE"  # scripted group (container) (typed FeaturePython)
  Dunit = g/cm3
  Dvalue = 0.6603
  Group = -> [C_element053,H_element047]
  conduct = 2
  density = 1
  expand = 3
  formula = G4_N-HEXANE
  name = G4_N-HEXANE
  specific = 4
FEATURE [App::DocumentObjectGroupPython] C_element054  label="C_element : 22"  # scripted group (container) (typed FeaturePython)
  n = 22
  ref = C_element
FEATURE [App::DocumentObjectGroupPython] H_element048  label="H_element : 025"  # scripted group (container) (typed FeaturePython)
  n = 10
  ref = H_element
FEATURE [App::DocumentObjectGroupPython] N_element021  label="N_element : 010"  # scripted group (container) (typed FeaturePython)
  n = 2
  ref = N_element
FEATURE [App::DocumentObjectGroupPython] O_element050  label="O_element : 025"  # scripted group (container) (typed FeaturePython)
  n = 5
  ref = O_element
FEATURE [App::DocumentObjectGroupPython] G4_KAPTON  # scripted group (container) (typed FeaturePython)
  Dunit = g/cm3
  Dvalue = 1.42
  Group = -> [C_element054,H_element048,N_element021,O_element050]
  conduct = 2
  density = 1
  expand = 3
  formula = G4_KAPTON
  name = G4_KAPTON
  specific = 4
FEATURE [App::DocumentObjectGroupPython] La_element001  label="La_element : 1"  # scripted group (container) (typed FeaturePython)
  n = 1
  ref = La_element
FEATURE [App::DocumentObjectGroupPython] Br_element003  label="Br_element : 002"  # scripted group (container) (typed FeaturePython)
  n = 1
  ref = Br_element
FEATURE [App::DocumentObjectGroupPython] O_element051  label="O_element : 026"  # scripted group (container) (typed FeaturePython)
  n = 1
  ref = O_element
FEATURE [App::DocumentObjectGroupPython] G4_LANTHANUM_OXYBROMIDE  # scripted group (container) (typed FeaturePython)
  Dunit = g/cm3
  Dvalue = 6.28
  Group = -> [La_element001,Br_element003,O_element051]
  conduct = 2
  density = 1
  expand = 3
  formula = G4_LANTHANUM_OXYBROMIDE
  name = G4_LANTHANUM_OXYBROMIDE
  specific = 4
FEATURE [App::DocumentObjectGroupPython] La_element002  label="La_element : 2"  # scripted group (container) (typed FeaturePython)
  n = 2
  ref = La_element
FEATURE [App::DocumentObjectGroupPython] O_element052  label="O_element : 027"  # scripted group (container) (typed FeaturePython)
  n = 2
  ref = O_element
FEATURE [App::DocumentObjectGroupPython] S_element015  label="S_element : 006"  # scripted group (container) (typed FeaturePython)
  n = 1
  ref = S_element
FEATURE [App::DocumentObjectGroupPython] G4_LANTHANUM_OXYSULFIDE  # scripted group (container) (typed FeaturePython)
  Dunit = g/cm3
  Dvalue = 5.86
  Group = -> [La_element002,O_element052,S_element015]
  conduct = 2
  density = 1
  expand = 3
  formula = G4_LANTHANUM_OXYSULFIDE
  name = G4_LANTHANUM_OXYSULFIDE
  specific = 4
FEATURE [App::DocumentObjectGroupPython] O_element053  label="O_element : 0.072"  # scripted group (container) (typed FeaturePython)
  n = 0.071682
FEATURE [App::DocumentObjectGroupPython] Pb_element002  label="Pb_element : 0.928"  # scripted group (container) (typed FeaturePython)
  n = 0.928318
FEATURE [App::DocumentObjectGroupPython] G4_LEAD_OXIDE  # scripted group (container) (typed FeaturePython)
  Dunit = g/cm3
  Dvalue = 9.53
  Group = -> [O_element053,Pb_element002]
  conduct = 2
  density = 1
  expand = 3
  formula = G4_LEAD_OXIDE
  name = G4_LEAD_OXIDE
  specific = 4
FEATURE [App::DocumentObjectGroupPython] Li_element001  label="Li_element : 1"  # scripted group (container) (typed FeaturePython)
  n = 1
  ref = Li_element
FEATURE [App::DocumentObjectGroupPython] N_element022  label="N_element : 011"  # scripted group (container) (typed FeaturePython)
  n = 1
  ref = N_element
FEATURE [App::DocumentObjectGroupPython] H_element049  label="H_element : 026"  # scripted group (container) (typed FeaturePython)
  n = 2
  ref = H_element
FEATURE [App::DocumentObjectGroupPython] G4_LITHIUM_AMIDE  # scripted group (container) (typed FeaturePython)
  Dunit = g/cm3
  Dvalue = 1.178
  Group = -> [Li_element001,N_element022,H_element049]
  conduct = 2
  density = 1
  expand = 3
  formula = G4_LITHIUM_AMIDE
  name = G4_LITHIUM_AMIDE
  specific = 4
FEATURE [App::DocumentObjectGroupPython] Li_element002  label="Li_element : 2"  # scripted group (container) (typed FeaturePython)
  n = 2
  ref = Li_element
FEATURE [App::DocumentObjectGroupPython] C_element055  label="C_element : 030"  # scripted group (container) (typed FeaturePython)
  n = 1
  ref = C_element
FEATURE [App::DocumentObjectGroupPython] O_element054  label="O_element : 028"  # scripted group (container) (typed FeaturePython)
  n = 3
  ref = O_element
FEATURE [App::DocumentObjectGroupPython] G4_LITHIUM_CARBONATE  # scripted group (container) (typed FeaturePython)
  Dunit = g/cm3
  Dvalue = 2.11
  Group = -> [Li_element002,C_element055,O_element054]
  conduct = 2
  density = 1
  expand = 3
  formula = G4_LITHIUM_CARBONATE
  name = G4_LITHIUM_CARBONATE
  specific = 4
FEATURE [App::DocumentObjectGroupPython] Li_element003  label="Li_element : 003"  # scripted group (container) (typed FeaturePython)
  n = 1
  ref = Li_element
FEATURE [App::DocumentObjectGroupPython] F_element012  label="F_element : 004"  # scripted group (container) (typed FeaturePython)
  n = 1
  ref = F_element
FEATURE [App::DocumentObjectGroupPython] G4_LITHIUM_FLUORIDE  # scripted group (container) (typed FeaturePython)
  Dunit = g/cm3
  Dvalue = 2.635
  Group = -> [Li_element003,F_element012]
  conduct = 2
  density = 1
  expand = 3
  formula = G4_LITHIUM_FLUORIDE
  name = G4_LITHIUM_FLUORIDE
  specific = 4
FEATURE [App::DocumentObjectGroupPython] Li_element004  label="Li_element : 004"  # scripted group (container) (typed FeaturePython)
  n = 1
  ref = Li_element
FEATURE [App::DocumentObjectGroupPython] H_element050  label="H_element : 027"  # scripted group (container) (typed FeaturePython)
  n = 1
  ref = H_element
FEATURE [App::DocumentObjectGroupPython] G4_LITHIUM_HYDRIDE  # scripted group (container) (typed FeaturePython)
  Dunit = g/cm3
  Dvalue = 0.82
  Group = -> [Li_element004,H_element050]
  conduct = 2
  density = 1
  expand = 3
  formula = G4_LITHIUM_HYDRIDE
  name = G4_LITHIUM_HYDRIDE
  specific = 4
FEATURE [App::DocumentObjectGroupPython] Li_element005  label="Li_element : 005"  # scripted group (container) (typed FeaturePython)
  n = 1
  ref = Li_element
FEATURE [App::DocumentObjectGroupPython] I_element003  label="I_element : 002"  # scripted group (container) (typed FeaturePython)
  n = 1
  ref = I_element
FEATURE [App::DocumentObjectGroupPython] G4_LITHIUM_IODIDE  # scripted group (container) (typed FeaturePython)
  Dunit = g/cm3
  Dvalue = 3.494
  Group = -> [Li_element005,I_element003]
  conduct = 2
  density = 1
  expand = 3
  formula = G4_LITHIUM_IODIDE
  name = G4_LITHIUM_IODIDE
  specific = 4
FEATURE [App::DocumentObjectGroupPython] Li_element006  label="Li_element : 006"  # scripted group (container) (typed FeaturePython)
  n = 2
  ref = Li_element
FEATURE [App::DocumentObjectGroupPython] O_element055  label="O_element : 029"  # scripted group (container) (typed FeaturePython)
  n = 1
  ref = O_element
FEATURE [App::DocumentObjectGroupPython] G4_LITHIUM_OXIDE  # scripted group (container) (typed FeaturePython)
  Dunit = g/cm3
  Dvalue = 2.013
  Group = -> [Li_element006,O_element055]
  conduct = 2
  density = 1
  expand = 3
  formula = G4_LITHIUM_OXIDE
  name = G4_LITHIUM_OXIDE
  specific = 4
FEATURE [App::DocumentObjectGroupPython] Li_element007  label="Li_element : 007"  # scripted group (container) (typed FeaturePython)
  n = 2
  ref = Li_element
FEATURE [App::DocumentObjectGroupPython] B_element005  label="B_element : 005"  # scripted group (container) (typed FeaturePython)
  n = 4
  ref = B_element
FEATURE [App::DocumentObjectGroupPython] O_element056  label="O_element : 7"  # scripted group (container) (typed FeaturePython)
  n = 7
  ref = O_element
FEATURE [App::DocumentObjectGroupPython] G4_LITHIUM_TETRABORATE  # scripted group (container) (typed FeaturePython)
  Dunit = g/cm3
  Dvalue = 2.44
  Group = -> [Li_element007,B_element005,O_element056]
  conduct = 2
  density = 1
  expand = 3
  formula = G4_LITHIUM_TETRABORATE
  name = G4_LITHIUM_TETRABORATE
  specific = 4
FEATURE [App::DocumentObjectGroupPython] H_element051  label="H_element : 0.105"  # scripted group (container) (typed FeaturePython)
  n = 0.105
FEATURE [App::DocumentObjectGroupPython] C_element056  label="C_element : 0.083"  # scripted group (container) (typed FeaturePython)
  n = 0.083
FEATURE [App::DocumentObjectGroupPython] N_element023  label="N_element : 0.023"  # scripted group (container) (typed FeaturePython)
  n = 0.023
FEATURE [App::DocumentObjectGroupPython] O_element057  label="O_element : 0.779"  # scripted group (container) (typed FeaturePython)
  n = 0.779
FEATURE [App::DocumentObjectGroupPython] Na_element010  label="Na_element : 0.097"  # scripted group (container) (typed FeaturePython)
  n = 0.002
FEATURE [App::DocumentObjectGroupPython] P_element006  label="P_element : 0.105"  # scripted group (container) (typed FeaturePython)
  n = 0.001
FEATURE [App::DocumentObjectGroupPython] S_element016  label="S_element : 0.017"  # scripted group (container) (typed FeaturePython)
  n = 0.002
FEATURE [App::DocumentObjectGroupPython] Cl_element014  label="Cl_element : 0.587"  # scripted group (container) (typed FeaturePython)
  n = 0.003
FEATURE [App::DocumentObjectGroupPython] K_element005  label="K_element : 0.015"  # scripted group (container) (typed FeaturePython)
  n = 0.002
FEATURE [App::DocumentObjectGroupPython] G4_LUNG_ICRP  # scripted group (container) (typed FeaturePython)
  Dunit = g/cm3
  Dvalue = 1.04
  Group = -> [H_element051,C_element056,N_element023,O_element057,Na_element010,P_element006,S_element016,Cl_element014,K_element005]
  conduct = 2
  density = 1
  expand = 3
  formula = G4_LUNG_ICRP
  name = G4_LUNG_ICRP
  specific = 4
FEATURE [App::DocumentObjectGroupPython] H_element052  label="H_element : 0.116"  # scripted group (container) (typed FeaturePython)
  n = 0.114318
FEATURE [App::DocumentObjectGroupPython] C_element057  label="C_element : 0.656"  # scripted group (container) (typed FeaturePython)
  n = 0.655824
FEATURE [App::DocumentObjectGroupPython] O_element058  label="O_element : 0.092"  # scripted group (container) (typed FeaturePython)
  n = 0.0921831
FEATURE [App::DocumentObjectGroupPython] Mg_element004  label="Mg_element : 0.135"  # scripted group (container) (typed FeaturePython)
  n = 0.134792
FEATURE [App::DocumentObjectGroupPython] Ca_element013  label="Ca_element : 0.003"  # scripted group (container) (typed FeaturePython)
  n = 0.002883
FEATURE [App::DocumentObjectGroupPython] G4_M3_WAX  # scripted group (container) (typed FeaturePython)
  Dunit = g/cm3
  Dvalue = 1.05
  Group = -> [H_element052,C_element057,O_element058,Mg_element004,Ca_element013]
  conduct = 2
  density = 1
  expand = 3
  formula = G4_M3_WAX
  name = G4_M3_WAX
  specific = 4
FEATURE [App::DocumentObjectGroupPython] Mg_element005  label="Mg_element : 1"  # scripted group (container) (typed FeaturePython)
  n = 1
  ref = Mg_element
FEATURE [App::DocumentObjectGroupPython] C_element058  label="C_element : 031"  # scripted group (container) (typed FeaturePython)
  n = 1
  ref = C_element
FEATURE [App::DocumentObjectGroupPython] O_element059  label="O_element : 030"  # scripted group (container) (typed FeaturePython)
  n = 3
  ref = O_element
FEATURE [App::DocumentObjectGroupPython] G4_MAGNESIUM_CARBONATE  # scripted group (container) (typed FeaturePython)
  Dunit = g/cm3
  Dvalue = 2.958
  Group = -> [Mg_element005,C_element058,O_element059]
  conduct = 2
  density = 1
  expand = 3
  formula = G4_MAGNESIUM_CARBONATE
  name = G4_MAGNESIUM_CARBONATE
  specific = 4
FEATURE [App::DocumentObjectGroupPython] Mg_element006  label="Mg_element : 002"  # scripted group (container) (typed FeaturePython)
  n = 1
  ref = Mg_element
FEATURE [App::DocumentObjectGroupPython] F_element013  label="F_element : 005"  # scripted group (container) (typed FeaturePython)
  n = 2
  ref = F_element
FEATURE [App::DocumentObjectGroupPython] G4_MAGNESIUM_FLUORIDE  # scripted group (container) (typed FeaturePython)
  Dunit = g/cm3
  Dvalue = 3
  Group = -> [Mg_element006,F_element013]
  conduct = 2
  density = 1
  expand = 3
  formula = G4_MAGNESIUM_FLUORIDE
  name = G4_MAGNESIUM_FLUORIDE
  specific = 4
FEATURE [App::DocumentObjectGroupPython] Mg_element007  label="Mg_element : 003"  # scripted group (container) (typed FeaturePython)
  n = 1
  ref = Mg_element
FEATURE [App::DocumentObjectGroupPython] O_element060  label="O_element : 031"  # scripted group (container) (typed FeaturePython)
  n = 1
  ref = O_element
FEATURE [App::DocumentObjectGroupPython] G4_MAGNESIUM_OXIDE  # scripted group (container) (typed FeaturePython)
  Dunit = g/cm3
  Dvalue = 3.58
  Group = -> [Mg_element007,O_element060]
  conduct = 2
  density = 1
  expand = 3
  formula = G4_MAGNESIUM_OXIDE
  name = G4_MAGNESIUM_OXIDE
  specific = 4
FEATURE [App::DocumentObjectGroupPython] Mg_element008  label="Mg_element : 004"  # scripted group (container) (typed FeaturePython)
  n = 1
  ref = Mg_element
FEATURE [App::DocumentObjectGroupPython] B_element006  label="B_element : 006"  # scripted group (container) (typed FeaturePython)
  n = 4
  ref = B_element
FEATURE [App::DocumentObjectGroupPython] O_element061  label="O_element : 032"  # scripted group (container) (typed FeaturePython)
  n = 7
  ref = O_element
FEATURE [App::DocumentObjectGroupPython] G4_MAGNESIUM_TETRABORATE  # scripted group (container) (typed FeaturePython)
  Dunit = g/cm3
  Dvalue = 2.53
  Group = -> [Mg_element008,B_element006,O_element061]
  conduct = 2
  density = 1
  expand = 3
  formula = G4_MAGNESIUM_TETRABORATE
  name = G4_MAGNESIUM_TETRABORATE
  specific = 4
FEATURE [App::DocumentObjectGroupPython] Hg_element001  label="Hg_element : 1"  # scripted group (container) (typed FeaturePython)
  n = 1
  ref = Hg_element
FEATURE [App::DocumentObjectGroupPython] I_element004  label="I_element : 2"  # scripted group (container) (typed FeaturePython)
  n = 2
  ref = I_element
FEATURE [App::DocumentObjectGroupPython] G4_MERCURIC_IODIDE  # scripted group (container) (typed FeaturePython)
  Dunit = g/cm3
  Dvalue = 6.36
  Group = -> [Hg_element001,I_element004]
  conduct = 2
  density = 1
  expand = 3
  formula = G4_MERCURIC_IODIDE
  name = G4_MERCURIC_IODIDE
  specific = 4
FEATURE [App::DocumentObjectGroupPython] C_element059  label="C_element : 032"  # scripted group (container) (typed FeaturePython)
  n = 1
  ref = C_element
FEATURE [App::DocumentObjectGroupPython] H_element053  label="H_element : 028"  # scripted group (container) (typed FeaturePython)
  n = 4
  ref = H_element
FEATURE [App::DocumentObjectGroupPython] G4_METHANE  # scripted group (container) (typed FeaturePython)
  Dunit = g/cm3
  Dvalue = 0.000667151
  Group = -> [C_element059,H_element053]
  conduct = 2
  density = 1
  expand = 3
  formula = G4_METHANE
  name = G4_METHANE
  specific = 4
FEATURE [App::DocumentObjectGroupPython] C_element060  label="C_element : 033"  # scripted group (container) (typed FeaturePython)
  n = 1
  ref = C_element
FEATURE [App::DocumentObjectGroupPython] H_element054  label="H_element : 029"  # scripted group (container) (typed FeaturePython)
  n = 4
  ref = H_element
FEATURE [App::DocumentObjectGroupPython] O_element062  label="O_element : 033"  # scripted group (container) (typed FeaturePython)
  n = 1
  ref = O_element
FEATURE [App::DocumentObjectGroupPython] G4_METHANOL  # scripted group (container) (typed FeaturePython)
  Dunit = g/cm3
  Dvalue = 0.7914
  Group = -> [C_element060,H_element054,O_element062]
  conduct = 2
  density = 1
  expand = 3
  formula = G4_METHANOL
  name = G4_METHANOL
  specific = 4
FEATURE [App::DocumentObjectGroupPython] H_element055  label="H_element : 0.134"  # scripted group (container) (typed FeaturePython)
  n = 0.13404
FEATURE [App::DocumentObjectGroupPython] C_element061  label="C_element : 0.778"  # scripted group (container) (typed FeaturePython)
  n = 0.77796
FEATURE [App::DocumentObjectGroupPython] O_element063  label="O_element : 0.035"  # scripted group (container) (typed FeaturePython)
  n = 0.03502
FEATURE [App::DocumentObjectGroupPython] Mg_element009  label="Mg_element : 0.039"  # scripted group (container) (typed FeaturePython)
  n = 0.038594
FEATURE [App::DocumentObjectGroupPython] Ti_element002  label="Ti_element : 0.014"  # scripted group (container) (typed FeaturePython)
  n = 0.014386
FEATURE [App::DocumentObjectGroupPython] G4_MIX_D_WAX  # scripted group (container) (typed FeaturePython)
  Dunit = g/cm3
  Dvalue = 0.99
  Group = -> [H_element055,C_element061,O_element063,Mg_element009,Ti_element002]
  conduct = 2
  density = 1
  expand = 3
  formula = G4_MIX_D_WAX
  name = G4_MIX_D_WAX
  specific = 4
FEATURE [App::DocumentObjectGroupPython] H_element056  label="H_element : 0.135"  # scripted group (container) (typed FeaturePython)
  n = 0.081192
FEATURE [App::DocumentObjectGroupPython] C_element062  label="C_element : 0.583"  # scripted group (container) (typed FeaturePython)
  n = 0.583442
FEATURE [App::DocumentObjectGroupPython] N_element024  label="N_element : 0.018"  # scripted group (container) (typed FeaturePython)
  n = 0.017798
FEATURE [App::DocumentObjectGroupPython] O_element064  label="O_element : 0.186"  # scripted group (container) (typed FeaturePython)
  n = 0.186381
FEATURE [App::DocumentObjectGroupPython] Mg_element010  label="Mg_element : 0.130"  # scripted group (container) (typed FeaturePython)
  n = 0.130287
FEATURE [App::DocumentObjectGroupPython] Cl_element015  label="Cl_element : 0.588"  # scripted group (container) (typed FeaturePython)
  n = 0.0009
FEATURE [App::DocumentObjectGroupPython] G4_MS20_TISSUE  # scripted group (container) (typed FeaturePython)
  Dunit = g/cm3
  Dvalue = 1
  Group = -> [H_element056,C_element062,N_element024,O_element064,Mg_element010,Cl_element015]
  conduct = 2
  density = 1
  expand = 3
  formula = G4_MS20_TISSUE
  name = G4_MS20_TISSUE
  specific = 4
FEATURE [App::DocumentObjectGroupPython] H_element057  label="H_element : 0.136"  # scripted group (container) (typed FeaturePython)
  n = 0.102
FEATURE [App::DocumentObjectGroupPython] C_element063  label="C_element : 0.143"  # scripted group (container) (typed FeaturePython)
  n = 0.143
FEATURE [App::DocumentObjectGroupPython] N_element025  label="N_element : 0.034"  # scripted group (container) (typed FeaturePython)
  n = 0.034
FEATURE [App::DocumentObjectGroupPython] O_element065  label="O_element : 0.710"  # scripted group (container) (typed FeaturePython)
  n = 0.71
FEATURE [App::DocumentObjectGroupPython] Na_element011  label="Na_element : 0.098"  # scripted group (container) (typed FeaturePython)
  n = 0.001
FEATURE [App::DocumentObjectGroupPython] P_element007  label="P_element : 0.002"  # scripted group (container) (typed FeaturePython)
  n = 0.002
FEATURE [App::DocumentObjectGroupPython] S_element017  label="S_element : 0.018"  # scripted group (container) (typed FeaturePython)
  n = 0.003
FEATURE [App::DocumentObjectGroupPython] Cl_element016  label="Cl_element : 0.589"  # scripted group (container) (typed FeaturePython)
  n = 0.001
FEATURE [App::DocumentObjectGroupPython] K_element006  label="K_element : 0.004"  # scripted group (container) (typed FeaturePython)
  n = 0.004
FEATURE [App::DocumentObjectGroupPython] G4_MUSCLE_SKELETAL_ICRP  # scripted group (container) (typed FeaturePython)
  Dunit = g/cm3
  Dvalue = 1.05
  Group = -> [H_element057,C_element063,N_element025,O_element065,Na_element011,P_element007,S_element017,Cl_element016,K_element006]
  conduct = 2
  density = 1
  expand = 3
  formula = G4_MUSCLE_SKELETAL_ICRP
  name = G4_MUSCLE_SKELETAL_ICRP
  specific = 4
FEATURE [App::DocumentObjectGroupPython] H_element058  label="H_element : 0.137"  # scripted group (container) (typed FeaturePython)
  n = 0.102102
FEATURE [App::DocumentObjectGroupPython] C_element064  label="C_element : 0.123"  # scripted group (container) (typed FeaturePython)
  n = 0.123123
FEATURE [App::DocumentObjectGroupPython] N_element026  label="N_element : 0.756"  # scripted group (container) (typed FeaturePython)
  n = 0.035035
FEATURE [App::DocumentObjectGroupPython] O_element066  label="O_element : 0.730"  # scripted group (container) (typed FeaturePython)
  n = 0.72973
FEATURE [App::DocumentObjectGroupPython] Na_element012  label="Na_element : 0.099"  # scripted group (container) (typed FeaturePython)
  n = 0.001001
FEATURE [App::DocumentObjectGroupPython] P_element008  label="P_element : 0.106"  # scripted group (container) (typed FeaturePython)
  n = 0.002002
FEATURE [App::DocumentObjectGroupPython] S_element018  label="S_element : 0.019"  # scripted group (container) (typed FeaturePython)
  n = 0.004004
FEATURE [App::DocumentObjectGroupPython] K_element007  label="K_element : 0.016"  # scripted group (container) (typed FeaturePython)
  n = 0.003003
FEATURE [App::DocumentObjectGroupPython] G4_MUSCLE_STRIATED_ICRU  # scripted group (container) (typed FeaturePython)
  Dunit = g/cm3
  Dvalue = 1.04
  Group = -> [H_element058,C_element064,N_element026,O_element066,Na_element012,P_element008,S_element018,K_element007]
  conduct = 2
  density = 1
  expand = 3
  formula = G4_MUSCLE_STRIATED_ICRU
  name = G4_MUSCLE_STRIATED_ICRU
  specific = 4
FEATURE [App::DocumentObjectGroupPython] H_element059  label="H_element : 0.098"  # scripted group (container) (typed FeaturePython)
  n = 0.0982341
FEATURE [App::DocumentObjectGroupPython] C_element065  label="C_element : 0.156"  # scripted group (container) (typed FeaturePython)
  n = 0.156214
FEATURE [App::DocumentObjectGroupPython] N_element027  label="N_element : 0.757"  # scripted group (container) (typed FeaturePython)
  n = 0.035451
FEATURE [App::DocumentObjectGroupPython] O_element067  label="O_element : 0.880"  # scripted group (container) (typed FeaturePython)
  n = 0.710101
FEATURE [App::DocumentObjectGroupPython] G4_MUSCLE_WITH_SUCROSE  # scripted group (container) (typed FeaturePython)
  Dunit = g/cm3
  Dvalue = 1.11
  Group = -> [H_element059,C_element065,N_element027,O_element067]
  conduct = 2
  density = 1
  expand = 3
  formula = G4_MUSCLE_WITH_SUCROSE
  name = G4_MUSCLE_WITH_SUCROSE
  specific = 4
FEATURE [App::DocumentObjectGroupPython] H_element060  label="H_element : 0.138"  # scripted group (container) (typed FeaturePython)
  n = 0.101969
FEATURE [App::DocumentObjectGroupPython] C_element066  label="C_element : 0.120"  # scripted group (container) (typed FeaturePython)
  n = 0.120058
FEATURE [App::DocumentObjectGroupPython] N_element028  label="N_element : 0.758"  # scripted group (container) (typed FeaturePython)
  n = 0.035451
FEATURE [App::DocumentObjectGroupPython] O_element068  label="O_element : 0.743"  # scripted group (container) (typed FeaturePython)
  n = 0.742522
FEATURE [App::DocumentObjectGroupPython] G4_MUSCLE_WITHOUT_SUCROSE  # scripted group (container) (typed FeaturePython)
  Dunit = g/cm3
  Dvalue = 1.07
  Group = -> [H_element060,C_element066,N_element028,O_element068]
  conduct = 2
  density = 1
  expand = 3
  formula = G4_MUSCLE_WITHOUT_SUCROSE
  name = G4_MUSCLE_WITHOUT_SUCROSE
  specific = 4
FEATURE [App::DocumentObjectGroupPython] C_element067  label="C_element : 10"  # scripted group (container) (typed FeaturePython)
  n = 10
  ref = C_element
FEATURE [App::DocumentObjectGroupPython] H_element061  label="H_element : 030"  # scripted group (container) (typed FeaturePython)
  n = 8
  ref = H_element
FEATURE [App::DocumentObjectGroupPython] G4_NAPHTHALENE  # scripted group (container) (typed FeaturePython)
  Dunit = g/cm3
  Dvalue = 1.145
  Group = -> [C_element067,H_element061]
  conduct = 2
  density = 1
  expand = 3
  formula = G4_NAPHTHALENE
  name = G4_NAPHTHALENE
  specific = 4
FEATURE [App::DocumentObjectGroupPython] C_element068  label="C_element : 034"  # scripted group (container) (typed FeaturePython)
  n = 6
  ref = C_element
FEATURE [App::DocumentObjectGroupPython] H_element062  label="H_element : 031"  # scripted group (container) (typed FeaturePython)
  n = 5
  ref = H_element
FEATURE [App::DocumentObjectGroupPython] N_element029  label="N_element : 012"  # scripted group (container) (typed FeaturePython)
  n = 1
  ref = N_element
FEATURE [App::DocumentObjectGroupPython] O_element069  label="O_element : 034"  # scripted group (container) (typed FeaturePython)
  n = 2
  ref = O_element
FEATURE [App::DocumentObjectGroupPython] G4_NITROBENZENE  # scripted group (container) (typed FeaturePython)
  Dunit = g/cm3
  Dvalue = 1.19867
  Group = -> [C_element068,H_element062,N_element029,O_element069]
  conduct = 2
  density = 1
  expand = 3
  formula = G4_NITROBENZENE
  name = G4_NITROBENZENE
  specific = 4
FEATURE [App::DocumentObjectGroupPython] N_element030  label="N_element : 013"  # scripted group (container) (typed FeaturePython)
  n = 2
  ref = N_element
FEATURE [App::DocumentObjectGroupPython] O_element070  label="O_element : 035"  # scripted group (container) (typed FeaturePython)
  n = 1
  ref = O_element
FEATURE [App::DocumentObjectGroupPython] G4_NITROUS_OXIDE  # scripted group (container) (typed FeaturePython)
  Dunit = g/cm3
  Dvalue = 0.00183094
  Group = -> [N_element030,O_element070]
  conduct = 2
  density = 1
  expand = 3
  formula = G4_NITROUS_OXIDE
  name = G4_NITROUS_OXIDE
  specific = 4
FEATURE [App::DocumentObjectGroupPython] H_element063  label="H_element : 0.104"  # scripted group (container) (typed FeaturePython)
  n = 0.103509
FEATURE [App::DocumentObjectGroupPython] C_element069  label="C_element : 0.648"  # scripted group (container) (typed FeaturePython)
  n = 0.648416
FEATURE [App::DocumentObjectGroupPython] N_element031  label="N_element : 0.100"  # scripted group (container) (typed FeaturePython)
  n = 0.0995361
FEATURE [App::DocumentObjectGroupPython] O_element071  label="O_element : 0.149"  # scripted group (container) (typed FeaturePython)
  n = 0.148539
FEATURE [App::DocumentObjectGroupPython] G4_NYLON_8062  label="G4_NYLON-8062"  # scripted group (container) (typed FeaturePython)
  Dunit = g/cm3
  Dvalue = 1.08
  Group = -> [H_element063,C_element069,N_element031,O_element071]
  conduct = 2
  density = 1
  expand = 3
  formula = G4_NYLON-8062
  name = G4_NYLON-8062
  specific = 4
FEATURE [App::DocumentObjectGroupPython] C_element070  label="C_element : 035"  # scripted group (container) (typed FeaturePython)
  n = 6
  ref = C_element
FEATURE [App::DocumentObjectGroupPython] H_element064  label="H_element : 11"  # scripted group (container) (typed FeaturePython)
  n = 11
  ref = H_element
FEATURE [App::DocumentObjectGroupPython] N_element032  label="N_element : 014"  # scripted group (container) (typed FeaturePython)
  n = 1
  ref = N_element
FEATURE [App::DocumentObjectGroupPython] O_element072  label="O_element : 036"  # scripted group (container) (typed FeaturePython)
  n = 1
  ref = O_element
FEATURE [App::DocumentObjectGroupPython] G4_NYLON_6_6  label="G4_NYLON-6-6"  # scripted group (container) (typed FeaturePython)
  Dunit = g/cm3
  Dvalue = 1.14
  Group = -> [C_element070,H_element064,N_element032,O_element072]
  conduct = 2
  density = 1
  expand = 3
  formula = G4_NYLON-6-6
  name = G4_NYLON-6-6
  specific = 4
FEATURE [App::DocumentObjectGroupPython] H_element065  label="H_element : 0.139"  # scripted group (container) (typed FeaturePython)
  n = 0.107062
FEATURE [App::DocumentObjectGroupPython] C_element071  label="C_element : 0.680"  # scripted group (container) (typed FeaturePython)
  n = 0.680449
FEATURE [App::DocumentObjectGroupPython] N_element033  label="N_element : 0.099"  # scripted group (container) (typed FeaturePython)
  n = 0.099189
FEATURE [App::DocumentObjectGroupPython] O_element073  label="O_element : 0.113"  # scripted group (container) (typed FeaturePython)
  n = 0.1133
FEATURE [App::DocumentObjectGroupPython] G4_NYLON_6_10  label="G4_NYLON-6-10"  # scripted group (container) (typed FeaturePython)
  Dunit = g/cm3
  Dvalue = 1.14
  Group = -> [H_element065,C_element071,N_element033,O_element073]
  conduct = 2
  density = 1
  expand = 3
  formula = G4_NYLON-6-10
  name = G4_NYLON-6-10
  specific = 4
FEATURE [App::DocumentObjectGroupPython] H_element066  label="H_element : 0.140"  # scripted group (container) (typed FeaturePython)
  n = 0.115476
FEATURE [App::DocumentObjectGroupPython] C_element072  label="C_element : 0.721"  # scripted group (container) (typed FeaturePython)
  n = 0.720818
FEATURE [App::DocumentObjectGroupPython] N_element034  label="N_element : 0.076"  # scripted group (container) (typed FeaturePython)
  n = 0.0764169
FEATURE [App::DocumentObjectGroupPython] O_element074  label="O_element : 0.087"  # scripted group (container) (typed FeaturePython)
  n = 0.0872889
FEATURE [App::DocumentObjectGroupPython] G4_NYLON_11_RILSAN  label="G4_NYLON-11_RILSAN"  # scripted group (container) (typed FeaturePython)
  Dunit = g/cm3
  Dvalue = 1.425
  Group = -> [H_element066,C_element072,N_element034,O_element074]
  conduct = 2
  density = 1
  expand = 3
  formula = G4_NYLON-11_RILSAN
  name = G4_NYLON-11_RILSAN
  specific = 4
FEATURE [App::DocumentObjectGroupPython] C_element073  label="C_element : 8"  # scripted group (container) (typed FeaturePython)
  n = 8
  ref = C_element
FEATURE [App::DocumentObjectGroupPython] H_element067  label="H_element : 18"  # scripted group (container) (typed FeaturePython)
  n = 18
  ref = H_element
FEATURE [App::DocumentObjectGroupPython] G4_OCTANE  # scripted group (container) (typed FeaturePython)
  Dunit = g/cm3
  Dvalue = 0.7026
  Group = -> [C_element073,H_element067]
  conduct = 2
  density = 1
  expand = 3
  formula = G4_OCTANE
  name = G4_OCTANE
  specific = 4
FEATURE [App::DocumentObjectGroupPython] C_element074  label="C_element : 25"  # scripted group (container) (typed FeaturePython)
  n = 25
  ref = C_element
FEATURE [App::DocumentObjectGroupPython] H_element068  label="H_element : 52"  # scripted group (container) (typed FeaturePython)
  n = 52
  ref = H_element
FEATURE [App::DocumentObjectGroupPython] G4_PARAFFIN  # scripted group (container) (typed FeaturePython)
  Dunit = g/cm3
  Dvalue = 0.93
  Group = -> [C_element074,H_element068]
  conduct = 2
  density = 1
  expand = 3
  formula = G4_PARAFFIN
  name = G4_PARAFFIN
  specific = 4
FEATURE [App::DocumentObjectGroupPython] C_element075  label="C_element : 036"  # scripted group (container) (typed FeaturePython)
  n = 5
  ref = C_element
FEATURE [App::DocumentObjectGroupPython] H_element069  label="H_element : 032"  # scripted group (container) (typed FeaturePython)
  n = 12
  ref = H_element
FEATURE [App::DocumentObjectGroupPython] G4_N_PENTANE  label="G4_N-PENTANE"  # scripted group (container) (typed FeaturePython)
  Dunit = g/cm3
  Dvalue = 0.6262
  Group = -> [C_element075,H_element069]
  conduct = 2
  density = 1
  expand = 3
  formula = G4_N-PENTANE
  name = G4_N-PENTANE
  specific = 4
FEATURE [App::DocumentObjectGroupPython] H_element070  label="H_element : 0.014"  # scripted group (container) (typed FeaturePython)
  n = 0.0141
FEATURE [App::DocumentObjectGroupPython] C_element076  label="C_element : 0.072"  # scripted group (container) (typed FeaturePython)
  n = 0.072261
FEATURE [App::DocumentObjectGroupPython] N_element035  label="N_element : 0.019"  # scripted group (container) (typed FeaturePython)
  n = 0.01932
FEATURE [App::DocumentObjectGroupPython] O_element075  label="O_element : 0.066"  # scripted group (container) (typed FeaturePython)
  n = 0.066101
FEATURE [App::DocumentObjectGroupPython] S_element019  label="S_element : 0.020"  # scripted group (container) (typed FeaturePython)
  n = 0.00189
FEATURE [App::DocumentObjectGroupPython] Br_element004  label="Br_element : 0.349"  # scripted group (container) (typed FeaturePython)
  n = 0.349103
FEATURE [App::DocumentObjectGroupPython] Ag_element001  label="Ag_element : 0.474"  # scripted group (container) (typed FeaturePython)
  n = 0.474105
FEATURE [App::DocumentObjectGroupPython] I_element005  label="I_element : 0.003"  # scripted group (container) (typed FeaturePython)
  n = 0.00312
FEATURE [App::DocumentObjectGroupPython] G4_PHOTO_EMULSION  # scripted group (container) (typed FeaturePython)
  Dunit = g/cm3
  Dvalue = 3.815
  Group = -> [H_element070,C_element076,N_element035,O_element075,S_element019,Br_element004,Ag_element001,I_element005]
  conduct = 2
  density = 1
  expand = 3
  formula = G4_PHOTO_EMULSION
  name = G4_PHOTO_EMULSION
  specific = 4
FEATURE [App::DocumentObjectGroupPython] C_element077  label="C_element : 9"  # scripted group (container) (typed FeaturePython)
  n = 9
  ref = C_element
FEATURE [App::DocumentObjectGroupPython] H_element071  label="H_element : 033"  # scripted group (container) (typed FeaturePython)
  n = 10
  ref = H_element
FEATURE [App::DocumentObjectGroupPython] G4_PLASTIC_SC_VINYLTOLUENE  # scripted group (container) (typed FeaturePython)
  Dunit = g/cm3
  Dvalue = 1.032
  Group = -> [C_element077,H_element071]
  conduct = 2
  density = 1
  expand = 3
  formula = G4_PLASTIC_SC_VINYLTOLUENE
  name = G4_PLASTIC_SC_VINYLTOLUENE
  specific = 4
FEATURE [App::DocumentObjectGroupPython] Pu_element001  label="Pu_element : 1"  # scripted group (container) (typed FeaturePython)
  n = 1
  ref = Pu_element
FEATURE [App::DocumentObjectGroupPython] O_element076  label="O_element : 037"  # scripted group (container) (typed FeaturePython)
  n = 2
  ref = O_element
FEATURE [App::DocumentObjectGroupPython] G4_PLUTONIUM_DIOXIDE  # scripted group (container) (typed FeaturePython)
  Dunit = g/cm3
  Dvalue = 11.46
  Group = -> [Pu_element001,O_element076]
  conduct = 2
  density = 1
  expand = 3
  formula = G4_PLUTONIUM_DIOXIDE
  name = G4_PLUTONIUM_DIOXIDE
  specific = 4
FEATURE [App::DocumentObjectGroupPython] C_element078  label="C_element : 037"  # scripted group (container) (typed FeaturePython)
  n = 3
  ref = C_element
FEATURE [App::DocumentObjectGroupPython] H_element072  label="H_element : 034"  # scripted group (container) (typed FeaturePython)
  n = 3
  ref = H_element
FEATURE [App::DocumentObjectGroupPython] N_element036  label="N_element : 015"  # scripted group (container) (typed FeaturePython)
  n = 1
  ref = N_element
FEATURE [App::DocumentObjectGroupPython] G4_POLYACRYLONITRILE  # scripted group (container) (typed FeaturePython)
  Dunit = g/cm3
  Dvalue = 1.17
  Group = -> [C_element078,H_element072,N_element036]
  conduct = 2
  density = 1
  expand = 3
  formula = G4_POLYACRYLONITRILE
  name = G4_POLYACRYLONITRILE
  specific = 4
FEATURE [App::DocumentObjectGroupPython] C_element079  label="C_element : 16"  # scripted group (container) (typed FeaturePython)
  n = 16
  ref = C_element
FEATURE [App::DocumentObjectGroupPython] H_element073  label="H_element : 035"  # scripted group (container) (typed FeaturePython)
  n = 14
  ref = H_element
FEATURE [App::DocumentObjectGroupPython] O_element077  label="O_element : 038"  # scripted group (container) (typed FeaturePython)
  n = 3
  ref = O_element
FEATURE [App::DocumentObjectGroupPython] G4_POLYCARBONATE  # scripted group (container) (typed FeaturePython)
  Dunit = g/cm3
  Dvalue = 1.2
  Group = -> [C_element079,H_element073,O_element077]
  conduct = 2
  density = 1
  expand = 3
  formula = G4_POLYCARBONATE
  name = G4_POLYCARBONATE
  specific = 4
FEATURE [App::DocumentObjectGroupPython] C_element080  label="C_element : 038"  # scripted group (container) (typed FeaturePython)
  n = 8
  ref = C_element
FEATURE [App::DocumentObjectGroupPython] H_element074  label="H_element : 036"  # scripted group (container) (typed FeaturePython)
  n = 7
  ref = H_element
FEATURE [App::DocumentObjectGroupPython] Cl_element017  label="Cl_element : 007"  # scripted group (container) (typed FeaturePython)
  n = 1
  ref = Cl_element
FEATURE [App::DocumentObjectGroupPython] G4_POLYCHLOROSTYRENE  # scripted group (container) (typed FeaturePython)
  Dunit = g/cm3
  Dvalue = 1.3
  Group = -> [C_element080,H_element074,Cl_element017]
  conduct = 2
  density = 1
  expand = 3
  formula = G4_POLYCHLOROSTYRENE
  name = G4_POLYCHLOROSTYRENE
  specific = 4
FEATURE [App::DocumentObjectGroupPython] C_element081  label="C_element : 039"  # scripted group (container) (typed FeaturePython)
  n = 1
  ref = C_element
FEATURE [App::DocumentObjectGroupPython] H_element075  label="H_element : 037"  # scripted group (container) (typed FeaturePython)
  n = 2
  ref = H_element
FEATURE [App::DocumentObjectGroupPython] G4_POLYETHYLENE  # scripted group (container) (typed FeaturePython)
  Dunit = g/cm3
  Dvalue = 0.94
  Group = -> [C_element081,H_element075]
  conduct = 2
  density = 1
  expand = 3
  formula = G4_POLYETHYLENE
  name = G4_POLYETHYLENE
  specific = 4
FEATURE [App::DocumentObjectGroupPython] C_element082  label="C_element : 040"  # scripted group (container) (typed FeaturePython)
  n = 10
  ref = C_element
FEATURE [App::DocumentObjectGroupPython] H_element076  label="H_element : 038"  # scripted group (container) (typed FeaturePython)
  n = 8
  ref = H_element
FEATURE [App::DocumentObjectGroupPython] O_element078  label="O_element : 039"  # scripted group (container) (typed FeaturePython)
  n = 4
  ref = O_element
FEATURE [App::DocumentObjectGroupPython] G4_MYLAR  # scripted group (container) (typed FeaturePython)
  Dunit = g/cm3
  Dvalue = 1.4
  Group = -> [C_element082,H_element076,O_element078]
  conduct = 2
  density = 1
  expand = 3
  formula = G4_MYLAR
  name = G4_MYLAR
  specific = 4
FEATURE [App::DocumentObjectGroupPython] C_element083  label="C_element : 041"  # scripted group (container) (typed FeaturePython)
  n = 5
  ref = C_element
FEATURE [App::DocumentObjectGroupPython] H_element077  label="H_element : 039"  # scripted group (container) (typed FeaturePython)
  n = 8
  ref = H_element
FEATURE [App::DocumentObjectGroupPython] O_element079  label="O_element : 040"  # scripted group (container) (typed FeaturePython)
  n = 2
  ref = O_element
FEATURE [App::DocumentObjectGroupPython] G4_PLEXIGLASS  # scripted group (container) (typed FeaturePython)
  Dunit = g/cm3
  Dvalue = 1.19
  Group = -> [C_element083,H_element077,O_element079]
  conduct = 2
  density = 1
  expand = 3
  formula = G4_PLEXIGLASS
  name = G4_PLEXIGLASS
  specific = 4
FEATURE [App::DocumentObjectGroupPython] C_element084  label="C_element : 042"  # scripted group (container) (typed FeaturePython)
  n = 1
  ref = C_element
FEATURE [App::DocumentObjectGroupPython] H_element078  label="H_element : 040"  # scripted group (container) (typed FeaturePython)
  n = 2
  ref = H_element
FEATURE [App::DocumentObjectGroupPython] O_element080  label="O_element : 041"  # scripted group (container) (typed FeaturePython)
  n = 1
  ref = O_element
FEATURE [App::DocumentObjectGroupPython] G4_POLYOXYMETHYLENE  # scripted group (container) (typed FeaturePython)
  Dunit = g/cm3
  Dvalue = 1.425
  Group = -> [C_element084,H_element078,O_element080]
  conduct = 2
  density = 1
  expand = 3
  formula = G4_POLYOXYMETHYLENE
  name = G4_POLYOXYMETHYLENE
  specific = 4
FEATURE [App::DocumentObjectGroupPython] C_element085  label="C_element : 043"  # scripted group (container) (typed FeaturePython)
  n = 2
  ref = C_element
FEATURE [App::DocumentObjectGroupPython] H_element079  label="H_element : 041"  # scripted group (container) (typed FeaturePython)
  n = 4
  ref = H_element
FEATURE [App::DocumentObjectGroupPython] G4_POLYPROPYLENE  # scripted group (container) (typed FeaturePython)
  Dunit = g/cm3
  Dvalue = 0.9
  Group = -> [C_element085,H_element079]
  conduct = 2
  density = 1
  expand = 3
  formula = G4_POLYPROPYLENE
  name = G4_POLYPROPYLENE
  specific = 4
FEATURE [App::DocumentObjectGroupPython] C_element086  label="C_element : 044"  # scripted group (container) (typed FeaturePython)
  n = 8
  ref = C_element
FEATURE [App::DocumentObjectGroupPython] H_element080  label="H_element : 042"  # scripted group (container) (typed FeaturePython)
  n = 8
  ref = H_element
FEATURE [App::DocumentObjectGroupPython] G4_POLYSTYRENE  # scripted group (container) (typed FeaturePython)
  Dunit = g/cm3
  Dvalue = 1.06
  Group = -> [C_element086,H_element080]
  conduct = 2
  density = 1
  expand = 3
  formula = G4_POLYSTYRENE
  name = G4_POLYSTYRENE
  specific = 4
FEATURE [App::DocumentObjectGroupPython] C_element087  label="C_element : 045"  # scripted group (container) (typed FeaturePython)
  n = 2
  ref = C_element
FEATURE [App::DocumentObjectGroupPython] F_element014  label="F_element : 4"  # scripted group (container) (typed FeaturePython)
  n = 4
  ref = F_element
FEATURE [App::DocumentObjectGroupPython] G4_TEFLON  # scripted group (container) (typed FeaturePython)
  Dunit = g/cm3
  Dvalue = 2.2
  Group = -> [C_element087,F_element014]
  conduct = 2
  density = 1
  expand = 3
  formula = G4_TEFLON
  name = G4_TEFLON
  specific = 4
FEATURE [App::DocumentObjectGroupPython] C_element088  label="C_element : 046"  # scripted group (container) (typed FeaturePython)
  n = 2
  ref = C_element
FEATURE [App::DocumentObjectGroupPython] F_element015  label="F_element : 006"  # scripted group (container) (typed FeaturePython)
  n = 3
  ref = F_element
FEATURE [App::DocumentObjectGroupPython] Cl_element018  label="Cl_element : 008"  # scripted group (container) (typed FeaturePython)
  n = 1
  ref = Cl_element
FEATURE [App::DocumentObjectGroupPython] G4_POLYTRIFLUOROCHLOROETHYLENE  # scripted group (container) (typed FeaturePython)
  Dunit = g/cm3
  Dvalue = 2.1
  Group = -> [C_element088,F_element015,Cl_element018]
  conduct = 2
  density = 1
  expand = 3
  formula = G4_POLYTRIFLUOROCHLOROETHYLENE
  name = G4_POLYTRIFLUOROCHLOROETHYLENE
  specific = 4
FEATURE [App::DocumentObjectGroupPython] C_element089  label="C_element : 047"  # scripted group (container) (typed FeaturePython)
  n = 4
  ref = C_element
FEATURE [App::DocumentObjectGroupPython] H_element081  label="H_element : 043"  # scripted group (container) (typed FeaturePython)
  n = 6
  ref = H_element
FEATURE [App::DocumentObjectGroupPython] O_element081  label="O_element : 042"  # scripted group (container) (typed FeaturePython)
  n = 2
  ref = O_element
FEATURE [App::DocumentObjectGroupPython] G4_POLYVINYL_ACETATE  # scripted group (container) (typed FeaturePython)
  Dunit = g/cm3
  Dvalue = 1.19
  Group = -> [C_element089,H_element081,O_element081]
  conduct = 2
  density = 1
  expand = 3
  formula = G4_POLYVINYL_ACETATE
  name = G4_POLYVINYL_ACETATE
  specific = 4
FEATURE [App::DocumentObjectGroupPython] C_element090  label="C_element : 048"  # scripted group (container) (typed FeaturePython)
  n = 2
  ref = C_element
FEATURE [App::DocumentObjectGroupPython] H_element082  label="H_element : 044"  # scripted group (container) (typed FeaturePython)
  n = 4
  ref = H_element
FEATURE [App::DocumentObjectGroupPython] O_element082  label="O_element : 043"  # scripted group (container) (typed FeaturePython)
  n = 1
  ref = O_element
FEATURE [App::DocumentObjectGroupPython] G4_POLYVINYL_ALCOHOL  # scripted group (container) (typed FeaturePython)
  Dunit = g/cm3
  Dvalue = 1.3
  Group = -> [C_element090,H_element082,O_element082]
  conduct = 2
  density = 1
  expand = 3
  formula = G4_POLYVINYL_ALCOHOL
  name = G4_POLYVINYL_ALCOHOL
  specific = 4
FEATURE [App::DocumentObjectGroupPython] C_element091  label="C_element : 049"  # scripted group (container) (typed FeaturePython)
  n = 8
  ref = C_element
FEATURE [App::DocumentObjectGroupPython] H_element083  label="H_element : 045"  # scripted group (container) (typed FeaturePython)
  n = 14
  ref = H_element
FEATURE [App::DocumentObjectGroupPython] O_element083  label="O_element : 044"  # scripted group (container) (typed FeaturePython)
  n = 2
  ref = O_element
FEATURE [App::DocumentObjectGroupPython] G4_POLYVINYL_BUTYRAL  # scripted group (container) (typed FeaturePython)
  Dunit = g/cm3
  Dvalue = 1.12
  Group = -> [C_element091,H_element083,O_element083]
  conduct = 2
  density = 1
  expand = 3
  formula = G4_POLYVINYL_BUTYRAL
  name = G4_POLYVINYL_BUTYRAL
  specific = 4
FEATURE [App::DocumentObjectGroupPython] C_element092  label="C_element : 050"  # scripted group (container) (typed FeaturePython)
  n = 2
  ref = C_element
FEATURE [App::DocumentObjectGroupPython] H_element084  label="H_element : 046"  # scripted group (container) (typed FeaturePython)
  n = 3
  ref = H_element
FEATURE [App::DocumentObjectGroupPython] Cl_element019  label="Cl_element : 009"  # scripted group (container) (typed FeaturePython)
  n = 1
  ref = Cl_element
FEATURE [App::DocumentObjectGroupPython] G4_POLYVINYL_CHLORIDE  # scripted group (container) (typed FeaturePython)
  Dunit = g/cm3
  Dvalue = 1.3
  Group = -> [C_element092,H_element084,Cl_element019]
  conduct = 2
  density = 1
  expand = 3
  formula = G4_POLYVINYL_CHLORIDE
  name = G4_POLYVINYL_CHLORIDE
  specific = 4
FEATURE [App::DocumentObjectGroupPython] C_element093  label="C_element : 051"  # scripted group (container) (typed FeaturePython)
  n = 2
  ref = C_element
FEATURE [App::DocumentObjectGroupPython] H_element085  label="H_element : 047"  # scripted group (container) (typed FeaturePython)
  n = 2
  ref = H_element
FEATURE [App::DocumentObjectGroupPython] Cl_element020  label="Cl_element : 010"  # scripted group (container) (typed FeaturePython)
  n = 2
  ref = Cl_element
FEATURE [App::DocumentObjectGroupPython] G4_POLYVINYLIDENE_CHLORIDE  # scripted group (container) (typed FeaturePython)
  Dunit = g/cm3
  Dvalue = 1.7
  Group = -> [C_element093,H_element085,Cl_element020]
  conduct = 2
  density = 1
  expand = 3
  formula = G4_POLYVINYLIDENE_CHLORIDE
  name = G4_POLYVINYLIDENE_CHLORIDE
  specific = 4
FEATURE [App::DocumentObjectGroupPython] C_element094  label="C_element : 052"  # scripted group (container) (typed FeaturePython)
  n = 2
  ref = C_element
FEATURE [App::DocumentObjectGroupPython] H_element086  label="H_element : 048"  # scripted group (container) (typed FeaturePython)
  n = 2
  ref = H_element
FEATURE [App::DocumentObjectGroupPython] F_element016  label="F_element : 007"  # scripted group (container) (typed FeaturePython)
  n = 2
  ref = F_element
FEATURE [App::DocumentObjectGroupPython] G4_POLYVINYLIDENE_FLUORIDE  # scripted group (container) (typed FeaturePython)
  Dunit = g/cm3
  Dvalue = 1.76
  Group = -> [C_element094,H_element086,F_element016]
  conduct = 2
  density = 1
  expand = 3
  formula = G4_POLYVINYLIDENE_FLUORIDE
  name = G4_POLYVINYLIDENE_FLUORIDE
  specific = 4
FEATURE [App::DocumentObjectGroupPython] C_element095  label="C_element : 053"  # scripted group (container) (typed FeaturePython)
  n = 6
  ref = C_element
FEATURE [App::DocumentObjectGroupPython] H_element087  label="H_element : 9"  # scripted group (container) (typed FeaturePython)
  n = 9
  ref = H_element
FEATURE [App::DocumentObjectGroupPython] N_element037  label="N_element : 016"  # scripted group (container) (typed FeaturePython)
  n = 1
  ref = N_element
FEATURE [App::DocumentObjectGroupPython] O_element084  label="O_element : 045"  # scripted group (container) (typed FeaturePython)
  n = 1
  ref = O_element
FEATURE [App::DocumentObjectGroupPython] G4_POLYVINYL_PYRROLIDONE  # scripted group (container) (typed FeaturePython)
  Dunit = g/cm3
  Dvalue = 1.25
  Group = -> [C_element095,H_element087,N_element037,O_element084]
  conduct = 2
  density = 1
  expand = 3
  formula = G4_POLYVINYL_PYRROLIDONE
  name = G4_POLYVINYL_PYRROLIDONE
  specific = 4
FEATURE [App::DocumentObjectGroupPython] K_element008  label="K_element : 1"  # scripted group (container) (typed FeaturePython)
  n = 1
  ref = K_element
FEATURE [App::DocumentObjectGroupPython] I_element006  label="I_element : 003"  # scripted group (container) (typed FeaturePython)
  n = 1
  ref = I_element
FEATURE [App::DocumentObjectGroupPython] G4_POTASSIUM_IODIDE  # scripted group (container) (typed FeaturePython)
  Dunit = g/cm3
  Dvalue = 3.13
  Group = -> [K_element008,I_element006]
  conduct = 2
  density = 1
  expand = 3
  formula = G4_POTASSIUM_IODIDE
  name = G4_POTASSIUM_IODIDE
  specific = 4
FEATURE [App::DocumentObjectGroupPython] K_element009  label="K_element : 2"  # scripted group (container) (typed FeaturePython)
  n = 2
  ref = K_element
FEATURE [App::DocumentObjectGroupPython] O_element085  label="O_element : 046"  # scripted group (container) (typed FeaturePython)
  n = 1
  ref = O_element
FEATURE [App::DocumentObjectGroupPython] G4_POTASSIUM_OXIDE  # scripted group (container) (typed FeaturePython)
  Dunit = g/cm3
  Dvalue = 2.32
  Group = -> [K_element009,O_element085]
  conduct = 2
  density = 1
  expand = 3
  formula = G4_POTASSIUM_OXIDE
  name = G4_POTASSIUM_OXIDE
  specific = 4
FEATURE [App::DocumentObjectGroupPython] C_element096  label="C_element : 054"  # scripted group (container) (typed FeaturePython)
  n = 3
  ref = C_element
FEATURE [App::DocumentObjectGroupPython] H_element088  label="H_element : 049"  # scripted group (container) (typed FeaturePython)
  n = 8
  ref = H_element
FEATURE [App::DocumentObjectGroupPython] G4_PROPANE  # scripted group (container) (typed FeaturePython)
  Dunit = g/cm3
  Dvalue = 0.00187939
  Group = -> [C_element096,H_element088]
  conduct = 2
  density = 1
  expand = 3
  formula = G4_PROPANE
  name = G4_PROPANE
  specific = 4
FEATURE [App::DocumentObjectGroupPython] C_element097  label="C_element : 055"  # scripted group (container) (typed FeaturePython)
  n = 3
  ref = C_element
FEATURE [App::DocumentObjectGroupPython] H_element089  label="H_element : 050"  # scripted group (container) (typed FeaturePython)
  n = 8
  ref = H_element
FEATURE [App::DocumentObjectGroupPython] G4_lPROPANE  # scripted group (container) (typed FeaturePython)
  Dunit = g/cm3
  Dvalue = 0.43
  Group = -> [C_element097,H_element089]
  conduct = 2
  density = 1
  expand = 3
  formula = G4_lPROPANE
  name = G4_lPROPANE
  specific = 4
FEATURE [App::DocumentObjectGroupPython] C_element098  label="C_element : 056"  # scripted group (container) (typed FeaturePython)
  n = 3
  ref = C_element
FEATURE [App::DocumentObjectGroupPython] H_element090  label="H_element : 051"  # scripted group (container) (typed FeaturePython)
  n = 8
  ref = H_element
FEATURE [App::DocumentObjectGroupPython] O_element086  label="O_element : 047"  # scripted group (container) (typed FeaturePython)
  n = 1
  ref = O_element
FEATURE [App::DocumentObjectGroupPython] G4_N_PROPYL_ALCOHOL  label="G4_N-PROPYL_ALCOHOL"  # scripted group (container) (typed FeaturePython)
  Dunit = g/cm3
  Dvalue = 0.8035
  Group = -> [C_element098,H_element090,O_element086]
  conduct = 2
  density = 1
  expand = 3
  formula = G4_N-PROPYL_ALCOHOL
  name = G4_N-PROPYL_ALCOHOL
  specific = 4
FEATURE [App::DocumentObjectGroupPython] C_element099  label="C_element : 057"  # scripted group (container) (typed FeaturePython)
  n = 5
  ref = C_element
FEATURE [App::DocumentObjectGroupPython] H_element091  label="H_element : 052"  # scripted group (container) (typed FeaturePython)
  n = 5
  ref = H_element
FEATURE [App::DocumentObjectGroupPython] N_element038  label="N_element : 017"  # scripted group (container) (typed FeaturePython)
  n = 1
  ref = N_element
FEATURE [App::DocumentObjectGroupPython] G4_PYRIDINE  # scripted group (container) (typed FeaturePython)
  Dunit = g/cm3
  Dvalue = 0.9819
  Group = -> [C_element099,H_element091,N_element038]
  conduct = 2
  density = 1
  expand = 3
  formula = G4_PYRIDINE
  name = G4_PYRIDINE
  specific = 4
FEATURE [App::DocumentObjectGroupPython] H_element092  label="H_element : 0.144"  # scripted group (container) (typed FeaturePython)
  n = 0.143711
FEATURE [App::DocumentObjectGroupPython] C_element100  label="C_element : 0.856"  # scripted group (container) (typed FeaturePython)
  n = 0.856289
FEATURE [App::DocumentObjectGroupPython] G4_RUBBER_BUTYL  # scripted group (container) (typed FeaturePython)
  Dunit = g/cm3
  Dvalue = 0.92
  Group = -> [H_element092,C_element100]
  conduct = 2
  density = 1
  expand = 3
  formula = G4_RUBBER_BUTYL
  name = G4_RUBBER_BUTYL
  specific = 4
FEATURE [App::DocumentObjectGroupPython] H_element093  label="H_element : 0.118"  # scripted group (container) (typed FeaturePython)
  n = 0.118371
FEATURE [App::DocumentObjectGroupPython] C_element101  label="C_element : 0.882"  # scripted group (container) (typed FeaturePython)
  n = 0.881629
FEATURE [App::DocumentObjectGroupPython] G4_RUBBER_NATURAL  # scripted group (container) (typed FeaturePython)
  Dunit = g/cm3
  Dvalue = 0.92
  Group = -> [H_element093,C_element101]
  conduct = 2
  density = 1
  expand = 3
  formula = G4_RUBBER_NATURAL
  name = G4_RUBBER_NATURAL
  specific = 4
FEATURE [App::DocumentObjectGroupPython] H_element094  label="H_element : 0.145"  # scripted group (container) (typed FeaturePython)
  n = 0.05692
FEATURE [App::DocumentObjectGroupPython] C_element102  label="C_element : 0.543"  # scripted group (container) (typed FeaturePython)
  n = 0.542646
FEATURE [App::DocumentObjectGroupPython] Cl_element021  label="Cl_element : 0.400"  # scripted group (container) (typed FeaturePython)
  n = 0.400434
FEATURE [App::DocumentObjectGroupPython] G4_RUBBER_NEOPRENE  # scripted group (container) (typed FeaturePython)
  Dunit = g/cm3
  Dvalue = 1.23
  Group = -> [H_element094,C_element102,Cl_element021]
  conduct = 2
  density = 1
  expand = 3
  formula = G4_RUBBER_NEOPRENE
  name = G4_RUBBER_NEOPRENE
  specific = 4
FEATURE [App::DocumentObjectGroupPython] Si_element006  label="Si_element : 1"  # scripted group (container) (typed FeaturePython)
  n = 1
  ref = Si_element
FEATURE [App::DocumentObjectGroupPython] O_element087  label="O_element : 048"  # scripted group (container) (typed FeaturePython)
  n = 2
  ref = O_element
FEATURE [App::DocumentObjectGroupPython] G4_SILICON_DIOXIDE  # scripted group (container) (typed FeaturePython)
  Dunit = g/cm3
  Dvalue = 2.32
  Group = -> [Si_element006,O_element087]
  conduct = 2
  density = 1
  expand = 3
  formula = G4_SILICON_DIOXIDE
  name = G4_SILICON_DIOXIDE
  specific = 4
FEATURE [App::DocumentObjectGroupPython] Ag_element002  label="Ag_element : 1"  # scripted group (container) (typed FeaturePython)
  n = 1
  ref = Ag_element
FEATURE [App::DocumentObjectGroupPython] Br_element005  label="Br_element : 003"  # scripted group (container) (typed FeaturePython)
  n = 1
  ref = Br_element
FEATURE [App::DocumentObjectGroupPython] G4_SILVER_BROMIDE  # scripted group (container) (typed FeaturePython)
  Dunit = g/cm3
  Dvalue = 6.473
  Group = -> [Ag_element002,Br_element005]
  conduct = 2
  density = 1
  expand = 3
  formula = G4_SILVER_BROMIDE
  name = G4_SILVER_BROMIDE
  specific = 4
FEATURE [App::DocumentObjectGroupPython] Ag_element003  label="Ag_element : 002"  # scripted group (container) (typed FeaturePython)
  n = 1
  ref = Ag_element
FEATURE [App::DocumentObjectGroupPython] Cl_element022  label="Cl_element : 011"  # scripted group (container) (typed FeaturePython)
  n = 1
  ref = Cl_element
FEATURE [App::DocumentObjectGroupPython] G4_SILVER_CHLORIDE  # scripted group (container) (typed FeaturePython)
  Dunit = g/cm3
  Dvalue = 5.56
  Group = -> [Ag_element003,Cl_element022]
  conduct = 2
  density = 1
  expand = 3
  formula = G4_SILVER_CHLORIDE
  name = G4_SILVER_CHLORIDE
  specific = 4
FEATURE [App::DocumentObjectGroupPython] Br_element006  label="Br_element : 0.423"  # scripted group (container) (typed FeaturePython)
  n = 0.422895
FEATURE [App::DocumentObjectGroupPython] Ag_element004  label="Ag_element : 0.574"  # scripted group (container) (typed FeaturePython)
  n = 0.573748
FEATURE [App::DocumentObjectGroupPython] I_element007  label="I_element : 0.649"  # scripted group (container) (typed FeaturePython)
  n = 0.003357
FEATURE [App::DocumentObjectGroupPython] G4_SILVER_HALIDES  # scripted group (container) (typed FeaturePython)
  Dunit = g/cm3
  Dvalue = 6.47
  Group = -> [Br_element006,Ag_element004,I_element007]
  conduct = 2
  density = 1
  expand = 3
  formula = G4_SILVER_HALIDES
  name = G4_SILVER_HALIDES
  specific = 4
FEATURE [App::DocumentObjectGroupPython] Ag_element005  label="Ag_element : 003"  # scripted group (container) (typed FeaturePython)
  n = 1
  ref = Ag_element
FEATURE [App::DocumentObjectGroupPython] I_element008  label="I_element : 004"  # scripted group (container) (typed FeaturePython)
  n = 1
  ref = I_element
FEATURE [App::DocumentObjectGroupPython] G4_SILVER_IODIDE  # scripted group (container) (typed FeaturePython)
  Dunit = g/cm3
  Dvalue = 6.01
  Group = -> [Ag_element005,I_element008]
  conduct = 2
  density = 1
  expand = 3
  formula = G4_SILVER_IODIDE
  name = G4_SILVER_IODIDE
  specific = 4
FEATURE [App::DocumentObjectGroupPython] H_element095  label="H_element : 0.100"  # scripted group (container) (typed FeaturePython)
  n = 0.1
FEATURE [App::DocumentObjectGroupPython] C_element103  label="C_element : 0.204"  # scripted group (container) (typed FeaturePython)
  n = 0.204
FEATURE [App::DocumentObjectGroupPython] N_element039  label="N_element : 0.759"  # scripted group (container) (typed FeaturePython)
  n = 0.042
FEATURE [App::DocumentObjectGroupPython] O_element088  label="O_element : 0.645"  # scripted group (container) (typed FeaturePython)
  n = 0.645
FEATURE [App::DocumentObjectGroupPython] Na_element013  label="Na_element : 0.100"  # scripted group (container) (typed FeaturePython)
  n = 0.002
FEATURE [App::DocumentObjectGroupPython] P_element009  label="P_element : 0.107"  # scripted group (container) (typed FeaturePython)
  n = 0.001
FEATURE [App::DocumentObjectGroupPython] S_element020  label="S_element : 0.021"  # scripted group (container) (typed FeaturePython)
  n = 0.002
FEATURE [App::DocumentObjectGroupPython] Cl_element023  label="Cl_element : 0.590"  # scripted group (container) (typed FeaturePython)
  n = 0.003
FEATURE [App::DocumentObjectGroupPython] K_element010  label="K_element : 0.001"  # scripted group (container) (typed FeaturePython)
  n = 0.001
FEATURE [App::DocumentObjectGroupPython] G4_SKIN_ICRP  # scripted group (container) (typed FeaturePython)
  Dunit = g/cm3
  Dvalue = 1.09
  Group = -> [H_element095,C_element103,N_element039,O_element088,Na_element013,P_element009,S_element020,Cl_element023,K_element010]
  conduct = 2
  density = 1
  expand = 3
  formula = G4_SKIN_ICRP
  name = G4_SKIN_ICRP
  specific = 4
FEATURE [App::DocumentObjectGroupPython] Na_element014  label="Na_element : 2"  # scripted group (container) (typed FeaturePython)
  n = 2
  ref = Na_element
FEATURE [App::DocumentObjectGroupPython] C_element104  label="C_element : 058"  # scripted group (container) (typed FeaturePython)
  n = 1
  ref = C_element
FEATURE [App::DocumentObjectGroupPython] O_element089  label="O_element : 049"  # scripted group (container) (typed FeaturePython)
  n = 3
  ref = O_element
FEATURE [App::DocumentObjectGroupPython] G4_SODIUM_CARBONATE  # scripted group (container) (typed FeaturePython)
  Dunit = g/cm3
  Dvalue = 2.532
  Group = -> [Na_element014,C_element104,O_element089]
  conduct = 2
  density = 1
  expand = 3
  formula = G4_SODIUM_CARBONATE
  name = G4_SODIUM_CARBONATE
  specific = 4
FEATURE [App::DocumentObjectGroupPython] Na_element015  label="Na_element : 1"  # scripted group (container) (typed FeaturePython)
  n = 1
  ref = Na_element
FEATURE [App::DocumentObjectGroupPython] I_element009  label="I_element : 005"  # scripted group (container) (typed FeaturePython)
  n = 1
  ref = I_element
FEATURE [App::DocumentObjectGroupPython] G4_SODIUM_IODIDE  # scripted group (container) (typed FeaturePython)
  Dunit = g/cm3
  Dvalue = 3.667
  Group = -> [Na_element015,I_element009]
  conduct = 2
  density = 1
  expand = 3
  formula = G4_SODIUM_IODIDE
  name = G4_SODIUM_IODIDE
  specific = 4
FEATURE [App::DocumentObjectGroupPython] Na_element016  label="Na_element : 003"  # scripted group (container) (typed FeaturePython)
  n = 2
  ref = Na_element
FEATURE [App::DocumentObjectGroupPython] O_element090  label="O_element : 050"  # scripted group (container) (typed FeaturePython)
  n = 1
  ref = O_element
FEATURE [App::DocumentObjectGroupPython] G4_SODIUM_MONOXIDE  # scripted group (container) (typed FeaturePython)
  Dunit = g/cm3
  Dvalue = 2.27
  Group = -> [Na_element016,O_element090]
  conduct = 2
  density = 1
  expand = 3
  formula = G4_SODIUM_MONOXIDE
  name = G4_SODIUM_MONOXIDE
  specific = 4
FEATURE [App::DocumentObjectGroupPython] Na_element017  label="Na_element : 004"  # scripted group (container) (typed FeaturePython)
  n = 1
  ref = Na_element
FEATURE [App::DocumentObjectGroupPython] N_element040  label="N_element : 018"  # scripted group (container) (typed FeaturePython)
  n = 1
  ref = N_element
FEATURE [App::DocumentObjectGroupPython] O_element091  label="O_element : 051"  # scripted group (container) (typed FeaturePython)
  n = 3
  ref = O_element
FEATURE [App::DocumentObjectGroupPython] G4_SODIUM_NITRATE  # scripted group (container) (typed FeaturePython)
  Dunit = g/cm3
  Dvalue = 2.261
  Group = -> [Na_element017,N_element040,O_element091]
  conduct = 2
  density = 1
  expand = 3
  formula = G4_SODIUM_NITRATE
  name = G4_SODIUM_NITRATE
  specific = 4
FEATURE [App::DocumentObjectGroupPython] C_element105  label="C_element : 059"  # scripted group (container) (typed FeaturePython)
  n = 14
  ref = C_element
FEATURE [App::DocumentObjectGroupPython] H_element096  label="H_element : 053"  # scripted group (container) (typed FeaturePython)
  n = 12
  ref = H_element
FEATURE [App::DocumentObjectGroupPython] G4_STILBENE  # scripted group (container) (typed FeaturePython)
  Dunit = g/cm3
  Dvalue = 0.9707
  Group = -> [C_element105,H_element096]
  conduct = 2
  density = 1
  expand = 3
  formula = G4_STILBENE
  name = G4_STILBENE
  specific = 4
FEATURE [App::DocumentObjectGroupPython] C_element106  label="C_element : 12"  # scripted group (container) (typed FeaturePython)
  n = 12
  ref = C_element
FEATURE [App::DocumentObjectGroupPython] H_element097  label="H_element : 22"  # scripted group (container) (typed FeaturePython)
  n = 22
  ref = H_element
FEATURE [App::DocumentObjectGroupPython] O_element092  label="O_element : 11"  # scripted group (container) (typed FeaturePython)
  n = 11
  ref = O_element
FEATURE [App::DocumentObjectGroupPython] G4_SUCROSE  # scripted group (container) (typed FeaturePython)
  Dunit = g/cm3
  Dvalue = 1.5805
  Group = -> [C_element106,H_element097,O_element092]
  conduct = 2
  density = 1
  expand = 3
  formula = G4_SUCROSE
  name = G4_SUCROSE
  specific = 4
FEATURE [App::DocumentObjectGroupPython] C_element107  label="C_element : 18"  # scripted group (container) (typed FeaturePython)
  n = 18
  ref = C_element
FEATURE [App::DocumentObjectGroupPython] H_element098  label="H_element : 054"  # scripted group (container) (typed FeaturePython)
  n = 14
  ref = H_element
FEATURE [App::DocumentObjectGroupPython] G4_TERPHENYL  # scripted group (container) (typed FeaturePython)
  Dunit = g/cm3
  Dvalue = 1.24
  Group = -> [C_element107,H_element098]
  conduct = 2
  density = 1
  expand = 3
  formula = G4_TERPHENYL
  name = G4_TERPHENYL
  specific = 4
FEATURE [App::DocumentObjectGroupPython] H_element099  label="H_element : 0.146"  # scripted group (container) (typed FeaturePython)
  n = 0.106
FEATURE [App::DocumentObjectGroupPython] C_element108  label="C_element : 0.883"  # scripted group (container) (typed FeaturePython)
  n = 0.099
FEATURE [App::DocumentObjectGroupPython] N_element041  label="N_element : 0.020"  # scripted group (container) (typed FeaturePython)
  n = 0.02
FEATURE [App::DocumentObjectGroupPython] O_element093  label="O_element : 0.766"  # scripted group (container) (typed FeaturePython)
  n = 0.766
FEATURE [App::DocumentObjectGroupPython] Na_element018  label="Na_element : 0.101"  # scripted group (container) (typed FeaturePython)
  n = 0.002
FEATURE [App::DocumentObjectGroupPython] P_element010  label="P_element : 0.108"  # scripted group (container) (typed FeaturePython)
  n = 0.001
FEATURE [App::DocumentObjectGroupPython] S_element021  label="S_element : 0.022"  # scripted group (container) (typed FeaturePython)
  n = 0.002
FEATURE [App::DocumentObjectGroupPython] Cl_element024  label="Cl_element : 0.002"  # scripted group (container) (typed FeaturePython)
  n = 0.002
FEATURE [App::DocumentObjectGroupPython] K_element011  label="K_element : 0.017"  # scripted group (container) (typed FeaturePython)
  n = 0.002
FEATURE [App::DocumentObjectGroupPython] G4_TESTIS_ICRP  # scripted group (container) (typed FeaturePython)
  Dunit = g/cm3
  Dvalue = 1.04
  Group = -> [H_element099,C_element108,N_element041,O_element093,Na_element018,P_element010,S_element021,Cl_element024,K_element011]
  conduct = 2
  density = 1
  expand = 3
  formula = G4_TESTIS_ICRP
  name = G4_TESTIS_ICRP
  specific = 4
FEATURE [App::DocumentObjectGroupPython] C_element109  label="C_element : 060"  # scripted group (container) (typed FeaturePython)
  n = 2
  ref = C_element
FEATURE [App::DocumentObjectGroupPython] Cl_element025  label="Cl_element : 012"  # scripted group (container) (typed FeaturePython)
  n = 4
  ref = Cl_element
FEATURE [App::DocumentObjectGroupPython] G4_TETRACHLOROETHYLENE  # scripted group (container) (typed FeaturePython)
  Dunit = g/cm3
  Dvalue = 1.625
  Group = -> [C_element109,Cl_element025]
  conduct = 2
  density = 1
  expand = 3
  formula = G4_TETRACHLOROETHYLENE
  name = G4_TETRACHLOROETHYLENE
  specific = 4
FEATURE [App::DocumentObjectGroupPython] Tl_element001  label="Tl_element : 1"  # scripted group (container) (typed FeaturePython)
  n = 1
  ref = Tl_element
FEATURE [App::DocumentObjectGroupPython] Cl_element026  label="Cl_element : 013"  # scripted group (container) (typed FeaturePython)
  n = 1
  ref = Cl_element
FEATURE [App::DocumentObjectGroupPython] G4_THALLIUM_CHLORIDE  # scripted group (container) (typed FeaturePython)
  Dunit = g/cm3
  Dvalue = 7.004
  Group = -> [Tl_element001,Cl_element026]
  conduct = 2
  density = 1
  expand = 3
  formula = G4_THALLIUM_CHLORIDE
  name = G4_THALLIUM_CHLORIDE
  specific = 4
FEATURE [App::DocumentObjectGroupPython] H_element100  label="H_element : 0.147"  # scripted group (container) (typed FeaturePython)
  n = 0.105
FEATURE [App::DocumentObjectGroupPython] C_element110  label="C_element : 0.256"  # scripted group (container) (typed FeaturePython)
  n = 0.256
FEATURE [App::DocumentObjectGroupPython] N_element042  label="N_element : 0.760"  # scripted group (container) (typed FeaturePython)
  n = 0.027
FEATURE [App::DocumentObjectGroupPython] O_element094  label="O_element : 0.602"  # scripted group (container) (typed FeaturePython)
  n = 0.602
FEATURE [App::DocumentObjectGroupPython] Na_element019  label="Na_element : 0.102"  # scripted group (container) (typed FeaturePython)
  n = 0.001
FEATURE [App::DocumentObjectGroupPython] P_element011  label="P_element : 0.109"  # scripted group (container) (typed FeaturePython)
  n = 0.002
FEATURE [App::DocumentObjectGroupPython] S_element022  label="S_element : 0.023"  # scripted group (container) (typed FeaturePython)
  n = 0.003
FEATURE [App::DocumentObjectGroupPython] Cl_element027  label="Cl_element : 0.591"  # scripted group (container) (typed FeaturePython)
  n = 0.002
FEATURE [App::DocumentObjectGroupPython] K_element012  label="K_element : 0.018"  # scripted group (container) (typed FeaturePython)
  n = 0.002
FEATURE [App::DocumentObjectGroupPython] G4_TISSUE_SOFT_ICRP  # scripted group (container) (typed FeaturePython)
  Dunit = g/cm3
  Dvalue = 1.03
  Group = -> [H_element100,C_element110,N_element042,O_element094,Na_element019,P_element011,S_element022,Cl_element027,K_element012]
  conduct = 2
  density = 1
  expand = 3
  formula = G4_TISSUE_SOFT_ICRP
  name = G4_TISSUE_SOFT_ICRP
  specific = 4
FEATURE [App::DocumentObjectGroupPython] H_element101  label="H_element : 0.148"  # scripted group (container) (typed FeaturePython)
  n = 0.101
FEATURE [App::DocumentObjectGroupPython] C_element111  label="C_element : 0.111"  # scripted group (container) (typed FeaturePython)
  n = 0.111
FEATURE [App::DocumentObjectGroupPython] N_element043  label="N_element : 0.026"  # scripted group (container) (typed FeaturePython)
  n = 0.026
FEATURE [App::DocumentObjectGroupPython] O_element095  label="O_element : 0.762"  # scripted group (container) (typed FeaturePython)
  n = 0.762
FEATURE [App::DocumentObjectGroupPython] G4_TISSUE_SOFT_ICRU_4  label="G4_TISSUE_SOFT_ICRU-4"  # scripted group (container) (typed FeaturePython)
  Dunit = g/cm3
  Dvalue = 1
  Group = -> [H_element101,C_element111,N_element043,O_element095]
  conduct = 2
  density = 1
  expand = 3
  formula = G4_TISSUE_SOFT_ICRU-4
  name = G4_TISSUE_SOFT_ICRU-4
  specific = 4
FEATURE [App::DocumentObjectGroupPython] H_element102  label="H_element : 0.149"  # scripted group (container) (typed FeaturePython)
  n = 0.101869
FEATURE [App::DocumentObjectGroupPython] C_element112  label="C_element : 0.456"  # scripted group (container) (typed FeaturePython)
  n = 0.456179
FEATURE [App::DocumentObjectGroupPython] N_element044  label="N_element : 0.761"  # scripted group (container) (typed FeaturePython)
  n = 0.035172
FEATURE [App::DocumentObjectGroupPython] O_element096  label="O_element : 0.407"  # scripted group (container) (typed FeaturePython)
  n = 0.40678
FEATURE [App::DocumentObjectGroupPython] G4_TISSUE_METHANE  label="G4_TISSUE-METHANE"  # scripted group (container) (typed FeaturePython)
  Dunit = g/cm3
  Dvalue = 0.00106409
  Group = -> [H_element102,C_element112,N_element044,O_element096]
  conduct = 2
  density = 1
  expand = 3
  formula = G4_TISSUE-METHANE
  name = G4_TISSUE-METHANE
  specific = 4
FEATURE [App::DocumentObjectGroupPython] H_element103  label="H_element : 0.103"  # scripted group (container) (typed FeaturePython)
  n = 0.102672
FEATURE [App::DocumentObjectGroupPython] C_element113  label="C_element : 0.569"  # scripted group (container) (typed FeaturePython)
  n = 0.56894
FEATURE [App::DocumentObjectGroupPython] N_element045  label="N_element : 0.762"  # scripted group (container) (typed FeaturePython)
  n = 0.035022
FEATURE [App::DocumentObjectGroupPython] O_element097  label="O_element : 0.293"  # scripted group (container) (typed FeaturePython)
  n = 0.293366
FEATURE [App::DocumentObjectGroupPython] G4_TISSUE_PROPANE  label="G4_TISSUE-PROPANE"  # scripted group (container) (typed FeaturePython)
  Dunit = g/cm3
  Dvalue = 0.00182628
  Group = -> [H_element103,C_element113,N_element045,O_element097]
  conduct = 2
  density = 1
  expand = 3
  formula = G4_TISSUE-PROPANE
  name = G4_TISSUE-PROPANE
  specific = 4
FEATURE [App::DocumentObjectGroupPython] Ti_element003  label="Ti_element : 1"  # scripted group (container) (typed FeaturePython)
  n = 1
  ref = Ti_element
FEATURE [App::DocumentObjectGroupPython] O_element098  label="O_element : 052"  # scripted group (container) (typed FeaturePython)
  n = 2
  ref = O_element
FEATURE [App::DocumentObjectGroupPython] G4_TITANIUM_DIOXIDE  # scripted group (container) (typed FeaturePython)
  Dunit = g/cm3
  Dvalue = 4.26
  Group = -> [Ti_element003,O_element098]
  conduct = 2
  density = 1
  expand = 3
  formula = G4_TITANIUM_DIOXIDE
  name = G4_TITANIUM_DIOXIDE
  specific = 4
FEATURE [App::DocumentObjectGroupPython] C_element114  label="C_element : 061"  # scripted group (container) (typed FeaturePython)
  n = 7
  ref = C_element
FEATURE [App::DocumentObjectGroupPython] H_element104  label="H_element : 055"  # scripted group (container) (typed FeaturePython)
  n = 8
  ref = H_element
FEATURE [App::DocumentObjectGroupPython] G4_TOLUENE  # scripted group (container) (typed FeaturePython)
  Dunit = g/cm3
  Dvalue = 0.8669
  Group = -> [C_element114,H_element104]
  conduct = 2
  density = 1
  expand = 3
  formula = G4_TOLUENE
  name = G4_TOLUENE
  specific = 4
FEATURE [App::DocumentObjectGroupPython] C_element115  label="C_element : 062"  # scripted group (container) (typed FeaturePython)
  n = 2
  ref = C_element
FEATURE [App::DocumentObjectGroupPython] H_element105  label="H_element : 056"  # scripted group (container) (typed FeaturePython)
  n = 1
  ref = H_element
FEATURE [App::DocumentObjectGroupPython] Cl_element028  label="Cl_element : 014"  # scripted group (container) (typed FeaturePython)
  n = 3
  ref = Cl_element
FEATURE [App::DocumentObjectGroupPython] G4_TRICHLOROETHYLENE  # scripted group (container) (typed FeaturePython)
  Dunit = g/cm3
  Dvalue = 1.46
  Group = -> [C_element115,H_element105,Cl_element028]
  conduct = 2
  density = 1
  expand = 3
  formula = G4_TRICHLOROETHYLENE
  name = G4_TRICHLOROETHYLENE
  specific = 4
FEATURE [App::DocumentObjectGroupPython] C_element116  label="C_element : 063"  # scripted group (container) (typed FeaturePython)
  n = 6
  ref = C_element
FEATURE [App::DocumentObjectGroupPython] H_element106  label="H_element : 15"  # scripted group (container) (typed FeaturePython)
  n = 15
  ref = H_element
FEATURE [App::DocumentObjectGroupPython] O_element099  label="O_element : 053"  # scripted group (container) (typed FeaturePython)
  n = 4
  ref = O_element
FEATURE [App::DocumentObjectGroupPython] P_element012  label="P_element : 1"  # scripted group (container) (typed FeaturePython)
  n = 1
  ref = P_element
FEATURE [App::DocumentObjectGroupPython] G4_TRIETHYL_PHOSPHATE  # scripted group (container) (typed FeaturePython)
  Dunit = g/cm3
  Dvalue = 1.07
  Group = -> [C_element116,H_element106,O_element099,P_element012]
  conduct = 2
  density = 1
  expand = 3
  formula = G4_TRIETHYL_PHOSPHATE
  name = G4_TRIETHYL_PHOSPHATE
  specific = 4
FEATURE [App::DocumentObjectGroupPython] W_element003  label="W_element : 003"  # scripted group (container) (typed FeaturePython)
  n = 1
  ref = W_element
FEATURE [App::DocumentObjectGroupPython] F_element017  label="F_element : 6"  # scripted group (container) (typed FeaturePython)
  n = 6
  ref = F_element
FEATURE [App::DocumentObjectGroupPython] G4_TUNGSTEN_HEXAFLUORIDE  # scripted group (container) (typed FeaturePython)
  Dunit = g/cm3
  Dvalue = 2.4
  Group = -> [W_element003,F_element017]
  conduct = 2
  density = 1
  expand = 3
  formula = G4_TUNGSTEN_HEXAFLUORIDE
  name = G4_TUNGSTEN_HEXAFLUORIDE
  specific = 4
FEATURE [App::DocumentObjectGroupPython] U_element001  label="U_element : 1"  # scripted group (container) (typed FeaturePython)
  n = 1
  ref = U_element
FEATURE [App::DocumentObjectGroupPython] C_element117  label="C_element : 064"  # scripted group (container) (typed FeaturePython)
  n = 2
  ref = C_element
FEATURE [App::DocumentObjectGroupPython] G4_URANIUM_DICARBIDE  # scripted group (container) (typed FeaturePython)
  Dunit = g/cm3
  Dvalue = 11.28
  Group = -> [U_element001,C_element117]
  conduct = 2
  density = 1
  expand = 3
  formula = G4_URANIUM_DICARBIDE
  name = G4_URANIUM_DICARBIDE
  specific = 4
FEATURE [App::DocumentObjectGroupPython] U_element002  label="U_element : 002"  # scripted group (container) (typed FeaturePython)
  n = 1
  ref = U_element
FEATURE [App::DocumentObjectGroupPython] C_element118  label="C_element : 065"  # scripted group (container) (typed FeaturePython)
  n = 1
  ref = C_element
FEATURE [App::DocumentObjectGroupPython] G4_URANIUM_MONOCARBIDE  # scripted group (container) (typed FeaturePython)
  Dunit = g/cm3
  Dvalue = 13.63
  Group = -> [U_element002,C_element118]
  conduct = 2
  density = 1
  expand = 3
  formula = G4_URANIUM_MONOCARBIDE
  name = G4_URANIUM_MONOCARBIDE
  specific = 4
FEATURE [App::DocumentObjectGroupPython] U_element003  label="U_element : 003"  # scripted group (container) (typed FeaturePython)
  n = 1
  ref = U_element
FEATURE [App::DocumentObjectGroupPython] O_element100  label="O_element : 054"  # scripted group (container) (typed FeaturePython)
  n = 2
  ref = O_element
FEATURE [App::DocumentObjectGroupPython] G4_URANIUM_OXIDE  # scripted group (container) (typed FeaturePython)
  Dunit = g/cm3
  Dvalue = 10.96
  Group = -> [U_element003,O_element100]
  conduct = 2
  density = 1
  expand = 3
  formula = G4_URANIUM_OXIDE
  name = G4_URANIUM_OXIDE
  specific = 4
FEATURE [App::DocumentObjectGroupPython] C_element119  label="C_element : 066"  # scripted group (container) (typed FeaturePython)
  n = 1
  ref = C_element
FEATURE [App::DocumentObjectGroupPython] H_element107  label="H_element : 057"  # scripted group (container) (typed FeaturePython)
  n = 4
  ref = H_element
FEATURE [App::DocumentObjectGroupPython] N_element046  label="N_element : 019"  # scripted group (container) (typed FeaturePython)
  n = 2
  ref = N_element
FEATURE [App::DocumentObjectGroupPython] O_element101  label="O_element : 055"  # scripted group (container) (typed FeaturePython)
  n = 1
  ref = O_element
FEATURE [App::DocumentObjectGroupPython] G4_UREA  # scripted group (container) (typed FeaturePython)
  Dunit = g/cm3
  Dvalue = 1.323
  Group = -> [C_element119,H_element107,N_element046,O_element101]
  conduct = 2
  density = 1
  expand = 3
  formula = G4_UREA
  name = G4_UREA
  specific = 4
FEATURE [App::DocumentObjectGroupPython] C_element120  label="C_element : 067"  # scripted group (container) (typed FeaturePython)
  n = 5
  ref = C_element
FEATURE [App::DocumentObjectGroupPython] H_element108  label="H_element : 058"  # scripted group (container) (typed FeaturePython)
  n = 11
  ref = H_element
FEATURE [App::DocumentObjectGroupPython] N_element047  label="N_element : 020"  # scripted group (container) (typed FeaturePython)
  n = 1
  ref = N_element
FEATURE [App::DocumentObjectGroupPython] O_element102  label="O_element : 056"  # scripted group (container) (typed FeaturePython)
  n = 2
  ref = O_element
FEATURE [App::DocumentObjectGroupPython] G4_VALINE  # scripted group (container) (typed FeaturePython)
  Dunit = g/cm3
  Dvalue = 1.23
  Group = -> [C_element120,H_element108,N_element047,O_element102]
  conduct = 2
  density = 1
  expand = 3
  formula = G4_VALINE
  name = G4_VALINE
  specific = 4
FEATURE [App::DocumentObjectGroupPython] H_element109  label="H_element : 0.009"  # scripted group (container) (typed FeaturePython)
  n = 0.009417
FEATURE [App::DocumentObjectGroupPython] C_element121  label="C_element : 0.281"  # scripted group (container) (typed FeaturePython)
  n = 0.280555
FEATURE [App::DocumentObjectGroupPython] F_element018  label="F_element : 0.710"  # scripted group (container) (typed FeaturePython)
  n = 0.710028
FEATURE [App::DocumentObjectGroupPython] G4_VITON  # scripted group (container) (typed FeaturePython)
  Dunit = g/cm3
  Dvalue = 1.8
  Group = -> [H_element109,C_element121,F_element018]
  conduct = 2
  density = 1
  expand = 3
  formula = G4_VITON
  name = G4_VITON
  specific = 4
FEATURE [App::DocumentObjectGroupPython] H_element110  label="H_element : 059"  # scripted group (container) (typed FeaturePython)
  n = 2
  ref = H_element
FEATURE [App::DocumentObjectGroupPython] O_element103  label="O_element : 057"  # scripted group (container) (typed FeaturePython)
  n = 1
  ref = O_element
FEATURE [App::DocumentObjectGroupPython] G4_WATER  # scripted group (container) (typed FeaturePython)
  Dunit = g/cm3
  Dvalue = 1
  Group = -> [H_element110,O_element103]
  conduct = 2
  density = 1
  expand = 3
  formula = G4_WATER
  name = G4_WATER
  specific = 4
FEATURE [App::DocumentObjectGroupPython] H_element111  label="H_element : 060"  # scripted group (container) (typed FeaturePython)
  n = 2
  ref = H_element
FEATURE [App::DocumentObjectGroupPython] O_element104  label="O_element : 058"  # scripted group (container) (typed FeaturePython)
  n = 1
  ref = O_element
FEATURE [App::DocumentObjectGroupPython] G4_WATER_VAPOR  # scripted group (container) (typed FeaturePython)
  Dunit = g/cm3
  Dvalue = 0.000756182
  Group = -> [H_element111,O_element104]
  conduct = 2
  density = 1
  expand = 3
  formula = G4_WATER_VAPOR
  name = G4_WATER_VAPOR
  specific = 4
FEATURE [App::DocumentObjectGroupPython] C_element122  label="C_element : 068"  # scripted group (container) (typed FeaturePython)
  n = 8
  ref = C_element
FEATURE [App::DocumentObjectGroupPython] H_element112  label="H_element : 061"  # scripted group (container) (typed FeaturePython)
  n = 10
  ref = H_element
FEATURE [App::DocumentObjectGroupPython] G4_XYLENE  # scripted group (container) (typed FeaturePython)
  Dunit = g/cm3
  Dvalue = 0.87
  Group = -> [C_element122,H_element112]
  conduct = 2
  density = 1
  expand = 3
  formula = G4_XYLENE
  name = G4_XYLENE
  specific = 4
FEATURE [App::DocumentObjectGroupPython] C_element123  label="C_element : 069"  # scripted group (container) (typed FeaturePython)
  n = 1
  ref = C_element
FEATURE [App::DocumentObjectGroupPython] G4_GRAPHITE  # scripted group (container) (typed FeaturePython)
  Dunit = g/cm3
  Dvalue = 2.21
  Group = -> [C_element123]
  conduct = 2
  density = 1
  expand = 3
  formula = G4_GRAPHITE
  name = G4_GRAPHITE
  specific = 4
FEATURE [App::DocumentObjectGroupPython] NIST  # scripted group (container) (typed FeaturePython)
  Group = -> [G4_A_150_TISSUE,G4_ACETONE,G4_ACETYLENE,G4_ADENINE,G4_ADIPOSE_TISSUE_ICRP,G4_AIR,G4_ALANINE,G4_ALUMINUM_OXIDE,G4_AMBER,G4_AMMONIA,G4_ANILINE,G4_ANTHRACENE,G4_B_100_BONE,G4_BAKELITE,G4_BARIUM_FLUORIDE,G4_BARIUM_SULFATE,G4_BENZENE,G4_BERYLLIUM_OXIDE,G4_BGO,G4_BLOOD_ICRP,G4_BONE_COMPACT_ICRU,G4_BONE_CORTICAL_ICRP,G4_BORON_CARBIDE,G4_BORON_OXIDE,G4_BRAIN_ICRP,G4_BUTANE,G4_N_BUTYL_ALCOHOL,G4_C_552,+152 more]
FEATURE [App::DocumentObjectGroupPython] H_element113  label="H_element : 062"  # scripted group (container) (typed FeaturePython)
  n = 1
  ref = H_element
FEATURE [App::DocumentObjectGroupPython] G4_H  # scripted group (container) (typed FeaturePython)
  Dunit = g/cm3
  Dvalue = 8.3748e-05
  Group = -> [H_element113]
  conduct = 2
  density = 1
  expand = 3
  formula = H
  name = G4_H
  specific = 4
FEATURE [App::DocumentObjectGroupPython] He_element001  label="He_element : 1"  # scripted group (container) (typed FeaturePython)
  n = 1
  ref = He_element
FEATURE [App::DocumentObjectGroupPython] G4_He  # scripted group (container) (typed FeaturePython)
  Dunit = g/cm3
  Dvalue = 0.000166322
  Group = -> [He_element001]
  conduct = 2
  density = 1
  expand = 3
  formula = He
  name = G4_He
  specific = 4
FEATURE [App::DocumentObjectGroupPython] Li_element008  label="Li_element : 008"  # scripted group (container) (typed FeaturePython)
  n = 1
  ref = Li_element
FEATURE [App::DocumentObjectGroupPython] G4_Li  # scripted group (container) (typed FeaturePython)
  Dunit = g/cm3
  Dvalue = 0.534
  Group = -> [Li_element008]
  conduct = 2
  density = 1
  expand = 3
  formula = Li
  name = G4_Li
  specific = 4
FEATURE [App::DocumentObjectGroupPython] Be_element002  label="Be_element : 002"  # scripted group (container) (typed FeaturePython)
  n = 1
  ref = Be_element
FEATURE [App::DocumentObjectGroupPython] G4_Be  # scripted group (container) (typed FeaturePython)
  Dunit = g/cm3
  Dvalue = 1.848
  Group = -> [Be_element002]
  conduct = 2
  density = 1
  expand = 3
  formula = Be
  name = G4_Be
  specific = 4
FEATURE [App::DocumentObjectGroupPython] B_element007  label="B_element : 007"  # scripted group (container) (typed FeaturePython)
  n = 1
  ref = B_element
FEATURE [App::DocumentObjectGroupPython] G4_B  # scripted group (container) (typed FeaturePython)
  Dunit = g/cm3
  Dvalue = 2.37
  Group = -> [B_element007]
  conduct = 2
  density = 1
  expand = 3
  formula = B
  name = G4_B
  specific = 4
FEATURE [App::DocumentObjectGroupPython] C_element124  label="C_element : 070"  # scripted group (container) (typed FeaturePython)
  n = 1
  ref = C_element
FEATURE [App::DocumentObjectGroupPython] G4_C  # scripted group (container) (typed FeaturePython)
  Dunit = g/cm3
  Dvalue = 2
  Group = -> [C_element124]
  conduct = 2
  density = 1
  expand = 3
  formula = C
  name = G4_C
  specific = 4
FEATURE [App::DocumentObjectGroupPython] N_element048  label="N_element : 021"  # scripted group (container) (typed FeaturePython)
  n = 1
  ref = N_element
FEATURE [App::DocumentObjectGroupPython] G4_N  # scripted group (container) (typed FeaturePython)
  Dunit = g/cm3
  Dvalue = 0.0011652
  Group = -> [N_element048]
  conduct = 2
  density = 1
  expand = 3
  formula = N
  name = G4_N
  specific = 4
FEATURE [App::DocumentObjectGroupPython] O_element105  label="O_element : 059"  # scripted group (container) (typed FeaturePython)
  n = 1
  ref = O_element
FEATURE [App::DocumentObjectGroupPython] G4_O  # scripted group (container) (typed FeaturePython)
  Dunit = g/cm3
  Dvalue = 0.00133151
  Group = -> [O_element105]
  conduct = 2
  density = 1
  expand = 3
  formula = O
  name = G4_O
  specific = 4
FEATURE [App::DocumentObjectGroupPython] F_element019  label="F_element : 008"  # scripted group (container) (typed FeaturePython)
  n = 1
  ref = F_element
FEATURE [App::DocumentObjectGroupPython] G4_F  # scripted group (container) (typed FeaturePython)
  Dunit = g/cm3
  Dvalue = 0.00158029
  Group = -> [F_element019]
  conduct = 2
  density = 1
  expand = 3
  formula = F
  name = G4_F
  specific = 4
FEATURE [App::DocumentObjectGroupPython] Ne_element001  label="Ne_element : 1"  # scripted group (container) (typed FeaturePython)
  n = 1
  ref = Ne_element
FEATURE [App::DocumentObjectGroupPython] G4_Ne  # scripted group (container) (typed FeaturePython)
  Dunit = g/cm3
  Dvalue = 0.000838505
  Group = -> [Ne_element001]
  conduct = 2
  density = 1
  expand = 3
  formula = Ne
  name = G4_Ne
  specific = 4
FEATURE [App::DocumentObjectGroupPython] Na_element020  label="Na_element : 005"  # scripted group (container) (typed FeaturePython)
  n = 1
  ref = Na_element
FEATURE [App::DocumentObjectGroupPython] G4_Na  # scripted group (container) (typed FeaturePython)
  Dunit = g/cm3
  Dvalue = 0.971
  Group = -> [Na_element020]
  conduct = 2
  density = 1
  expand = 3
  formula = Na
  name = G4_Na
  specific = 4
FEATURE [App::DocumentObjectGroupPython] Mg_element011  label="Mg_element : 005"  # scripted group (container) (typed FeaturePython)
  n = 1
  ref = Mg_element
FEATURE [App::DocumentObjectGroupPython] G4_Mg  # scripted group (container) (typed FeaturePython)
  Dunit = g/cm3
  Dvalue = 1.74
  Group = -> [Mg_element011]
  conduct = 2
  density = 1
  expand = 3
  formula = Mg
  name = G4_Mg
  specific = 4
FEATURE [App::DocumentObjectGroupPython] Al_element004  label="Al_element : 1"  # scripted group (container) (typed FeaturePython)
  n = 1
  ref = Al_element
FEATURE [App::DocumentObjectGroupPython] G4_Al  # scripted group (container) (typed FeaturePython)
  Dunit = g/cm3
  Dvalue = 2.699
  Group = -> [Al_element004]
  conduct = 2
  density = 1
  expand = 3
  formula = Al
  name = G4_Al
  specific = 4
FEATURE [App::DocumentObjectGroupPython] Si_element007  label="Si_element : 002"  # scripted group (container) (typed FeaturePython)
  n = 1
  ref = Si_element
FEATURE [App::DocumentObjectGroupPython] G4_Si  # scripted group (container) (typed FeaturePython)
  Dunit = g/cm3
  Dvalue = 2.33
  Group = -> [Si_element007]
  conduct = 2
  density = 1
  expand = 3
  formula = Si
  name = G4_Si
  specific = 4
FEATURE [App::DocumentObjectGroupPython] P_element013  label="P_element : 002"  # scripted group (container) (typed FeaturePython)
  n = 1
  ref = P_element
FEATURE [App::DocumentObjectGroupPython] G4_P  # scripted group (container) (typed FeaturePython)
  Dunit = g/cm3
  Dvalue = 2.2
  Group = -> [P_element013]
  conduct = 2
  density = 1
  expand = 3
  formula = P
  name = G4_P
  specific = 4
FEATURE [App::DocumentObjectGroupPython] S_element023  label="S_element : 007"  # scripted group (container) (typed FeaturePython)
  n = 1
  ref = S_element
FEATURE [App::DocumentObjectGroupPython] G4_S  # scripted group (container) (typed FeaturePython)
  Dunit = g/cm3
  Dvalue = 2
  Group = -> [S_element023]
  conduct = 2
  density = 1
  expand = 3
  formula = S
  name = G4_S
  specific = 4
FEATURE [App::DocumentObjectGroupPython] Cl_element029  label="Cl_element : 015"  # scripted group (container) (typed FeaturePython)
  n = 1
  ref = Cl_element
FEATURE [App::DocumentObjectGroupPython] G4_Cl  # scripted group (container) (typed FeaturePython)
  Dunit = g/cm3
  Dvalue = 0.00299473
  Group = -> [Cl_element029]
  conduct = 2
  density = 1
  expand = 3
  formula = Cl
  name = G4_Cl
  specific = 4
FEATURE [App::DocumentObjectGroupPython] Ar_element002  label="Ar_element : 1"  # scripted group (container) (typed FeaturePython)
  n = 1
  ref = Ar_element
FEATURE [App::DocumentObjectGroupPython] G4_Ar  # scripted group (container) (typed FeaturePython)
  Dunit = g/cm3
  Dvalue = 0.00166201
  Group = -> [Ar_element002]
  conduct = 2
  density = 1
  expand = 3
  formula = Ar
  name = G4_Ar
  specific = 4
FEATURE [App::DocumentObjectGroupPython] K_element013  label="K_element : 003"  # scripted group (container) (typed FeaturePython)
  n = 1
  ref = K_element
FEATURE [App::DocumentObjectGroupPython] G4_K  # scripted group (container) (typed FeaturePython)
  Dunit = g/cm3
  Dvalue = 0.862
  Group = -> [K_element013]
  conduct = 2
  density = 1
  expand = 3
  formula = K
  name = G4_K
  specific = 4
FEATURE [App::DocumentObjectGroupPython] Ca_element014  label="Ca_element : 007"  # scripted group (container) (typed FeaturePython)
  n = 1
  ref = Ca_element
FEATURE [App::DocumentObjectGroupPython] G4_Ca  # scripted group (container) (typed FeaturePython)
  Dunit = g/cm3
  Dvalue = 1.55
  Group = -> [Ca_element014]
  conduct = 2
  density = 1
  expand = 3
  formula = Ca
  name = G4_Ca
  specific = 4
FEATURE [App::DocumentObjectGroupPython] Sc_element001  label="Sc_element : 1"  # scripted group (container) (typed FeaturePython)
  n = 1
  ref = Sc_element
FEATURE [App::DocumentObjectGroupPython] G4_Sc  # scripted group (container) (typed FeaturePython)
  Dunit = g/cm3
  Dvalue = 2.989
  Group = -> [Sc_element001]
  conduct = 2
  density = 1
  expand = 3
  formula = Sc
  name = G4_Sc
  specific = 4
FEATURE [App::DocumentObjectGroupPython] Ti_element004  label="Ti_element : 002"  # scripted group (container) (typed FeaturePython)
  n = 1
  ref = Ti_element
FEATURE [App::DocumentObjectGroupPython] G4_Ti  # scripted group (container) (typed FeaturePython)
  Dunit = g/cm3
  Dvalue = 4.54
  Group = -> [Ti_element004]
  conduct = 2
  density = 1
  expand = 3
  formula = Ti
  name = G4_Ti
  specific = 4
FEATURE [App::DocumentObjectGroupPython] V_element001  label="V_element : 1"  # scripted group (container) (typed FeaturePython)
  n = 1
  ref = V_element
FEATURE [App::DocumentObjectGroupPython] G4_V  # scripted group (container) (typed FeaturePython)
  Dunit = g/cm3
  Dvalue = 6.11
  Group = -> [V_element001]
  conduct = 2
  density = 1
  expand = 3
  formula = V
  name = G4_V
  specific = 4
FEATURE [App::DocumentObjectGroupPython] Cr_element001  label="Cr_element : 1"  # scripted group (container) (typed FeaturePython)
  n = 1
  ref = Cr_element
FEATURE [App::DocumentObjectGroupPython] G4_Cr  # scripted group (container) (typed FeaturePython)
  Dunit = g/cm3
  Dvalue = 7.18
  Group = -> [Cr_element001]
  conduct = 2
  density = 1
  expand = 3
  formula = Cr
  name = G4_Cr
  specific = 4
FEATURE [App::DocumentObjectGroupPython] Mn_element001  label="Mn_element : 1"  # scripted group (container) (typed FeaturePython)
  n = 1
  ref = Mn_element
FEATURE [App::DocumentObjectGroupPython] G4_Mn  # scripted group (container) (typed FeaturePython)
  Dunit = g/cm3
  Dvalue = 7.44
  Group = -> [Mn_element001]
  conduct = 2
  density = 1
  expand = 3
  formula = Mn
  name = G4_Mn
  specific = 4
FEATURE [App::DocumentObjectGroupPython] Fe_element007  label="Fe_element : 004"  # scripted group (container) (typed FeaturePython)
  n = 1
  ref = Fe_element
FEATURE [App::DocumentObjectGroupPython] G4_Fe  # scripted group (container) (typed FeaturePython)
  Dunit = g/cm3
  Dvalue = 7.874
  Group = -> [Fe_element007]
  conduct = 2
  density = 1
  expand = 3
  formula = Fe
  name = G4_Fe
  specific = 4
FEATURE [App::DocumentObjectGroupPython] Co_element001  label="Co_element : 1"  # scripted group (container) (typed FeaturePython)
  n = 1
  ref = Co_element
FEATURE [App::DocumentObjectGroupPython] G4_Co  # scripted group (container) (typed FeaturePython)
  Dunit = g/cm3
  Dvalue = 8.9
  Group = -> [Co_element001]
  conduct = 2
  density = 1
  expand = 3
  formula = Co
  name = G4_Co
  specific = 4
FEATURE [App::DocumentObjectGroupPython] Ni_element001  label="Ni_element : 1"  # scripted group (container) (typed FeaturePython)
  n = 1
  ref = Ni_element
FEATURE [App::DocumentObjectGroupPython] G4_Ni  # scripted group (container) (typed FeaturePython)
  Dunit = g/cm3
  Dvalue = 8.902
  Group = -> [Ni_element001]
  conduct = 2
  density = 1
  expand = 3
  formula = Ni
  name = G4_Ni
  specific = 4
FEATURE [App::DocumentObjectGroupPython] Cu_element001  label="Cu_element : 1"  # scripted group (container) (typed FeaturePython)
  n = 1
  ref = Cu_element
FEATURE [App::DocumentObjectGroupPython] G4_Cu  # scripted group (container) (typed FeaturePython)
  Dunit = g/cm3
  Dvalue = 8.96
  Group = -> [Cu_element001]
  conduct = 2
  density = 1
  expand = 3
  formula = Cu
  name = G4_Cu
  specific = 4
FEATURE [App::DocumentObjectGroupPython] Zn_element001  label="Zn_element : 1"  # scripted group (container) (typed FeaturePython)
  n = 1
  ref = Zn_element
FEATURE [App::DocumentObjectGroupPython] G4_Zn  # scripted group (container) (typed FeaturePython)
  Dunit = g/cm3
  Dvalue = 7.133
  Group = -> [Zn_element001]
  conduct = 2
  density = 1
  expand = 3
  formula = Zn
  name = G4_Zn
  specific = 4
FEATURE [App::DocumentObjectGroupPython] Ga_element002  label="Ga_element : 002"  # scripted group (container) (typed FeaturePython)
  n = 1
  ref = Ga_element
FEATURE [App::DocumentObjectGroupPython] G4_Ga  # scripted group (container) (typed FeaturePython)
  Dunit = g/cm3
  Dvalue = 5.904
  Group = -> [Ga_element002]
  conduct = 2
  density = 1
  expand = 3
  formula = Ga
  name = G4_Ga
  specific = 4
FEATURE [App::DocumentObjectGroupPython] Ge_element002  label="Ge_element : 1"  # scripted group (container) (typed FeaturePython)
  n = 1
  ref = Ge_element
FEATURE [App::DocumentObjectGroupPython] G4_Ge  # scripted group (container) (typed FeaturePython)
  Dunit = g/cm3
  Dvalue = 5.323
  Group = -> [Ge_element002]
  conduct = 2
  density = 1
  expand = 3
  formula = Ge
  name = G4_Ge
  specific = 4
FEATURE [App::DocumentObjectGroupPython] As_element003  label="As_element : 002"  # scripted group (container) (typed FeaturePython)
  n = 1
  ref = As_element
FEATURE [App::DocumentObjectGroupPython] G4_As  # scripted group (container) (typed FeaturePython)
  Dunit = g/cm3
  Dvalue = 5.73
  Group = -> [As_element003]
  conduct = 2
  density = 1
  expand = 3
  formula = As
  name = G4_As
  specific = 4
FEATURE [App::DocumentObjectGroupPython] Se_element001  label="Se_element : 1"  # scripted group (container) (typed FeaturePython)
  n = 1
  ref = Se_element
FEATURE [App::DocumentObjectGroupPython] G4_Se  # scripted group (container) (typed FeaturePython)
  Dunit = g/cm3
  Dvalue = 4.5
  Group = -> [Se_element001]
  conduct = 2
  density = 1
  expand = 3
  formula = Se
  name = G4_Se
  specific = 4
FEATURE [App::DocumentObjectGroupPython] Br_element007  label="Br_element : 004"  # scripted group (container) (typed FeaturePython)
  n = 1
  ref = Br_element
FEATURE [App::DocumentObjectGroupPython] G4_Br  # scripted group (container) (typed FeaturePython)
  Dunit = g/cm3
  Dvalue = 0.0070721
  Group = -> [Br_element007]
  conduct = 2
  density = 1
  expand = 3
  formula = Br
  name = G4_Br
  specific = 4
FEATURE [App::DocumentObjectGroupPython] Kr_element001  label="Kr_element : 1"  # scripted group (container) (typed FeaturePython)
  n = 1
  ref = Kr_element
FEATURE [App::DocumentObjectGroupPython] G4_Kr  # scripted group (container) (typed FeaturePython)
  Dunit = g/cm3
  Dvalue = 0.00347832
  Group = -> [Kr_element001]
  conduct = 2
  density = 1
  expand = 3
  formula = Kr
  name = G4_Kr
  specific = 4
FEATURE [App::DocumentObjectGroupPython] Rb_element001  label="Rb_element : 1"  # scripted group (container) (typed FeaturePython)
  n = 1
  ref = Rb_element
FEATURE [App::DocumentObjectGroupPython] G4_Rb  # scripted group (container) (typed FeaturePython)
  Dunit = g/cm3
  Dvalue = 1.532
  Group = -> [Rb_element001]
  conduct = 2
  density = 1
  expand = 3
  formula = Rb
  name = G4_Rb
  specific = 4
FEATURE [App::DocumentObjectGroupPython] Sr_element001  label="Sr_element : 1"  # scripted group (container) (typed FeaturePython)
  n = 1
  ref = Sr_element
FEATURE [App::DocumentObjectGroupPython] G4_Sr  # scripted group (container) (typed FeaturePython)
  Dunit = g/cm3
  Dvalue = 2.54
  Group = -> [Sr_element001]
  conduct = 2
  density = 1
  expand = 3
  formula = Sr
  name = G4_Sr
  specific = 4
FEATURE [App::DocumentObjectGroupPython] Y_element001  label="Y_element : 1"  # scripted group (container) (typed FeaturePython)
  n = 1
  ref = Y_element
FEATURE [App::DocumentObjectGroupPython] G4_Y  # scripted group (container) (typed FeaturePython)
  Dunit = g/cm3
  Dvalue = 4.469
  Group = -> [Y_element001]
  conduct = 2
  density = 1
  expand = 3
  formula = Y
  name = G4_Y
  specific = 4
FEATURE [App::DocumentObjectGroupPython] Zr_element001  label="Zr_element : 1"  # scripted group (container) (typed FeaturePython)
  n = 1
  ref = Zr_element
FEATURE [App::DocumentObjectGroupPython] G4_Zr  # scripted group (container) (typed FeaturePython)
  Dunit = g/cm3
  Dvalue = 6.506
  Group = -> [Zr_element001]
  conduct = 2
  density = 1
  expand = 3
  formula = Zr
  name = G4_Zr
  specific = 4
FEATURE [App::DocumentObjectGroupPython] Nb_element001  label="Nb_element : 1"  # scripted group (container) (typed FeaturePython)
  n = 1
  ref = Nb_element
FEATURE [App::DocumentObjectGroupPython] G4_Nb  # scripted group (container) (typed FeaturePython)
  Dunit = g/cm3
  Dvalue = 8.57
  Group = -> [Nb_element001]
  conduct = 2
  density = 1
  expand = 3
  formula = Nb
  name = G4_Nb
  specific = 4
FEATURE [App::DocumentObjectGroupPython] Mo_element001  label="Mo_element : 1"  # scripted group (container) (typed FeaturePython)
  n = 1
  ref = Mo_element
FEATURE [App::DocumentObjectGroupPython] G4_Mo  # scripted group (container) (typed FeaturePython)
  Dunit = g/cm3
  Dvalue = 10.22
  Group = -> [Mo_element001]
  conduct = 2
  density = 1
  expand = 3
  formula = Mo
  name = G4_Mo
  specific = 4
FEATURE [App::DocumentObjectGroupPython] Tc_element001  label="Tc_element : 1"  # scripted group (container) (typed FeaturePython)
  n = 1
  ref = Tc_element
FEATURE [App::DocumentObjectGroupPython] G4_Tc  # scripted group (container) (typed FeaturePython)
  Dunit = g/cm3
  Dvalue = 11.5
  Group = -> [Tc_element001]
  conduct = 2
  density = 1
  expand = 3
  formula = Tc
  name = G4_Tc
  specific = 4
FEATURE [App::DocumentObjectGroupPython] Ru_element001  label="Ru_element : 1"  # scripted group (container) (typed FeaturePython)
  n = 1
  ref = Ru_element
FEATURE [App::DocumentObjectGroupPython] G4_Ru  # scripted group (container) (typed FeaturePython)
  Dunit = g/cm3
  Dvalue = 12.41
  Group = -> [Ru_element001]
  conduct = 2
  density = 1
  expand = 3
  formula = Ru
  name = G4_Ru
  specific = 4
FEATURE [App::DocumentObjectGroupPython] Rh_element001  label="Rh_element : 1"  # scripted group (container) (typed FeaturePython)
  n = 1
  ref = Rh_element
FEATURE [App::DocumentObjectGroupPython] G4_Rh  # scripted group (container) (typed FeaturePython)
  Dunit = g/cm3
  Dvalue = 12.41
  Group = -> [Rh_element001]
  conduct = 2
  density = 1
  expand = 3
  formula = Rh
  name = G4_Rh
  specific = 4
FEATURE [App::DocumentObjectGroupPython] Pd_element001  label="Pd_element : 1"  # scripted group (container) (typed FeaturePython)
  n = 1
  ref = Pd_element
FEATURE [App::DocumentObjectGroupPython] G4_Pd  # scripted group (container) (typed FeaturePython)
  Dunit = g/cm3
  Dvalue = 12.02
  Group = -> [Pd_element001]
  conduct = 2
  density = 1
  expand = 3
  formula = Pd
  name = G4_Pd
  specific = 4
FEATURE [App::DocumentObjectGroupPython] Ag_element006  label="Ag_element : 004"  # scripted group (container) (typed FeaturePython)
  n = 1
  ref = Ag_element
FEATURE [App::DocumentObjectGroupPython] G4_Ag  # scripted group (container) (typed FeaturePython)
  Dunit = g/cm3
  Dvalue = 10.5
  Group = -> [Ag_element006]
  conduct = 2
  density = 1
  expand = 3
  formula = Ag
  name = G4_Ag
  specific = 4
FEATURE [App::DocumentObjectGroupPython] Cd_element003  label="Cd_element : 003"  # scripted group (container) (typed FeaturePython)
  n = 1
  ref = Cd_element
FEATURE [App::DocumentObjectGroupPython] G4_Cd  # scripted group (container) (typed FeaturePython)
  Dunit = g/cm3
  Dvalue = 8.65
  Group = -> [Cd_element003]
  conduct = 2
  density = 1
  expand = 3
  formula = Cd
  name = G4_Cd
  specific = 4
FEATURE [App::DocumentObjectGroupPython] In_element001  label="In_element : 1"  # scripted group (container) (typed FeaturePython)
  n = 1
  ref = In_element
FEATURE [App::DocumentObjectGroupPython] G4_In  # scripted group (container) (typed FeaturePython)
  Dunit = g/cm3
  Dvalue = 7.31
  Group = -> [In_element001]
  conduct = 2
  density = 1
  expand = 3
  formula = In
  name = G4_In
  specific = 4
FEATURE [App::DocumentObjectGroupPython] Sn_element001  label="Sn_element : 1"  # scripted group (container) (typed FeaturePython)
  n = 1
  ref = Sn_element
FEATURE [App::DocumentObjectGroupPython] G4_Sn  # scripted group (container) (typed FeaturePython)
  Dunit = g/cm3
  Dvalue = 7.31
  Group = -> [Sn_element001]
  conduct = 2
  density = 1
  expand = 3
  formula = Sn
  name = G4_Sn
  specific = 4
FEATURE [App::DocumentObjectGroupPython] Sb_element001  label="Sb_element : 1"  # scripted group (container) (typed FeaturePython)
  n = 1
  ref = Sb_element
FEATURE [App::DocumentObjectGroupPython] G4_Sb  # scripted group (container) (typed FeaturePython)
  Dunit = g/cm3
  Dvalue = 6.691
  Group = -> [Sb_element001]
  conduct = 2
  density = 1
  expand = 3
  formula = Sb
  name = G4_Sb
  specific = 4
FEATURE [App::DocumentObjectGroupPython] Te_element002  label="Te_element : 002"  # scripted group (container) (typed FeaturePython)
  n = 1
  ref = Te_element
FEATURE [App::DocumentObjectGroupPython] G4_Te  # scripted group (container) (typed FeaturePython)
  Dunit = g/cm3
  Dvalue = 6.24
  Group = -> [Te_element002]
  conduct = 2
  density = 1
  expand = 3
  formula = Te
  name = G4_Te
  specific = 4
FEATURE [App::DocumentObjectGroupPython] I_element010  label="I_element : 006"  # scripted group (container) (typed FeaturePython)
  n = 1
  ref = I_element
FEATURE [App::DocumentObjectGroupPython] G4_I  # scripted group (container) (typed FeaturePython)
  Dunit = g/cm3
  Dvalue = 4.93
  Group = -> [I_element010]
  conduct = 2
  density = 1
  expand = 3
  formula = I
  name = G4_I
  specific = 4
FEATURE [App::DocumentObjectGroupPython] Xe_element001  label="Xe_element : 1"  # scripted group (container) (typed FeaturePython)
  n = 1
  ref = Xe_element
FEATURE [App::DocumentObjectGroupPython] G4_Xe  # scripted group (container) (typed FeaturePython)
  Dunit = g/cm3
  Dvalue = 0.00548536
  Group = -> [Xe_element001]
  conduct = 2
  density = 1
  expand = 3
  formula = Xe
  name = G4_Xe
  specific = 4
FEATURE [App::DocumentObjectGroupPython] Cs_element003  label="Cs_element : 003"  # scripted group (container) (typed FeaturePython)
  n = 1
  ref = Cs_element
FEATURE [App::DocumentObjectGroupPython] G4_Cs  # scripted group (container) (typed FeaturePython)
  Dunit = g/cm3
  Dvalue = 1.873
  Group = -> [Cs_element003]
  conduct = 2
  density = 1
  expand = 3
  formula = Cs
  name = G4_Cs
  specific = 4
FEATURE [App::DocumentObjectGroupPython] Ba_element003  label="Ba_element : 003"  # scripted group (container) (typed FeaturePython)
  n = 1
  ref = Ba_element
FEATURE [App::DocumentObjectGroupPython] G4_Ba  # scripted group (container) (typed FeaturePython)
  Dunit = g/cm3
  Dvalue = 3.5
  Group = -> [Ba_element003]
  conduct = 2
  density = 1
  expand = 3
  formula = Ba
  name = G4_Ba
  specific = 4
FEATURE [App::DocumentObjectGroupPython] La_element003  label="La_element : 003"  # scripted group (container) (typed FeaturePython)
  n = 1
  ref = La_element
FEATURE [App::DocumentObjectGroupPython] G4_La  # scripted group (container) (typed FeaturePython)
  Dunit = g/cm3
  Dvalue = 6.154
  Group = -> [La_element003]
  conduct = 2
  density = 1
  expand = 3
  formula = La
  name = G4_La
  specific = 4
FEATURE [App::DocumentObjectGroupPython] Ce_element002  label="Ce_element : 1"  # scripted group (container) (typed FeaturePython)
  n = 1
  ref = Ce_element
FEATURE [App::DocumentObjectGroupPython] G4_Ce  # scripted group (container) (typed FeaturePython)
  Dunit = g/cm3
  Dvalue = 6.657
  Group = -> [Ce_element002]
  conduct = 2
  density = 1
  expand = 3
  formula = Ce
  name = G4_Ce
  specific = 4
FEATURE [App::DocumentObjectGroupPython] Pr_element001  label="Pr_element : 1"  # scripted group (container) (typed FeaturePython)
  n = 1
  ref = Pr_element
FEATURE [App::DocumentObjectGroupPython] G4_Pr  # scripted group (container) (typed FeaturePython)
  Dunit = g/cm3
  Dvalue = 6.71
  Group = -> [Pr_element001]
  conduct = 2
  density = 1
  expand = 3
  formula = Pr
  name = G4_Pr
  specific = 4
FEATURE [App::DocumentObjectGroupPython] Nd_element001  label="Nd_element : 1"  # scripted group (container) (typed FeaturePython)
  n = 1
  ref = Nd_element
FEATURE [App::DocumentObjectGroupPython] G4_Nd  # scripted group (container) (typed FeaturePython)
  Dunit = g/cm3
  Dvalue = 6.9
  Group = -> [Nd_element001]
  conduct = 2
  density = 1
  expand = 3
  formula = Nd
  name = G4_Nd
  specific = 4
FEATURE [App::DocumentObjectGroupPython] Pm_element001  label="Pm_element : 1"  # scripted group (container) (typed FeaturePython)
  n = 1
  ref = Pm_element
FEATURE [App::DocumentObjectGroupPython] G4_Pm  # scripted group (container) (typed FeaturePython)
  Dunit = g/cm3
  Dvalue = 7.22
  Group = -> [Pm_element001]
  conduct = 2
  density = 1
  expand = 3
  formula = Pm
  name = G4_Pm
  specific = 4
FEATURE [App::DocumentObjectGroupPython] Sm_element001  label="Sm_element : 1"  # scripted group (container) (typed FeaturePython)
  n = 1
  ref = Sm_element
FEATURE [App::DocumentObjectGroupPython] G4_Sm  # scripted group (container) (typed FeaturePython)
  Dunit = g/cm3
  Dvalue = 7.46
  Group = -> [Sm_element001]
  conduct = 2
  density = 1
  expand = 3
  formula = Sm
  name = G4_Sm
  specific = 4
FEATURE [App::DocumentObjectGroupPython] Eu_element001  label="Eu_element : 1"  # scripted group (container) (typed FeaturePython)
  n = 1
  ref = Eu_element
FEATURE [App::DocumentObjectGroupPython] G4_Eu  # scripted group (container) (typed FeaturePython)
  Dunit = g/cm3
  Dvalue = 5.243
  Group = -> [Eu_element001]
  conduct = 2
  density = 1
  expand = 3
  formula = Eu
  name = G4_Eu
  specific = 4
FEATURE [App::DocumentObjectGroupPython] Gd_element002  label="Gd_element : 1"  # scripted group (container) (typed FeaturePython)
  n = 1
  ref = Gd_element
FEATURE [App::DocumentObjectGroupPython] G4_Gd  # scripted group (container) (typed FeaturePython)
  Dunit = g/cm3
  Dvalue = 7.9004
  Group = -> [Gd_element002]
  conduct = 2
  density = 1
  expand = 3
  formula = Gd
  name = G4_Gd
  specific = 4
FEATURE [App::DocumentObjectGroupPython] Tb_element001  label="Tb_element : 1"  # scripted group (container) (typed FeaturePython)
  n = 1
  ref = Tb_element
FEATURE [App::DocumentObjectGroupPython] G4_Tb  # scripted group (container) (typed FeaturePython)
  Dunit = g/cm3
  Dvalue = 8.229
  Group = -> [Tb_element001]
  conduct = 2
  density = 1
  expand = 3
  formula = Tb
  name = G4_Tb
  specific = 4
FEATURE [App::DocumentObjectGroupPython] Dy_element001  label="Dy_element : 1"  # scripted group (container) (typed FeaturePython)
  n = 1
  ref = Dy_element
FEATURE [App::DocumentObjectGroupPython] G4_Dy  # scripted group (container) (typed FeaturePython)
  Dunit = g/cm3
  Dvalue = 8.55
  Group = -> [Dy_element001]
  conduct = 2
  density = 1
  expand = 3
  formula = Dy
  name = G4_Dy
  specific = 4
FEATURE [App::DocumentObjectGroupPython] Ho_element001  label="Ho_element : 1"  # scripted group (container) (typed FeaturePython)
  n = 1
  ref = Ho_element
FEATURE [App::DocumentObjectGroupPython] G4_Ho  # scripted group (container) (typed FeaturePython)
  Dunit = g/cm3
  Dvalue = 8.795
  Group = -> [Ho_element001]
  conduct = 2
  density = 1
  expand = 3
  formula = Ho
  name = G4_Ho
  specific = 4
FEATURE [App::DocumentObjectGroupPython] Er_element001  label="Er_element : 1"  # scripted group (container) (typed FeaturePython)
  n = 1
  ref = Er_element
FEATURE [App::DocumentObjectGroupPython] G4_Er  # scripted group (container) (typed FeaturePython)
  Dunit = g/cm3
  Dvalue = 9.066
  Group = -> [Er_element001]
  conduct = 2
  density = 1
  expand = 3
  formula = Er
  name = G4_Er
  specific = 4
FEATURE [App::DocumentObjectGroupPython] Tm_element001  label="Tm_element : 1"  # scripted group (container) (typed FeaturePython)
  n = 1
  ref = Tm_element
FEATURE [App::DocumentObjectGroupPython] G4_Tm  # scripted group (container) (typed FeaturePython)
  Dunit = g/cm3
  Dvalue = 9.321
  Group = -> [Tm_element001]
  conduct = 2
  density = 1
  expand = 3
  formula = Tm
  name = G4_Tm
  specific = 4
FEATURE [App::DocumentObjectGroupPython] Yb_element001  label="Yb_element : 1"  # scripted group (container) (typed FeaturePython)
  n = 1
  ref = Yb_element
FEATURE [App::DocumentObjectGroupPython] G4_Yb  # scripted group (container) (typed FeaturePython)
  Dunit = g/cm3
  Dvalue = 6.73
  Group = -> [Yb_element001]
  conduct = 2
  density = 1
  expand = 3
  formula = Yb
  name = G4_Yb
  specific = 4
FEATURE [App::DocumentObjectGroupPython] Lu_element001  label="Lu_element : 1"  # scripted group (container) (typed FeaturePython)
  n = 1
  ref = Lu_element
FEATURE [App::DocumentObjectGroupPython] G4_Lu  # scripted group (container) (typed FeaturePython)
  Dunit = g/cm3
  Dvalue = 9.84
  Group = -> [Lu_element001]
  conduct = 2
  density = 1
  expand = 3
  formula = Lu
  name = G4_Lu
  specific = 4
FEATURE [App::DocumentObjectGroupPython] Hf_element001  label="Hf_element : 1"  # scripted group (container) (typed FeaturePython)
  n = 1
  ref = Hf_element
FEATURE [App::DocumentObjectGroupPython] G4_Hf  # scripted group (container) (typed FeaturePython)
  Dunit = g/cm3
  Dvalue = 13.31
  Group = -> [Hf_element001]
  conduct = 2
  density = 1
  expand = 3
  formula = Hf
  name = G4_Hf
  specific = 4
FEATURE [App::DocumentObjectGroupPython] Ta_element001  label="Ta_element : 1"  # scripted group (container) (typed FeaturePython)
  n = 1
  ref = Ta_element
FEATURE [App::DocumentObjectGroupPython] G4_Ta  # scripted group (container) (typed FeaturePython)
  Dunit = g/cm3
  Dvalue = 16.654
  Group = -> [Ta_element001]
  conduct = 2
  density = 1
  expand = 3
  formula = Ta
  name = G4_Ta
  specific = 4
FEATURE [App::DocumentObjectGroupPython] W_element004  label="W_element : 004"  # scripted group (container) (typed FeaturePython)
  n = 1
  ref = W_element
FEATURE [App::DocumentObjectGroupPython] G4_W  # scripted group (container) (typed FeaturePython)
  Dunit = g/cm3
  Dvalue = 19.3
  Group = -> [W_element004]
  conduct = 2
  density = 1
  expand = 3
  formula = W
  name = G4_W
  specific = 4
FEATURE [App::DocumentObjectGroupPython] Re_element001  label="Re_element : 1"  # scripted group (container) (typed FeaturePython)
  n = 1
  ref = Re_element
FEATURE [App::DocumentObjectGroupPython] G4_Re  # scripted group (container) (typed FeaturePython)
  Dunit = g/cm3
  Dvalue = 21.02
  Group = -> [Re_element001]
  conduct = 2
  density = 1
  expand = 3
  formula = Re
  name = G4_Re
  specific = 4
FEATURE [App::DocumentObjectGroupPython] Os_element001  label="Os_element : 1"  # scripted group (container) (typed FeaturePython)
  n = 1
  ref = Os_element
FEATURE [App::DocumentObjectGroupPython] G4_Os  # scripted group (container) (typed FeaturePython)
  Dunit = g/cm3
  Dvalue = 22.57
  Group = -> [Os_element001]
  conduct = 2
  density = 1
  expand = 3
  formula = Os
  name = G4_Os
  specific = 4
FEATURE [App::DocumentObjectGroupPython] Ir_element001  label="Ir_element : 1"  # scripted group (container) (typed FeaturePython)
  n = 1
  ref = Ir_element
FEATURE [App::DocumentObjectGroupPython] G4_Ir  # scripted group (container) (typed FeaturePython)
  Dunit = g/cm3
  Dvalue = 22.42
  Group = -> [Ir_element001]
  conduct = 2
  density = 1
  expand = 3
  formula = Ir
  name = G4_Ir
  specific = 4
FEATURE [App::DocumentObjectGroupPython] Pt_element001  label="Pt_element : 1"  # scripted group (container) (typed FeaturePython)
  n = 1
  ref = Pt_element
FEATURE [App::DocumentObjectGroupPython] G4_Pt  # scripted group (container) (typed FeaturePython)
  Dunit = g/cm3
  Dvalue = 21.45
  Group = -> [Pt_element001]
  conduct = 2
  density = 1
  expand = 3
  formula = Pt
  name = G4_Pt
  specific = 4
FEATURE [App::DocumentObjectGroupPython] Au_element001  label="Au_element : 1"  # scripted group (container) (typed FeaturePython)
  n = 1
  ref = Au_element
FEATURE [App::DocumentObjectGroupPython] G4_Au  # scripted group (container) (typed FeaturePython)
  Dunit = g/cm3
  Dvalue = 19.32
  Group = -> [Au_element001]
  conduct = 2
  density = 1
  expand = 3
  formula = Au
  name = G4_Au
  specific = 4
FEATURE [App::DocumentObjectGroupPython] Hg_element002  label="Hg_element : 002"  # scripted group (container) (typed FeaturePython)
  n = 1
  ref = Hg_element
FEATURE [App::DocumentObjectGroupPython] G4_Hg  # scripted group (container) (typed FeaturePython)
  Dunit = g/cm3
  Dvalue = 13.546
  Group = -> [Hg_element002]
  conduct = 2
  density = 1
  expand = 3
  formula = Hg
  name = G4_Hg
  specific = 4
FEATURE [App::DocumentObjectGroupPython] Tl_element002  label="Tl_element : 002"  # scripted group (container) (typed FeaturePython)
  n = 1
  ref = Tl_element
FEATURE [App::DocumentObjectGroupPython] G4_Tl  # scripted group (container) (typed FeaturePython)
  Dunit = g/cm3
  Dvalue = 11.72
  Group = -> [Tl_element002]
  conduct = 2
  density = 1
  expand = 3
  formula = Tl
  name = G4_Tl
  specific = 4
FEATURE [App::DocumentObjectGroupPython] Pb_element003  label="Pb_element : 1"  # scripted group (container) (typed FeaturePython)
  n = 1
  ref = Pb_element
FEATURE [App::DocumentObjectGroupPython] G4_Pb  # scripted group (container) (typed FeaturePython)
  Dunit = g/cm3
  Dvalue = 11.35
  Group = -> [Pb_element003]
  conduct = 2
  density = 1
  expand = 3
  formula = Pb
  name = G4_Pb
  specific = 4
FEATURE [App::DocumentObjectGroupPython] Bi_element002  label="Bi_element : 1"  # scripted group (container) (typed FeaturePython)
  n = 1
  ref = Bi_element
FEATURE [App::DocumentObjectGroupPython] G4_Bi  # scripted group (container) (typed FeaturePython)
  Dunit = g/cm3
  Dvalue = 9.747
  Group = -> [Bi_element002]
  conduct = 2
  density = 1
  expand = 3
  formula = Bi
  name = G4_Bi
  specific = 4
FEATURE [App::DocumentObjectGroupPython] Po_element001  label="Po_element : 1"  # scripted group (container) (typed FeaturePython)
  n = 1
  ref = Po_element
FEATURE [App::DocumentObjectGroupPython] G4_Po  # scripted group (container) (typed FeaturePython)
  Dunit = g/cm3
  Dvalue = 9.32
  Group = -> [Po_element001]
  conduct = 2
  density = 1
  expand = 3
  formula = Po
  name = G4_Po
  specific = 4
FEATURE [App::DocumentObjectGroupPython] At_element001  label="At_element : 1"  # scripted group (container) (typed FeaturePython)
  n = 1
  ref = At_element
FEATURE [App::DocumentObjectGroupPython] G4_At  # scripted group (container) (typed FeaturePython)
  Dunit = g/cm3
  Dvalue = 9.32
  Group = -> [At_element001]
  conduct = 2
  density = 1
  expand = 3
  formula = At
  name = G4_At
  specific = 4
FEATURE [App::DocumentObjectGroupPython] Rn_element001  label="Rn_element : 1"  # scripted group (container) (typed FeaturePython)
  n = 1
  ref = Rn_element
FEATURE [App::DocumentObjectGroupPython] G4_Rn  # scripted group (container) (typed FeaturePython)
  Dunit = g/cm3
  Dvalue = 0.00900662
  Group = -> [Rn_element001]
  conduct = 2
  density = 1
  expand = 3
  formula = Rn
  name = G4_Rn
  specific = 4
FEATURE [App::DocumentObjectGroupPython] Fr_element001  label="Fr_element : 1"  # scripted group (container) (typed FeaturePython)
  n = 1
  ref = Fr_element
FEATURE [App::DocumentObjectGroupPython] G4_Fr  # scripted group (container) (typed FeaturePython)
  Dunit = g/cm3
  Dvalue = 1
  Group = -> [Fr_element001]
  conduct = 2
  density = 1
  expand = 3
  formula = Fr
  name = G4_Fr
  specific = 4
FEATURE [App::DocumentObjectGroupPython] Ra_element001  label="Ra_element : 1"  # scripted group (container) (typed FeaturePython)
  n = 1
  ref = Ra_element
FEATURE [App::DocumentObjectGroupPython] G4_Ra  # scripted group (container) (typed FeaturePython)
  Dunit = g/cm3
  Dvalue = 5
  Group = -> [Ra_element001]
  conduct = 2
  density = 1
  expand = 3
  formula = Ra
  name = G4_Ra
  specific = 4
FEATURE [App::DocumentObjectGroupPython] Ac_element001  label="Ac_element : 1"  # scripted group (container) (typed FeaturePython)
  n = 1
  ref = Ac_element
FEATURE [App::DocumentObjectGroupPython] G4_Ac  # scripted group (container) (typed FeaturePython)
  Dunit = g/cm3
  Dvalue = 10.07
  Group = -> [Ac_element001]
  conduct = 2
  density = 1
  expand = 3
  formula = Ac
  name = G4_Ac
  specific = 4
FEATURE [App::DocumentObjectGroupPython] Th_element001  label="Th_element : 1"  # scripted group (container) (typed FeaturePython)
  n = 1
  ref = Th_element
FEATURE [App::DocumentObjectGroupPython] G4_Th  # scripted group (container) (typed FeaturePython)
  Dunit = g/cm3
  Dvalue = 11.72
  Group = -> [Th_element001]
  conduct = 2
  density = 1
  expand = 3
  formula = Th
  name = G4_Th
  specific = 4
FEATURE [App::DocumentObjectGroupPython] Pa_element001  label="Pa_element : 1"  # scripted group (container) (typed FeaturePython)
  n = 1
  ref = Pa_element
FEATURE [App::DocumentObjectGroupPython] G4_Pa  # scripted group (container) (typed FeaturePython)
  Dunit = g/cm3
  Dvalue = 15.37
  Group = -> [Pa_element001]
  conduct = 2
  density = 1
  expand = 3
  formula = Pa
  name = G4_Pa
  specific = 4
FEATURE [App::DocumentObjectGroupPython] U_element004  label="U_element : 004"  # scripted group (container) (typed FeaturePython)
  n = 1
  ref = U_element
FEATURE [App::DocumentObjectGroupPython] G4_U  # scripted group (container) (typed FeaturePython)
  Dunit = g/cm3
  Dvalue = 18.95
  Group = -> [U_element004]
  conduct = 2
  density = 1
  expand = 3
  formula = U
  name = G4_U
  specific = 4
FEATURE [App::DocumentObjectGroupPython] Np_element001  label="Np_element : 1"  # scripted group (container) (typed FeaturePython)
  n = 1
  ref = Np_element
FEATURE [App::DocumentObjectGroupPython] G4_Np  # scripted group (container) (typed FeaturePython)
  Dunit = g/cm3
  Dvalue = 20.25
  Group = -> [Np_element001]
  conduct = 2
  density = 1
  expand = 3
  formula = Np
  name = G4_Np
  specific = 4
FEATURE [App::DocumentObjectGroupPython] Pu_element002  label="Pu_element : 002"  # scripted group (container) (typed FeaturePython)
  n = 1
  ref = Pu_element
FEATURE [App::DocumentObjectGroupPython] G4_Pu  # scripted group (container) (typed FeaturePython)
  Dunit = g/cm3
  Dvalue = 19.84
  Group = -> [Pu_element002]
  conduct = 2
  density = 1
  expand = 3
  formula = Pu
  name = G4_Pu
  specific = 4
FEATURE [App::DocumentObjectGroupPython] Am_element001  label="Am_element : 1"  # scripted group (container) (typed FeaturePython)
  n = 1
  ref = Am_element
FEATURE [App::DocumentObjectGroupPython] G4_Am  # scripted group (container) (typed FeaturePython)
  Dunit = g/cm3
  Dvalue = 13.67
  Group = -> [Am_element001]
  conduct = 2
  density = 1
  expand = 3
  formula = Am
  name = G4_Am
  specific = 4
FEATURE [App::DocumentObjectGroupPython] Cm_element001  label="Cm_element : 1"  # scripted group (container) (typed FeaturePython)
  n = 1
  ref = Cm_element
FEATURE [App::DocumentObjectGroupPython] G4_Cm  # scripted group (container) (typed FeaturePython)
  Dunit = g/cm3
  Dvalue = 13.51
  Group = -> [Cm_element001]
  conduct = 2
  density = 1
  expand = 3
  formula = Cm
  name = G4_Cm
  specific = 4
FEATURE [App::DocumentObjectGroupPython] Bk_element001  label="Bk_element : 1"  # scripted group (container) (typed FeaturePython)
  n = 1
  ref = Bk_element
FEATURE [App::DocumentObjectGroupPython] G4_Bk  # scripted group (container) (typed FeaturePython)
  Dunit = g/cm3
  Dvalue = 14
  Group = -> [Bk_element001]
  conduct = 2
  density = 1
  expand = 3
  formula = Bk
  name = G4_Bk
  specific = 4
FEATURE [App::DocumentObjectGroupPython] Cf_element001  label="Cf_element : 1"  # scripted group (container) (typed FeaturePython)
  n = 1
  ref = Cf_element
FEATURE [App::DocumentObjectGroupPython] G4_Cf  # scripted group (container) (typed FeaturePython)
  Dunit = g/cm3
  Dvalue = 10
  Group = -> [Cf_element001]
  conduct = 2
  density = 1
  expand = 3
  formula = Cf
  name = G4_Cf
  specific = 4
FEATURE [App::DocumentObjectGroupPython] Element  # scripted group (container) (typed FeaturePython)
  Group = -> [G4_H,G4_He,G4_Li,G4_Be,G4_B,G4_C,G4_N,G4_O,G4_F,G4_Ne,G4_Na,G4_Mg,G4_Al,G4_Si,G4_P,G4_S,G4_Cl,G4_Ar,G4_K,G4_Ca,G4_Sc,G4_Ti,G4_V,G4_Cr,G4_Mn,G4_Fe,G4_Co,G4_Ni,G4_Cu,G4_Zn,G4_Ga,G4_Ge,G4_As,G4_Se,G4_Br,G4_Kr,G4_Rb,G4_Sr,G4_Y,G4_Zr,G4_Nb,G4_Mo,G4_Tc,G4_Ru,G4_Rh,G4_Pd,G4_Ag,G4_Cd,G4_In,G4_Sn,G4_Sb,G4_Te,G4_I,G4_Xe,G4_Cs,G4_Ba,G4_La,G4_Ce,G4_Pr,G4_Nd,G4_Pm,G4_Sm,G4_Eu,G4_Gd,G4_Tb,G4_Dy,G4_Ho,G4_Er,+30 more]
FEATURE [App::DocumentObjectGroupPython] H_element114  label="H_element : 063"  # scripted group (container) (typed FeaturePython)
  n = 2
  ref = H_element
FEATURE [App::DocumentObjectGroupPython] G4_lH2  # scripted group (container) (typed FeaturePython)
  Dunit = g/cm3
  Dvalue = 0.0708
  Group = -> [H_element114]
  conduct = 2
  density = 1
  expand = 3
  formula = G4_lH2
  name = G4_lH2
  specific = 4
FEATURE [App::DocumentObjectGroupPython] N_element049  label="N_element : 022"  # scripted group (container) (typed FeaturePython)
  n = 2
  ref = N_element
FEATURE [App::DocumentObjectGroupPython] G4_lN2  # scripted group (container) (typed FeaturePython)
  Dunit = g/cm3
  Dvalue = 0.807
  Group = -> [N_element049]
  conduct = 2
  density = 1
  expand = 3
  formula = G4_lN2
  name = G4_lN2
  specific = 4
FEATURE [App::DocumentObjectGroupPython] O_element106  label="O_element : 060"  # scripted group (container) (typed FeaturePython)
  n = 2
  ref = O_element
FEATURE [App::DocumentObjectGroupPython] G4_lO2  # scripted group (container) (typed FeaturePython)
  Dunit = g/cm3
  Dvalue = 1.141
  Group = -> [O_element106]
  conduct = 2
  density = 1
  expand = 3
  formula = G4_lO2
  name = G4_lO2
  specific = 4
FEATURE [App::DocumentObjectGroupPython] Ar_element003  label="Ar_element : 002"  # scripted group (container) (typed FeaturePython)
  n = 1
  ref = Ar_element
FEATURE [App::DocumentObjectGroupPython] G4_lAr  # scripted group (container) (typed FeaturePython)
  Dunit = g/cm3
  Dvalue = 1.396
  Group = -> [Ar_element003]
  conduct = 2
  density = 1
  expand = 3
  formula = G4_lAr
  name = G4_lAr
  specific = 4
FEATURE [App::DocumentObjectGroupPython] Br_element008  label="Br_element : 005"  # scripted group (container) (typed FeaturePython)
  n = 1
  ref = Br_element
FEATURE [App::DocumentObjectGroupPython] G4_lBr  # scripted group (container) (typed FeaturePython)
  Dunit = g/cm3
  Dvalue = 3.1028
  Group = -> [Br_element008]
  conduct = 2
  density = 1
  expand = 3
  formula = G4_lBr
  name = G4_lBr
  specific = 4
FEATURE [App::DocumentObjectGroupPython] Kr_element002  label="Kr_element : 002"  # scripted group (container) (typed FeaturePython)
  n = 1
  ref = Kr_element
FEATURE [App::DocumentObjectGroupPython] G4_lKr  # scripted group (container) (typed FeaturePython)
  Dunit = g/cm3
  Dvalue = 2.418
  Group = -> [Kr_element002]
  conduct = 2
  density = 1
  expand = 3
  formula = G4_lKr
  name = G4_lKr
  specific = 4
FEATURE [App::DocumentObjectGroupPython] Xe_element002  label="Xe_element : 002"  # scripted group (container) (typed FeaturePython)
  n = 1
  ref = Xe_element
FEATURE [App::DocumentObjectGroupPython] G4_lXe  # scripted group (container) (typed FeaturePython)
  Dunit = g/cm3
  Dvalue = 2.953
  Group = -> [Xe_element002]
  conduct = 2
  density = 1
  expand = 3
  formula = G4_lXe
  name = G4_lXe
  specific = 4
FEATURE [App::DocumentObjectGroupPython] O_element107  label="O_element : 061"  # scripted group (container) (typed FeaturePython)
  n = 4
  ref = O_element
FEATURE [App::DocumentObjectGroupPython] Pb_element004  label="Pb_element : 002"  # scripted group (container) (typed FeaturePython)
  n = 1
  ref = Pb_element
FEATURE [App::DocumentObjectGroupPython] W_element005  label="W_element : 005"  # scripted group (container) (typed FeaturePython)
  n = 1
  ref = W_element
FEATURE [App::DocumentObjectGroupPython] G4_PbWO4  # scripted group (container) (typed FeaturePython)
  Dunit = g/cm3
  Dvalue = 8.28
  Group = -> [O_element107,Pb_element004,W_element005]
  conduct = 2
  density = 1
  expand = 3
  formula = G4_PbWO4
  name = G4_PbWO4
  specific = 4
FEATURE [App::DocumentObjectGroupPython] H_element115  label="H_element : 064"  # scripted group (container) (typed FeaturePython)
  n = 1
  ref = H_element
FEATURE [App::DocumentObjectGroupPython] G4_Galactic  # scripted group (container) (typed FeaturePython)
  Dunit = g/cm3
  Dvalue = 0
  Group = -> [H_element115]
  conduct = 2
  density = 1
  expand = 3
  formula = G4_Galactic
  name = G4_Galactic
  specific = 4
FEATURE [App::DocumentObjectGroupPython] C_element125  label="C_element : 071"  # scripted group (container) (typed FeaturePython)
  n = 1
  ref = C_element
FEATURE [App::DocumentObjectGroupPython] G4_GRAPHITE_POROUS  # scripted group (container) (typed FeaturePython)
  Dunit = g/cm3
  Dvalue = 1.7
  Group = -> [C_element125]
  conduct = 2
  density = 1
  expand = 3
  formula = G4_GRAPHITE_POROUS
  name = G4_GRAPHITE_POROUS
  specific = 4
FEATURE [App::DocumentObjectGroupPython] H_element116  label="H_element : 0.150"  # scripted group (container) (typed FeaturePython)
  n = 0.080538
FEATURE [App::DocumentObjectGroupPython] C_element126  label="C_element : 0.600"  # scripted group (container) (typed FeaturePython)
  n = 0.599848
FEATURE [App::DocumentObjectGroupPython] O_element108  label="O_element : 0.320"  # scripted group (container) (typed FeaturePython)
  n = 0.319614
FEATURE [App::DocumentObjectGroupPython] G4_LUCITE  # scripted group (container) (typed FeaturePython)
  Dunit = g/cm3
  Dvalue = 1.19
  Group = -> [H_element116,C_element126,O_element108]
  conduct = 2
  density = 1
  expand = 3
  formula = G4_LUCITE
  name = G4_LUCITE
  specific = 4
FEATURE [App::DocumentObjectGroupPython] Cu_element002  label="Cu_element : 62"  # scripted group (container) (typed FeaturePython)
  n = 62
  ref = Cu_element
FEATURE [App::DocumentObjectGroupPython] Zn_element002  label="Zn_element : 35"  # scripted group (container) (typed FeaturePython)
  n = 35
  ref = Zn_element
FEATURE [App::DocumentObjectGroupPython] Pb_element005  label="Pb_element : 3"  # scripted group (container) (typed FeaturePython)
  n = 3
  ref = Pb_element
FEATURE [App::DocumentObjectGroupPython] G4_BRASS  # scripted group (container) (typed FeaturePython)
  Dunit = g/cm3
  Dvalue = 8.52
  Group = -> [Cu_element002,Zn_element002,Pb_element005]
  conduct = 2
  density = 1
  expand = 3
  formula = G4_BRASS
  name = G4_BRASS
  specific = 4
FEATURE [App::DocumentObjectGroupPython] Cu_element003  label="Cu_element : 89"  # scripted group (container) (typed FeaturePython)
  n = 89
  ref = Cu_element
FEATURE [App::DocumentObjectGroupPython] Zn_element003  label="Zn_element : 9"  # scripted group (container) (typed FeaturePython)
  n = 9
  ref = Zn_element
FEATURE [App::DocumentObjectGroupPython] Pb_element006  label="Pb_element : 2"  # scripted group (container) (typed FeaturePython)
  n = 2
  ref = Pb_element
FEATURE [App::DocumentObjectGroupPython] G4_BRONZE  # scripted group (container) (typed FeaturePython)
  Dunit = g/cm3
  Dvalue = 8.82
  Group = -> [Cu_element003,Zn_element003,Pb_element006]
  conduct = 2
  density = 1
  expand = 3
  formula = G4_BRONZE
  name = G4_BRONZE
  specific = 4
FEATURE [App::DocumentObjectGroupPython] Fe_element008  label="Fe_element : 74"  # scripted group (container) (typed FeaturePython)
  n = 74
  ref = Fe_element
FEATURE [App::DocumentObjectGroupPython] Cr_element002  label="Cr_element : 18"  # scripted group (container) (typed FeaturePython)
  n = 18
  ref = Cr_element
FEATURE [App::DocumentObjectGroupPython] Ni_element002  label="Ni_element : 8"  # scripted group (container) (typed FeaturePython)
  n = 8
  ref = Ni_element
FEATURE [App::DocumentObjectGroupPython] G4_STAINLESS_STEEL  label="G4_STAINLESS-STEEL"  # scripted group (container) (typed FeaturePython)
  Dunit = g/cm3
  Dvalue = 8
  Group = -> [Fe_element008,Cr_element002,Ni_element002]
  conduct = 2
  density = 1
  expand = 3
  formula = G4_STAINLESS-STEEL
  name = G4_STAINLESS-STEEL
  specific = 4
FEATURE [App::DocumentObjectGroupPython] H_element117  label="H_element : 065"  # scripted group (container) (typed FeaturePython)
  n = 18
  ref = H_element
FEATURE [App::DocumentObjectGroupPython] C_element127  label="C_element : 072"  # scripted group (container) (typed FeaturePython)
  n = 12
  ref = C_element
FEATURE [App::DocumentObjectGroupPython] O_element109  label="O_element : 062"  # scripted group (container) (typed FeaturePython)
  n = 7
  ref = O_element
FEATURE [App::DocumentObjectGroupPython] G4_CR39  # scripted group (container) (typed FeaturePython)
  Dunit = g/cm3
  Dvalue = 1.32
  Group = -> [H_element117,C_element127,O_element109]
  conduct = 2
  density = 1
  expand = 3
  formula = G4_CR39
  name = G4_CR39
  specific = 4
FEATURE [App::DocumentObjectGroupPython] H_element118  label="H_element : 38"  # scripted group (container) (typed FeaturePython)
  n = 38
  ref = H_element
FEATURE [App::DocumentObjectGroupPython] C_element128  label="C_element : 073"  # scripted group (container) (typed FeaturePython)
  n = 18
  ref = C_element
FEATURE [App::DocumentObjectGroupPython] O_element110  label="O_element : 063"  # scripted group (container) (typed FeaturePython)
  n = 1
  ref = O_element
FEATURE [App::DocumentObjectGroupPython] G4_OCTADECANOL  # scripted group (container) (typed FeaturePython)
  Dunit = g/cm3
  Dvalue = 0.812
  Group = -> [H_element118,C_element128,O_element110]
  conduct = 2
  density = 1
  expand = 3
  formula = G4_OCTADECANOL
  name = G4_OCTADECANOL
  specific = 4
FEATURE [App::DocumentObjectGroupPython] HEP  # scripted group (container) (typed FeaturePython)
  Group = -> [G4_lH2,G4_lN2,G4_lO2,G4_lAr,G4_lBr,G4_lKr,G4_lXe,G4_PbWO4,G4_Galactic,G4_GRAPHITE_POROUS,G4_LUCITE,G4_BRASS,G4_BRONZE,G4_STAINLESS_STEEL,G4_CR39,G4_OCTADECANOL]
FEATURE [App::DocumentObjectGroupPython] C_element129  label="C_element : 074"  # scripted group (container) (typed FeaturePython)
  n = 14
  ref = C_element
FEATURE [App::DocumentObjectGroupPython] H_element119  label="H_element : 066"  # scripted group (container) (typed FeaturePython)
  n = 10
  ref = H_element
FEATURE [App::DocumentObjectGroupPython] O_element111  label="O_element : 064"  # scripted group (container) (typed FeaturePython)
  n = 2
  ref = O_element
FEATURE [App::DocumentObjectGroupPython] N_element050  label="N_element : 023"  # scripted group (container) (typed FeaturePython)
  n = 2
  ref = N_element
FEATURE [App::DocumentObjectGroupPython] G4_KEVLAR  # scripted group (container) (typed FeaturePython)
  Dunit = g/cm3
  Dvalue = 1.44
  Group = -> [C_element129,H_element119,O_element111,N_element050]
  conduct = 2
  density = 1
  expand = 3
  formula = G4_KEVLAR
  name = G4_KEVLAR
  specific = 4
FEATURE [App::DocumentObjectGroupPython] C_element130  label="C_element : 075"  # scripted group (container) (typed FeaturePython)
  n = 10
  ref = C_element
FEATURE [App::DocumentObjectGroupPython] H_element120  label="H_element : 067"  # scripted group (container) (typed FeaturePython)
  n = 8
  ref = H_element
FEATURE [App::DocumentObjectGroupPython] O_element112  label="O_element : 065"  # scripted group (container) (typed FeaturePython)
  n = 4
  ref = O_element
FEATURE [App::DocumentObjectGroupPython] G4_DACRON  # scripted group (container) (typed FeaturePython)
  Dunit = g/cm3
  Dvalue = 1.4
  Group = -> [C_element130,H_element120,O_element112]
  conduct = 2
  density = 1
  expand = 3
  formula = G4_DACRON
  name = G4_DACRON
  specific = 4
FEATURE [App::DocumentObjectGroupPython] C_element131  label="C_element : 076"  # scripted group (container) (typed FeaturePython)
  n = 4
  ref = C_element
FEATURE [App::DocumentObjectGroupPython] H_element121  label="H_element : 068"  # scripted group (container) (typed FeaturePython)
  n = 5
  ref = H_element
FEATURE [App::DocumentObjectGroupPython] Cl_element030  label="Cl_element : 016"  # scripted group (container) (typed FeaturePython)
  n = 1
  ref = Cl_element
FEATURE [App::DocumentObjectGroupPython] G4_NEOPRENE  # scripted group (container) (typed FeaturePython)
  Dunit = g/cm3
  Dvalue = 1.23
  Group = -> [C_element131,H_element121,Cl_element030]
  conduct = 2
  density = 1
  expand = 3
  formula = G4_NEOPRENE
  name = G4_NEOPRENE
  specific = 4
FEATURE [App::DocumentObjectGroupPython] Space  # scripted group (container) (typed FeaturePython)
  Group = -> [G4_KEVLAR,G4_DACRON,G4_NEOPRENE]
FEATURE [App::DocumentObjectGroupPython] H_element122  label="H_element : 069"  # scripted group (container) (typed FeaturePython)
  n = 5
  ref = H_element
FEATURE [App::DocumentObjectGroupPython] C_element132  label="C_element : 077"  # scripted group (container) (typed FeaturePython)
  n = 4
  ref = C_element
FEATURE [App::DocumentObjectGroupPython] N_element051  label="N_element : 3"  # scripted group (container) (typed FeaturePython)
  n = 3
  ref = N_element
FEATURE [App::DocumentObjectGroupPython] O_element113  label="O_element : 066"  # scripted group (container) (typed FeaturePython)
  n = 1
  ref = O_element
FEATURE [App::DocumentObjectGroupPython] G4_CYTOSINE  # scripted group (container) (typed FeaturePython)
  Dunit = g/cm3
  Dvalue = 1.55
  Group = -> [H_element122,C_element132,N_element051,O_element113]
  conduct = 2
  density = 1
  expand = 3
  formula = G4_CYTOSINE
  name = G4_CYTOSINE
  specific = 4
FEATURE [App::DocumentObjectGroupPython] H_element123  label="H_element : 070"  # scripted group (container) (typed FeaturePython)
  n = 6
  ref = H_element
FEATURE [App::DocumentObjectGroupPython] C_element133  label="C_element : 078"  # scripted group (container) (typed FeaturePython)
  n = 5
  ref = C_element
FEATURE [App::DocumentObjectGroupPython] N_element052  label="N_element : 024"  # scripted group (container) (typed FeaturePython)
  n = 2
  ref = N_element
FEATURE [App::DocumentObjectGroupPython] O_element114  label="O_element : 067"  # scripted group (container) (typed FeaturePython)
  n = 2
  ref = O_element
FEATURE [App::DocumentObjectGroupPython] G4_THYMINE  # scripted group (container) (typed FeaturePython)
  Dunit = g/cm3
  Dvalue = 1.23
  Group = -> [H_element123,C_element133,N_element052,O_element114]
  conduct = 2
  density = 1
  expand = 3
  formula = G4_THYMINE
  name = G4_THYMINE
  specific = 4
FEATURE [App::DocumentObjectGroupPython] H_element124  label="H_element : 071"  # scripted group (container) (typed FeaturePython)
  n = 4
  ref = H_element
FEATURE [App::DocumentObjectGroupPython] C_element134  label="C_element : 079"  # scripted group (container) (typed FeaturePython)
  n = 4
  ref = C_element
FEATURE [App::DocumentObjectGroupPython] N_element053  label="N_element : 025"  # scripted group (container) (typed FeaturePython)
  n = 2
  ref = N_element
FEATURE [App::DocumentObjectGroupPython] O_element115  label="O_element : 068"  # scripted group (container) (typed FeaturePython)
  n = 2
  ref = O_element
FEATURE [App::DocumentObjectGroupPython] G4_URACIL  # scripted group (container) (typed FeaturePython)
  Dunit = g/cm3
  Dvalue = 1.32
  Group = -> [H_element124,C_element134,N_element053,O_element115]
  conduct = 2
  density = 1
  expand = 3
  formula = G4_URACIL
  name = G4_URACIL
  specific = 4
FEATURE [App::DocumentObjectGroupPython] H_element125  label="H_element : 072"  # scripted group (container) (typed FeaturePython)
  n = 4
  ref = H_element
FEATURE [App::DocumentObjectGroupPython] C_element135  label="C_element : 080"  # scripted group (container) (typed FeaturePython)
  n = 5
  ref = C_element
FEATURE [App::DocumentObjectGroupPython] N_element054  label="N_element : 026"  # scripted group (container) (typed FeaturePython)
  n = 5
  ref = N_element
FEATURE [App::DocumentObjectGroupPython] G4_DNA_ADENINE  # scripted group (container) (typed FeaturePython)
  Dunit = g/cm3
  Dvalue = 1
  Group = -> [H_element125,C_element135,N_element054]
  conduct = 2
  density = 1
  expand = 3
  formula = G4_DNA_ADENINE
  name = G4_DNA_ADENINE
  specific = 4
FEATURE [App::DocumentObjectGroupPython] H_element126  label="H_element : 073"  # scripted group (container) (typed FeaturePython)
  n = 4
  ref = H_element
FEATURE [App::DocumentObjectGroupPython] C_element136  label="C_element : 081"  # scripted group (container) (typed FeaturePython)
  n = 5
  ref = C_element
FEATURE [App::DocumentObjectGroupPython] N_element055  label="N_element : 027"  # scripted group (container) (typed FeaturePython)
  n = 5
  ref = N_element
FEATURE [App::DocumentObjectGroupPython] O_element116  label="O_element : 069"  # scripted group (container) (typed FeaturePython)
  n = 1
  ref = O_element
FEATURE [App::DocumentObjectGroupPython] G4_DNA_GUANINE  # scripted group (container) (typed FeaturePython)
  Dunit = g/cm3
  Dvalue = 1
  Group = -> [H_element126,C_element136,N_element055,O_element116]
  conduct = 2
  density = 1
  expand = 3
  formula = G4_DNA_GUANINE
  name = G4_DNA_GUANINE
  specific = 4
FEATURE [App::DocumentObjectGroupPython] H_element127  label="H_element : 074"  # scripted group (container) (typed FeaturePython)
  n = 4
  ref = H_element
FEATURE [App::DocumentObjectGroupPython] C_element137  label="C_element : 082"  # scripted group (container) (typed FeaturePython)
  n = 4
  ref = C_element
FEATURE [App::DocumentObjectGroupPython] N_element056  label="N_element : 028"  # scripted group (container) (typed FeaturePython)
  n = 3
  ref = N_element
FEATURE [App::DocumentObjectGroupPython] O_element117  label="O_element : 070"  # scripted group (container) (typed FeaturePython)
  n = 1
  ref = O_element
FEATURE [App::DocumentObjectGroupPython] G4_DNA_CYTOSINE  # scripted group (container) (typed FeaturePython)
  Dunit = g/cm3
  Dvalue = 1
  Group = -> [H_element127,C_element137,N_element056,O_element117]
  conduct = 2
  density = 1
  expand = 3
  formula = G4_DNA_CYTOSINE
  name = G4_DNA_CYTOSINE
  specific = 4
FEATURE [App::DocumentObjectGroupPython] H_element128  label="H_element : 075"  # scripted group (container) (typed FeaturePython)
  n = 5
  ref = H_element
FEATURE [App::DocumentObjectGroupPython] C_element138  label="C_element : 083"  # scripted group (container) (typed FeaturePython)
  n = 5
  ref = C_element
FEATURE [App::DocumentObjectGroupPython] N_element057  label="N_element : 029"  # scripted group (container) (typed FeaturePython)
  n = 2
  ref = N_element
FEATURE [App::DocumentObjectGroupPython] O_element118  label="O_element : 071"  # scripted group (container) (typed FeaturePython)
  n = 2
  ref = O_element
FEATURE [App::DocumentObjectGroupPython] G4_DNA_THYMINE  # scripted group (container) (typed FeaturePython)
  Dunit = g/cm3
  Dvalue = 1
  Group = -> [H_element128,C_element138,N_element057,O_element118]
  conduct = 2
  density = 1
  expand = 3
  formula = G4_DNA_THYMINE
  name = G4_DNA_THYMINE
  specific = 4
FEATURE [App::DocumentObjectGroupPython] H_element129  label="H_element : 076"  # scripted group (container) (typed FeaturePython)
  n = 3
  ref = H_element
FEATURE [App::DocumentObjectGroupPython] C_element139  label="C_element : 084"  # scripted group (container) (typed FeaturePython)
  n = 4
  ref = C_element
FEATURE [App::DocumentObjectGroupPython] N_element058  label="N_element : 030"  # scripted group (container) (typed FeaturePython)
  n = 2
  ref = N_element
FEATURE [App::DocumentObjectGroupPython] O_element119  label="O_element : 072"  # scripted group (container) (typed FeaturePython)
  n = 2
  ref = O_element
FEATURE [App::DocumentObjectGroupPython] G4_DNA_URACIL  # scripted group (container) (typed FeaturePython)
  Dunit = g/cm3
  Dvalue = 1
  Group = -> [H_element129,C_element139,N_element058,O_element119]
  conduct = 2
  density = 1
  expand = 3
  formula = G4_DNA_URACIL
  name = G4_DNA_URACIL
  specific = 4
FEATURE [App::DocumentObjectGroupPython] H_element130  label="H_element : 077"  # scripted group (container) (typed FeaturePython)
  n = 10
  ref = H_element
FEATURE [App::DocumentObjectGroupPython] C_element140  label="C_element : 085"  # scripted group (container) (typed FeaturePython)
  n = 10
  ref = C_element
FEATURE [App::DocumentObjectGroupPython] N_element059  label="N_element : 031"  # scripted group (container) (typed FeaturePython)
  n = 5
  ref = N_element
FEATURE [App::DocumentObjectGroupPython] O_element120  label="O_element : 073"  # scripted group (container) (typed FeaturePython)
  n = 4
  ref = O_element
FEATURE [App::DocumentObjectGroupPython] G4_DNA_ADENOSINE  # scripted group (container) (typed FeaturePython)
  Dunit = g/cm3
  Dvalue = 1
  Group = -> [H_element130,C_element140,N_element059,O_element120]
  conduct = 2
  density = 1
  expand = 3
  formula = G4_DNA_ADENOSINE
  name = G4_DNA_ADENOSINE
  specific = 4
FEATURE [App::DocumentObjectGroupPython] H_element131  label="H_element : 078"  # scripted group (container) (typed FeaturePython)
  n = 10
  ref = H_element
FEATURE [App::DocumentObjectGroupPython] C_element141  label="C_element : 086"  # scripted group (container) (typed FeaturePython)
  n = 10
  ref = C_element
FEATURE [App::DocumentObjectGroupPython] N_element060  label="N_element : 032"  # scripted group (container) (typed FeaturePython)
  n = 5
  ref = N_element
FEATURE [App::DocumentObjectGroupPython] O_element121  label="O_element : 074"  # scripted group (container) (typed FeaturePython)
  n = 5
  ref = O_element
FEATURE [App::DocumentObjectGroupPython] G4_DNA_GUANOSINE  # scripted group (container) (typed FeaturePython)
  Dunit = g/cm3
  Dvalue = 1
  Group = -> [H_element131,C_element141,N_element060,O_element121]
  conduct = 2
  density = 1
  expand = 3
  formula = G4_DNA_GUANOSINE
  name = G4_DNA_GUANOSINE
  specific = 4
FEATURE [App::DocumentObjectGroupPython] H_element132  label="H_element : 079"  # scripted group (container) (typed FeaturePython)
  n = 10
  ref = H_element
FEATURE [App::DocumentObjectGroupPython] C_element142  label="C_element : 087"  # scripted group (container) (typed FeaturePython)
  n = 9
  ref = C_element
FEATURE [App::DocumentObjectGroupPython] N_element061  label="N_element : 033"  # scripted group (container) (typed FeaturePython)
  n = 3
  ref = N_element
FEATURE [App::DocumentObjectGroupPython] O_element122  label="O_element : 075"  # scripted group (container) (typed FeaturePython)
  n = 5
  ref = O_element
FEATURE [App::DocumentObjectGroupPython] G4_DNA_CYTIDINE  # scripted group (container) (typed FeaturePython)
  Dunit = g/cm3
  Dvalue = 1
  Group = -> [H_element132,C_element142,N_element061,O_element122]
  conduct = 2
  density = 1
  expand = 3
  formula = G4_DNA_CYTIDINE
  name = G4_DNA_CYTIDINE
  specific = 4
FEATURE [App::DocumentObjectGroupPython] H_element133  label="H_element : 080"  # scripted group (container) (typed FeaturePython)
  n = 9
  ref = H_element
FEATURE [App::DocumentObjectGroupPython] C_element143  label="C_element : 088"  # scripted group (container) (typed FeaturePython)
  n = 9
  ref = C_element
FEATURE [App::DocumentObjectGroupPython] N_element062  label="N_element : 034"  # scripted group (container) (typed FeaturePython)
  n = 2
  ref = N_element
FEATURE [App::DocumentObjectGroupPython] O_element123  label="O_element : 076"  # scripted group (container) (typed FeaturePython)
  n = 6
  ref = O_element
FEATURE [App::DocumentObjectGroupPython] G4_DNA_URIDINE  # scripted group (container) (typed FeaturePython)
  Dunit = g/cm3
  Dvalue = 1
  Group = -> [H_element133,C_element143,N_element062,O_element123]
  conduct = 2
  density = 1
  expand = 3
  formula = G4_DNA_URIDINE
  name = G4_DNA_URIDINE
  specific = 4
FEATURE [App::DocumentObjectGroupPython] H_element134  label="H_element : 081"  # scripted group (container) (typed FeaturePython)
  n = 11
  ref = H_element
FEATURE [App::DocumentObjectGroupPython] C_element144  label="C_element : 089"  # scripted group (container) (typed FeaturePython)
  n = 10
  ref = C_element
FEATURE [App::DocumentObjectGroupPython] N_element063  label="N_element : 035"  # scripted group (container) (typed FeaturePython)
  n = 2
  ref = N_element
FEATURE [App::DocumentObjectGroupPython] O_element124  label="O_element : 077"  # scripted group (container) (typed FeaturePython)
  n = 6
  ref = O_element
FEATURE [App::DocumentObjectGroupPython] G4_DNA_METHYLURIDINE  # scripted group (container) (typed FeaturePython)
  Dunit = g/cm3
  Dvalue = 1
  Group = -> [H_element134,C_element144,N_element063,O_element124]
  conduct = 2
  density = 1
  expand = 3
  formula = G4_DNA_METHYLURIDINE
  name = G4_DNA_METHYLURIDINE
  specific = 4
FEATURE [App::DocumentObjectGroupPython] P_element014  label="P_element : 003"  # scripted group (container) (typed FeaturePython)
  n = 1
  ref = P_element
FEATURE [App::DocumentObjectGroupPython] O_element125  label="O_element : 078"  # scripted group (container) (typed FeaturePython)
  n = 3
  ref = O_element
FEATURE [App::DocumentObjectGroupPython] G4_DNA_MONOPHOSPHATE  # scripted group (container) (typed FeaturePython)
  Dunit = g/cm3
  Dvalue = 1
  Group = -> [P_element014,O_element125]
  conduct = 2
  density = 1
  expand = 3
  formula = G4_DNA_MONOPHOSPHATE
  name = G4_DNA_MONOPHOSPHATE
  specific = 4
FEATURE [App::DocumentObjectGroupPython] H_element135  label="H_element : 082"  # scripted group (container) (typed FeaturePython)
  n = 10
  ref = H_element
FEATURE [App::DocumentObjectGroupPython] C_element145  label="C_element : 090"  # scripted group (container) (typed FeaturePython)
  n = 10
  ref = C_element
FEATURE [App::DocumentObjectGroupPython] N_element064  label="N_element : 036"  # scripted group (container) (typed FeaturePython)
  n = 5
  ref = N_element
FEATURE [App::DocumentObjectGroupPython] O_element126  label="O_element : 079"  # scripted group (container) (typed FeaturePython)
  n = 7
  ref = O_element
FEATURE [App::DocumentObjectGroupPython] P_element015  label="P_element : 004"  # scripted group (container) (typed FeaturePython)
  n = 1
  ref = P_element
FEATURE [App::DocumentObjectGroupPython] G4_DNA_A  # scripted group (container) (typed FeaturePython)
  Dunit = g/cm3
  Dvalue = 1
  Group = -> [H_element135,C_element145,N_element064,O_element126,P_element015]
  conduct = 2
  density = 1
  expand = 3
  formula = G4_DNA_A
  name = G4_DNA_A
  specific = 4
FEATURE [App::DocumentObjectGroupPython] H_element136  label="H_element : 083"  # scripted group (container) (typed FeaturePython)
  n = 10
  ref = H_element
FEATURE [App::DocumentObjectGroupPython] C_element146  label="C_element : 091"  # scripted group (container) (typed FeaturePython)
  n = 10
  ref = C_element
FEATURE [App::DocumentObjectGroupPython] N_element065  label="N_element : 037"  # scripted group (container) (typed FeaturePython)
  n = 5
  ref = N_element
FEATURE [App::DocumentObjectGroupPython] O_element127  label="O_element : 8"  # scripted group (container) (typed FeaturePython)
  n = 8
  ref = O_element
FEATURE [App::DocumentObjectGroupPython] P_element016  label="P_element : 005"  # scripted group (container) (typed FeaturePython)
  n = 1
  ref = P_element
FEATURE [App::DocumentObjectGroupPython] G4_DNA_G  # scripted group (container) (typed FeaturePython)
  Dunit = g/cm3
  Dvalue = 1
  Group = -> [H_element136,C_element146,N_element065,O_element127,P_element016]
  conduct = 2
  density = 1
  expand = 3
  formula = G4_DNA_G
  name = G4_DNA_G
  specific = 4
FEATURE [App::DocumentObjectGroupPython] H_element137  label="H_element : 084"  # scripted group (container) (typed FeaturePython)
  n = 10
  ref = H_element
FEATURE [App::DocumentObjectGroupPython] C_element147  label="C_element : 092"  # scripted group (container) (typed FeaturePython)
  n = 9
  ref = C_element
FEATURE [App::DocumentObjectGroupPython] N_element066  label="N_element : 038"  # scripted group (container) (typed FeaturePython)
  n = 3
  ref = N_element
FEATURE [App::DocumentObjectGroupPython] O_element128  label="O_element : 080"  # scripted group (container) (typed FeaturePython)
  n = 8
  ref = O_element
FEATURE [App::DocumentObjectGroupPython] P_element017  label="P_element : 006"  # scripted group (container) (typed FeaturePython)
  n = 1
  ref = P_element
FEATURE [App::DocumentObjectGroupPython] G4_DNA_C  # scripted group (container) (typed FeaturePython)
  Dunit = g/cm3
  Dvalue = 1
  Group = -> [H_element137,C_element147,N_element066,O_element128,P_element017]
  conduct = 2
  density = 1
  expand = 3
  formula = G4_DNA_C
  name = G4_DNA_C
  specific = 4
FEATURE [App::DocumentObjectGroupPython] H_element138  label="H_element : 085"  # scripted group (container) (typed FeaturePython)
  n = 9
  ref = H_element
FEATURE [App::DocumentObjectGroupPython] C_element148  label="C_element : 093"  # scripted group (container) (typed FeaturePython)
  n = 9
  ref = C_element
FEATURE [App::DocumentObjectGroupPython] N_element067  label="N_element : 039"  # scripted group (container) (typed FeaturePython)
  n = 2
  ref = N_element
FEATURE [App::DocumentObjectGroupPython] O_element129  label="O_element : 9"  # scripted group (container) (typed FeaturePython)
  n = 9
  ref = O_element
FEATURE [App::DocumentObjectGroupPython] P_element018  label="P_element : 007"  # scripted group (container) (typed FeaturePython)
  n = 1
  ref = P_element
FEATURE [App::DocumentObjectGroupPython] G4_DNA_U  # scripted group (container) (typed FeaturePython)
  Dunit = g/cm3
  Dvalue = 1
  Group = -> [H_element138,C_element148,N_element067,O_element129,P_element018]
  conduct = 2
  density = 1
  expand = 3
  formula = G4_DNA_U
  name = G4_DNA_U
  specific = 4
FEATURE [App::DocumentObjectGroupPython] H_element139  label="H_element : 086"  # scripted group (container) (typed FeaturePython)
  n = 11
  ref = H_element
FEATURE [App::DocumentObjectGroupPython] C_element149  label="C_element : 094"  # scripted group (container) (typed FeaturePython)
  n = 10
  ref = C_element
FEATURE [App::DocumentObjectGroupPython] N_element068  label="N_element : 040"  # scripted group (container) (typed FeaturePython)
  n = 2
  ref = N_element
FEATURE [App::DocumentObjectGroupPython] O_element130  label="O_element : 081"  # scripted group (container) (typed FeaturePython)
  n = 9
  ref = O_element
FEATURE [App::DocumentObjectGroupPython] P_element019  label="P_element : 008"  # scripted group (container) (typed FeaturePython)
  n = 1
  ref = P_element
FEATURE [App::DocumentObjectGroupPython] G4_DNA_MU  # scripted group (container) (typed FeaturePython)
  Dunit = g/cm3
  Dvalue = 1
  Group = -> [H_element139,C_element149,N_element068,O_element130,P_element019]
  conduct = 2
  density = 1
  expand = 3
  formula = G4_DNA_MU
  name = G4_DNA_MU
  specific = 4
FEATURE [App::DocumentObjectGroupPython] BioChemical  # scripted group (container) (typed FeaturePython)
  Group = -> [G4_CYTOSINE,G4_THYMINE,G4_URACIL,G4_DNA_ADENINE,G4_DNA_GUANINE,G4_DNA_CYTOSINE,G4_DNA_THYMINE,G4_DNA_URACIL,G4_DNA_ADENOSINE,G4_DNA_GUANOSINE,G4_DNA_CYTIDINE,G4_DNA_URIDINE,G4_DNA_METHYLURIDINE,G4_DNA_MONOPHOSPHATE,G4_DNA_A,G4_DNA_G,G4_DNA_C,G4_DNA_U,G4_DNA_MU]
FEATURE [App::DocumentObjectGroupPython] G4Materials  # scripted group (container) (typed FeaturePython)
  Group = -> [NIST,Element,HEP,Space,BioChemical]
  version = 1
FEATURE [App::DocumentObjectGroupPython] Geant4  # scripted group (container) (typed FeaturePython)
  Group = -> [G4Isotopes,G4Elements,G4Materials]
FEATURE [App::DocumentObjectGroupPython] Materials  # scripted group (container) (typed FeaturePython)
  Group = -> [Geant4]
FEATURE [Part::FeaturePython] GDMLBox_WorldBox  # WARN: FeaturePython — macro-defined, semantics opaque (R4)
  lunit = 2
  material = 7
  x = 100
  y = 100
  z = 100
FEATURE [Part::Box] Box  label="Cube"
  AttacherType = Attacher::AttachEngine3D
  Height = 10
  Length = 10
  Width = 10
FEATURE [Part::Cylinder] Cylinder
  Angle = 360
  AttacherType = Attacher::AttachEngine3D
  FirstAngle = 0
  Height = 12
  Placement = pos=(8,5,-1) rot=(0,0,1;0rad)
  Radius = 2
  SecondAngle = 0
FEATURE [Part::Cut] Cut
  Base = -> Box
  Tool = -> Cylinder
FEATURE [Part::FeaturePython] Array  # Draft array (typed FeaturePython)
  AlwaysSyncPlacement = false
  Angle = 360
  ArrayType = 0
  Axis = (0,0,1)
  Base = -> Cut
  Center = (0,0,0)
  Count = 4
  ExpandArray = false
  Fuse = true
  IntervalAxis = (0,0,0)
  IntervalX = (20,0,0)
  IntervalY = (0,20,0)
  IntervalZ = (0,0,100)
  NumberCircles = 3
  NumberPolar = 5
  NumberX = 2
  NumberY = 2
  NumberZ = 1
  PlacementList = 4 placements: [(0,0,0),(0,20,0),(20,0,0),(20,20,0)]
  RadialDistance = 50
  ScaleList = (4) [(1,1,1),(1,1,1),(1,1,1),(1,1,1)]
  Symmetry = 1
  TangentialDistance = 25
FEATURE [App::Part] Part
  Group = -> [Cylinder,Box,Array,Cut]
  Origin = -> Origin001
  Placement = pos=(6,0,0) rot=(0,0,1;0rad)
FEATURE [App::Part] worldVOL
  Group = -> [GDMLBox_WorldBox,Part]
  Origin = -> Origin
